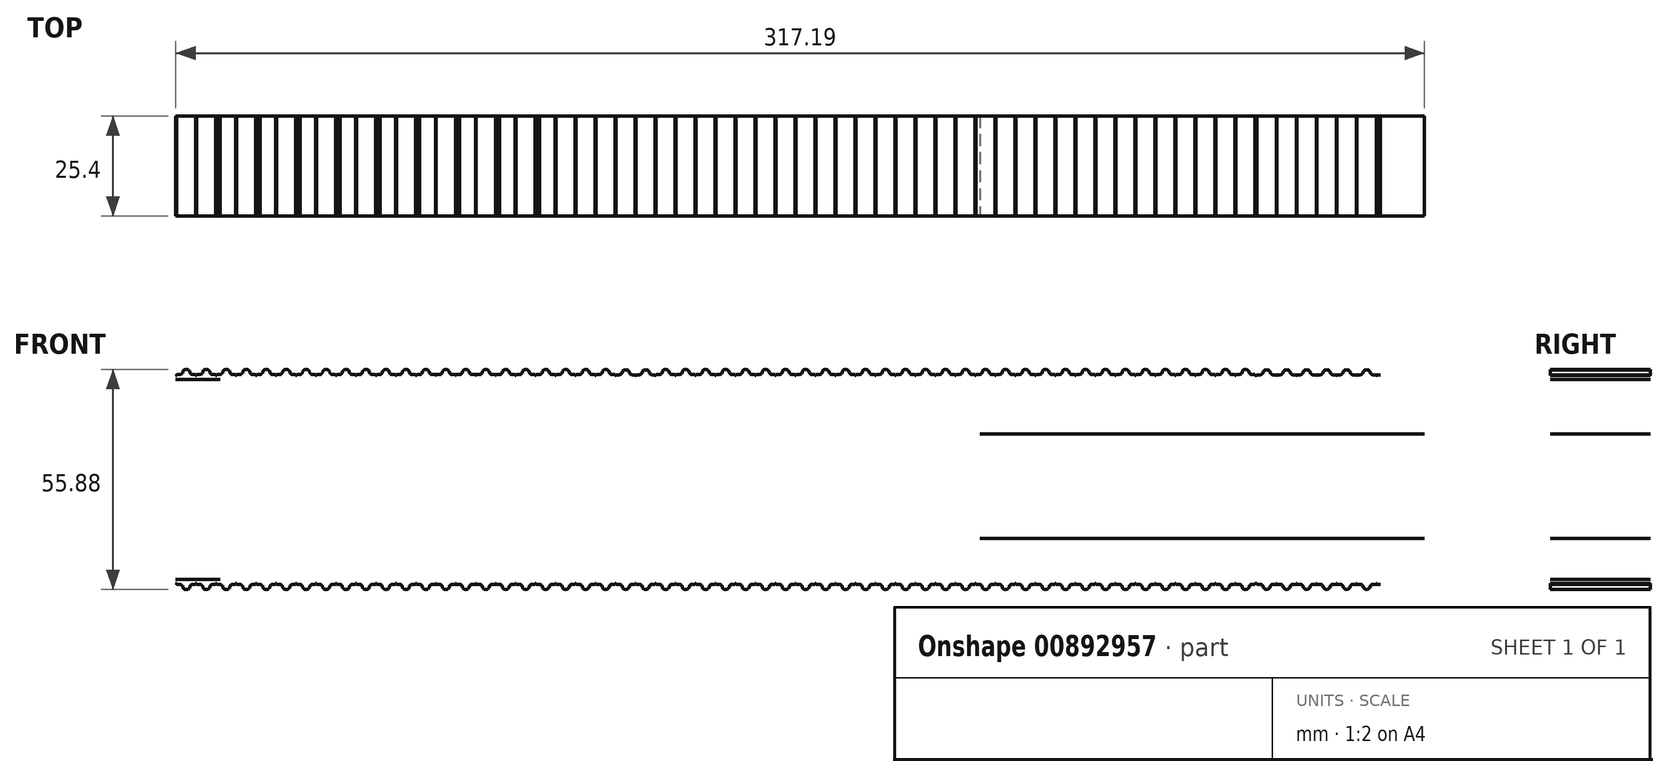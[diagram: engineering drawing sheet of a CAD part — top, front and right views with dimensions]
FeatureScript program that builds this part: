
annotation { "Feature Type Name" : "Feature", "Feature Type Description" : "" }
export const myFeature = defineFeature(function(context is Context, id is Id, definition is map)
    precondition{}
    {
        {
            var Q0;
            Q0=qCreatedBy(makeId("Front.planeOp"),FACE);
            var sketch = newSketch(context, id + "F0", { "sketchPlane" : qUnion([Q0])});
            skLineSegment(sketch, "E0", {"start": v(0, 0) * mm, "end": v(0, -1.05) * mm, "construction": true});
            skLineSegment(sketch, "E1", {"start": v(0, -1.05) * mm, "end": v(0.22, -1.05) * mm});
            skLineSegment(sketch, "E2", {"start": v(0.22, -1.05) * mm, "end": v(0.22, -1.27) * mm});
            skLineSegment(sketch, "E3", {"start": v(0.22, -1.27) * mm, "end": v(1.08, -1.27) * mm});
            skLineSegment(sketch, "E4", {"start": v(1.68, -1.7) * mm, "end": v(1.84, -2.12) * mm});
            skLineSegment(sketch, "E5", {"start": v(2.44, -2.54) * mm, "end": v(2.86, -2.54) * mm});
            skLineSegment(sketch, "E6", {"start": v(3.46, -2.12) * mm, "end": v(3.62, -1.7) * mm});
            skLineSegment(sketch, "E7", {"start": v(4.22, -1.27) * mm, "end": v(5.08, -1.27) * mm});
            skLineSegment(sketch, "E8", {"start": v(5.08, -1.27) * mm, "end": v(5.08, -1.05) * mm});
            skLineSegment(sketch, "E9", {"start": v(5.08, -1.05) * mm, "end": v(5.3, -1.05) * mm});
            skLineSegment(sketch, "E10", {"start": v(5.3, -1.05) * mm, "end": v(5.3, -1.27) * mm});
            skLineSegment(sketch, "E11", {"start": v(5.3, -1.27) * mm, "end": v(6.16, -1.27) * mm});
            skLineSegment(sketch, "E12", {"start": v(6.76, -1.7) * mm, "end": v(6.92, -2.12) * mm});
            skLineSegment(sketch, "E13", {"start": v(7.52, -2.54) * mm, "end": v(7.94, -2.54) * mm});
            skLineSegment(sketch, "E14", {"start": v(8.54, -2.12) * mm, "end": v(8.7, -1.7) * mm});
            skLineSegment(sketch, "E15", {"start": v(9.3, -1.27) * mm, "end": v(10.16, -1.27) * mm});
            skLineSegment(sketch, "E16", {"start": v(10.16, -1.27) * mm, "end": v(10.16, -1.05) * mm});
            skLineSegment(sketch, "E17", {"start": v(10.16, -1.05) * mm, "end": v(10.38, -1.05) * mm});
            skLineSegment(sketch, "E18", {"start": v(11.24, 0) * mm, "end": v(0, 0) * mm});
            skPoint(sketch, "E19", {"position": v(1.76, -1.9) * mm});
            skPoint(sketch, "E20", {"position": v(3.54, -1.9) * mm});
            skPoint(sketch, "E21", {"position": v(2.65, -2.54) * mm});
            skPoint(sketch, "E22", {"position": v(7.73, -2.54) * mm});
            skPoint(sketch, "E23", {"position": v(5.2, -1.05) * mm});
            skLineSegment(sketch, "E24", {"start": v(5.2, -1.05) * mm, "end": v(5.2, -1.34) * mm, "construction": true});
            skLineSegment(sketch, "E25", {"start": v(5.3, -1.16) * mm, "end": v(5.08, -1.16) * mm, "construction": true});
            skPoint(sketch, "E26.visualSharp", {"position": v(1.53, -1.27) * mm});
            skArc(sketch, "E26.filletArc", {"start": v(1.68, -1.7) * mm, "mid": v(1.45, -1.39) * mm, "end": v(1.08, -1.27) * mm});
            skPoint(sketch, "E27.visualSharp", {"position": v(2, -2.54) * mm});
            skArc(sketch, "E27.filletArc", {"start": v(1.84, -2.12) * mm, "mid": v(2.07, -2.42) * mm, "end": v(2.44, -2.54) * mm});
            skPoint(sketch, "E28.visualSharp", {"position": v(3.3, -2.54) * mm});
            skArc(sketch, "E28.filletArc", {"start": v(2.86, -2.54) * mm, "mid": v(3.23, -2.42) * mm, "end": v(3.46, -2.12) * mm});
            skPoint(sketch, "E29.visualSharp", {"position": v(3.77, -1.27) * mm});
            skArc(sketch, "E29.filletArc", {"start": v(4.22, -1.27) * mm, "mid": v(3.85, -1.39) * mm, "end": v(3.62, -1.7) * mm});
            skPoint(sketch, "E30.visualSharp", {"position": v(6.61, -1.27) * mm});
            skArc(sketch, "E30.filletArc", {"start": v(6.76, -1.7) * mm, "mid": v(6.53, -1.39) * mm, "end": v(6.16, -1.27) * mm});
            skPoint(sketch, "E31.visualSharp", {"position": v(7.07, -2.54) * mm});
            skArc(sketch, "E31.filletArc", {"start": v(6.92, -2.12) * mm, "mid": v(7.15, -2.42) * mm, "end": v(7.52, -2.54) * mm});
            skPoint(sketch, "E32.visualSharp", {"position": v(8.39, -2.54) * mm});
            skArc(sketch, "E32.filletArc", {"start": v(7.94, -2.54) * mm, "mid": v(8.3, -2.42) * mm, "end": v(8.54, -2.12) * mm});
            skPoint(sketch, "E33.visualSharp", {"position": v(8.85, -1.27) * mm});
            skArc(sketch, "E33.filletArc", {"start": v(9.3, -1.27) * mm, "mid": v(8.93, -1.39) * mm, "end": v(8.7, -1.7) * mm});
            skLineSegment(sketch, "E34", {"start": v(10.38, -1.05) * mm, "end": v(10.38, -1.27) * mm});
            skLineSegment(sketch, "E35", {"start": v(10.38, -1.27) * mm, "end": v(11.24, -1.27) * mm});
            skLineSegment(sketch, "E36", {"start": v(11.24, -1.27) * mm, "end": v(11.24, 0) * mm, "construction": true});
            skLineSegment(sketch, "E37", {"start": v(0, 0) * mm, "end": v(304.8, 0) * mm, "construction": true});
            skLineSegment(sketch, "E38.0", {"start": v(0, 50.8) * mm, "end": v(304.8, 50.8) * mm, "construction": true});
            skArc(sketch, "E39", {"start": v(0, 50.8) * mm, "mid": v(-25.4, 25.4) * mm, "end": v(0, 0) * mm, "construction": true});
            skLineSegment(sketch, "E40", {"start": v(0, 25.4) * mm, "end": v(304.8, 25.4) * mm, "construction": true});
            skLineSegment(sketch, "E41", {"start": v(152.4, 50.8) * mm, "end": v(152.4, 0) * mm, "construction": true});
            skPoint(sketch, "E42.1.0.0", {"position": v(17.88, -2.53) * mm});
            skLineSegment(sketch, "E42.1.0.1", {"start": v(20.53, -1.26) * mm, "end": v(21.39, -1.26) * mm});
            skPoint(sketch, "E42.1.0.2", {"position": v(17.22, -2.53) * mm});
            skLineSegment(sketch, "E42.1.0.3", {"start": v(18.69, -2.11) * mm, "end": v(18.84, -1.69) * mm});
            skArc(sketch, "E42.1.0.4", {"start": v(16.9, -1.69) * mm, "mid": v(16.67, -1.38) * mm, "end": v(16.3, -1.26) * mm});
            skPoint(sketch, "E42.1.0.5", {"position": v(11.67, -1.26) * mm});
            skPoint(sketch, "E42.1.0.6", {"position": v(19, -1.26) * mm});
            skPoint(sketch, "E42.1.0.7", {"position": v(12.14, -2.53) * mm});
            skArc(sketch, "E42.1.0.8", {"start": v(11.83, -1.69) * mm, "mid": v(11.6, -1.38) * mm, "end": v(11.23, -1.26) * mm});
            skPoint(sketch, "E42.1.0.9", {"position": v(13.92, -1.26) * mm});
            skLineSegment(sketch, "E42.1.0.10", {"start": v(19.44, -1.26) * mm, "end": v(20.3, -1.26) * mm});
            skLineSegment(sketch, "E42.1.0.11", {"start": v(15.45, -1.26) * mm, "end": v(16.3, -1.26) * mm});
            skPoint(sketch, "E42.1.0.12", {"position": v(18.53, -2.53) * mm});
            skLineSegment(sketch, "E42.1.0.13", {"start": v(16.9, -1.69) * mm, "end": v(17.06, -2.11) * mm});
            skLineSegment(sketch, "E42.1.0.14", {"start": v(14.36, -1.26) * mm, "end": v(15.22, -1.26) * mm});
            skPoint(sketch, "E42.1.0.15", {"position": v(16.75, -1.26) * mm});
            skPoint(sketch, "E42.1.0.16", {"position": v(13.45, -2.53) * mm});
            skPoint(sketch, "E42.1.0.17", {"position": v(15.34, -1.04) * mm});
            skPoint(sketch, "E42.1.0.18", {"position": v(13.68, -1.9) * mm});
            skPoint(sketch, "E42.1.0.19", {"position": v(12.8, -2.53) * mm});
            skArc(sketch, "E42.1.0.20", {"start": v(17.06, -2.11) * mm, "mid": v(17.3, -2.42) * mm, "end": v(17.67, -2.53) * mm});
            skArc(sketch, "E42.1.0.21", {"start": v(11.98, -2.11) * mm, "mid": v(12.22, -2.42) * mm, "end": v(12.59, -2.53) * mm});
            skPoint(sketch, "E42.1.0.22", {"position": v(11.9, -1.9) * mm});
            skArc(sketch, "E42.1.0.23", {"start": v(14.36, -1.26) * mm, "mid": v(14, -1.38) * mm, "end": v(13.76, -1.69) * mm});
            skArc(sketch, "E42.1.0.24", {"start": v(18.08, -2.53) * mm, "mid": v(18.45, -2.42) * mm, "end": v(18.69, -2.11) * mm});
            skLineSegment(sketch, "E42.1.0.25", {"start": v(12.59, -2.53) * mm, "end": v(13, -2.53) * mm});
            skLineSegment(sketch, "E42.1.0.26", {"start": v(11.83, -1.69) * mm, "end": v(11.98, -2.11) * mm});
            skArc(sketch, "E42.1.0.27", {"start": v(19.44, -1.26) * mm, "mid": v(19.08, -1.38) * mm, "end": v(18.84, -1.69) * mm});
            skArc(sketch, "E42.1.0.28", {"start": v(13, -2.53) * mm, "mid": v(13.37, -2.42) * mm, "end": v(13.6, -2.11) * mm});
            skLineSegment(sketch, "E42.1.0.29", {"start": v(13.6, -2.11) * mm, "end": v(13.76, -1.69) * mm});
            skLineSegment(sketch, "E42.1.0.30", {"start": v(17.67, -2.53) * mm, "end": v(18.08, -2.53) * mm});
            skLineSegment(sketch, "E42.1.0.31", {"start": v(15.34, -1.04) * mm, "end": v(15.34, -1.33) * mm, "construction": true});
            skLineSegment(sketch, "E42.1.0.32", {"start": v(20.3, -1.26) * mm, "end": v(20.3, -1.04) * mm});
            skLineSegment(sketch, "E42.1.0.33", {"start": v(20.53, -1.04) * mm, "end": v(20.53, -1.26) * mm});
            skLineSegment(sketch, "E42.1.0.34", {"start": v(15.22, -1.26) * mm, "end": v(15.22, -1.04) * mm});
            skLineSegment(sketch, "E42.1.0.35", {"start": v(15.45, -1.15) * mm, "end": v(15.22, -1.15) * mm, "construction": true});
            skLineSegment(sketch, "E42.1.0.36", {"start": v(15.45, -1.04) * mm, "end": v(15.45, -1.26) * mm});
            skLineSegment(sketch, "E42.1.0.37", {"start": v(15.22, -1.04) * mm, "end": v(15.45, -1.04) * mm});
            skLineSegment(sketch, "E42.1.0.38", {"start": v(20.3, -1.04) * mm, "end": v(20.53, -1.04) * mm});
            skPoint(sketch, "E42.2.0.0", {"position": v(28.02, -2.53) * mm});
            skLineSegment(sketch, "E42.2.0.1", {"start": v(30.67, -1.26) * mm, "end": v(31.53, -1.26) * mm});
            skPoint(sketch, "E42.2.0.2", {"position": v(27.36, -2.53) * mm});
            skLineSegment(sketch, "E42.2.0.3", {"start": v(28.83, -2.1) * mm, "end": v(28.99, -1.68) * mm});
            skArc(sketch, "E42.2.0.4", {"start": v(27.05, -1.68) * mm, "mid": v(26.82, -1.38) * mm, "end": v(26.45, -1.26) * mm});
            skPoint(sketch, "E42.2.0.5", {"position": v(21.82, -1.26) * mm});
            skPoint(sketch, "E42.2.0.6", {"position": v(29.14, -1.26) * mm});
            skPoint(sketch, "E42.2.0.7", {"position": v(22.28, -2.53) * mm});
            skArc(sketch, "E42.2.0.8", {"start": v(21.97, -1.68) * mm, "mid": v(21.74, -1.38) * mm, "end": v(21.37, -1.26) * mm});
            skPoint(sketch, "E42.2.0.9", {"position": v(24.06, -1.26) * mm});
            skLineSegment(sketch, "E42.2.0.10", {"start": v(29.59, -1.26) * mm, "end": v(30.45, -1.26) * mm});
            skLineSegment(sketch, "E42.2.0.11", {"start": v(25.6, -1.26) * mm, "end": v(26.45, -1.26) * mm});
            skPoint(sketch, "E42.2.0.12", {"position": v(28.68, -2.53) * mm});
            skLineSegment(sketch, "E42.2.0.13", {"start": v(27.05, -1.68) * mm, "end": v(27.2, -2.1) * mm});
            skLineSegment(sketch, "E42.2.0.14", {"start": v(24.5, -1.26) * mm, "end": v(25.37, -1.26) * mm});
            skPoint(sketch, "E42.2.0.15", {"position": v(26.9, -1.26) * mm});
            skPoint(sketch, "E42.2.0.16", {"position": v(23.6, -2.53) * mm});
            skPoint(sketch, "E42.2.0.17", {"position": v(25.48, -1.04) * mm});
            skPoint(sketch, "E42.2.0.18", {"position": v(23.83, -1.9) * mm});
            skPoint(sketch, "E42.2.0.19", {"position": v(22.94, -2.53) * mm});
            skArc(sketch, "E42.2.0.20", {"start": v(27.2, -2.1) * mm, "mid": v(27.44, -2.41) * mm, "end": v(27.8, -2.53) * mm});
            skArc(sketch, "E42.2.0.21", {"start": v(22.13, -2.1) * mm, "mid": v(22.36, -2.41) * mm, "end": v(22.73, -2.53) * mm});
            skPoint(sketch, "E42.2.0.22", {"position": v(22.05, -1.9) * mm});
            skArc(sketch, "E42.2.0.23", {"start": v(24.5, -1.26) * mm, "mid": v(24.14, -1.38) * mm, "end": v(23.9, -1.68) * mm});
            skArc(sketch, "E42.2.0.24", {"start": v(28.23, -2.53) * mm, "mid": v(28.6, -2.41) * mm, "end": v(28.83, -2.1) * mm});
            skLineSegment(sketch, "E42.2.0.25", {"start": v(22.73, -2.53) * mm, "end": v(23.15, -2.53) * mm});
            skLineSegment(sketch, "E42.2.0.26", {"start": v(21.97, -1.68) * mm, "end": v(22.13, -2.1) * mm});
            skArc(sketch, "E42.2.0.27", {"start": v(29.59, -1.26) * mm, "mid": v(29.22, -1.38) * mm, "end": v(28.99, -1.68) * mm});
            skArc(sketch, "E42.2.0.28", {"start": v(23.15, -2.53) * mm, "mid": v(23.52, -2.41) * mm, "end": v(23.75, -2.1) * mm});
            skLineSegment(sketch, "E42.2.0.29", {"start": v(23.75, -2.1) * mm, "end": v(23.9, -1.68) * mm});
            skLineSegment(sketch, "E42.2.0.30", {"start": v(27.8, -2.53) * mm, "end": v(28.23, -2.53) * mm});
            skLineSegment(sketch, "E42.2.0.31", {"start": v(25.48, -1.04) * mm, "end": v(25.48, -1.33) * mm, "construction": true});
            skLineSegment(sketch, "E42.2.0.32", {"start": v(30.45, -1.26) * mm, "end": v(30.45, -1.04) * mm});
            skLineSegment(sketch, "E42.2.0.33", {"start": v(30.67, -1.04) * mm, "end": v(30.67, -1.26) * mm});
            skLineSegment(sketch, "E42.2.0.34", {"start": v(25.37, -1.26) * mm, "end": v(25.37, -1.04) * mm});
            skLineSegment(sketch, "E42.2.0.35", {"start": v(25.6, -1.15) * mm, "end": v(25.37, -1.15) * mm, "construction": true});
            skLineSegment(sketch, "E42.2.0.36", {"start": v(25.6, -1.04) * mm, "end": v(25.6, -1.26) * mm});
            skLineSegment(sketch, "E42.2.0.37", {"start": v(25.37, -1.04) * mm, "end": v(25.6, -1.04) * mm});
            skLineSegment(sketch, "E42.2.0.38", {"start": v(30.45, -1.04) * mm, "end": v(30.67, -1.04) * mm});
            skPoint(sketch, "E42.3.0.0", {"position": v(38.16, -2.52) * mm});
            skLineSegment(sketch, "E42.3.0.1", {"start": v(40.81, -1.25) * mm, "end": v(41.67, -1.25) * mm});
            skPoint(sketch, "E42.3.0.2", {"position": v(37.5, -2.52) * mm});
            skLineSegment(sketch, "E42.3.0.3", {"start": v(38.97, -2.1) * mm, "end": v(39.13, -1.68) * mm});
            skArc(sketch, "E42.3.0.4", {"start": v(37.2, -1.68) * mm, "mid": v(36.96, -1.37) * mm, "end": v(36.6, -1.25) * mm});
            skPoint(sketch, "E42.3.0.5", {"position": v(31.96, -1.25) * mm});
            skPoint(sketch, "E42.3.0.6", {"position": v(39.28, -1.25) * mm});
            skPoint(sketch, "E42.3.0.7", {"position": v(32.43, -2.52) * mm});
            skArc(sketch, "E42.3.0.8", {"start": v(32.12, -1.68) * mm, "mid": v(31.88, -1.37) * mm, "end": v(31.51, -1.25) * mm});
            skPoint(sketch, "E42.3.0.9", {"position": v(34.2, -1.25) * mm});
            skLineSegment(sketch, "E42.3.0.10", {"start": v(39.73, -1.25) * mm, "end": v(40.6, -1.25) * mm});
            skLineSegment(sketch, "E42.3.0.11", {"start": v(35.73, -1.25) * mm, "end": v(36.6, -1.25) * mm});
            skPoint(sketch, "E42.3.0.12", {"position": v(38.82, -2.52) * mm});
            skLineSegment(sketch, "E42.3.0.13", {"start": v(37.2, -1.68) * mm, "end": v(37.35, -2.1) * mm});
            skLineSegment(sketch, "E42.3.0.14", {"start": v(34.65, -1.25) * mm, "end": v(35.51, -1.25) * mm});
            skPoint(sketch, "E42.3.0.15", {"position": v(37.04, -1.25) * mm});
            skPoint(sketch, "E42.3.0.16", {"position": v(33.74, -2.52) * mm});
            skPoint(sketch, "E42.3.0.17", {"position": v(35.62, -1.03) * mm});
            skPoint(sketch, "E42.3.0.18", {"position": v(33.97, -1.89) * mm});
            skPoint(sketch, "E42.3.0.19", {"position": v(33.08, -2.52) * mm});
            skArc(sketch, "E42.3.0.20", {"start": v(37.35, -2.1) * mm, "mid": v(37.59, -2.4) * mm, "end": v(37.95, -2.52) * mm});
            skArc(sketch, "E42.3.0.21", {"start": v(32.27, -2.1) * mm, "mid": v(32.5, -2.4) * mm, "end": v(32.87, -2.52) * mm});
            skPoint(sketch, "E42.3.0.22", {"position": v(32.2, -1.89) * mm});
            skArc(sketch, "E42.3.0.23", {"start": v(34.65, -1.25) * mm, "mid": v(34.28, -1.37) * mm, "end": v(34.05, -1.68) * mm});
            skArc(sketch, "E42.3.0.24", {"start": v(38.37, -2.52) * mm, "mid": v(38.74, -2.4) * mm, "end": v(38.97, -2.1) * mm});
            skLineSegment(sketch, "E42.3.0.25", {"start": v(32.87, -2.52) * mm, "end": v(33.3, -2.52) * mm});
            skLineSegment(sketch, "E42.3.0.26", {"start": v(32.12, -1.68) * mm, "end": v(32.27, -2.1) * mm});
            skArc(sketch, "E42.3.0.27", {"start": v(39.73, -1.25) * mm, "mid": v(39.36, -1.37) * mm, "end": v(39.13, -1.68) * mm});
            skArc(sketch, "E42.3.0.28", {"start": v(33.3, -2.52) * mm, "mid": v(33.66, -2.4) * mm, "end": v(33.9, -2.1) * mm});
            skLineSegment(sketch, "E42.3.0.29", {"start": v(33.9, -2.1) * mm, "end": v(34.05, -1.68) * mm});
            skLineSegment(sketch, "E42.3.0.30", {"start": v(37.95, -2.52) * mm, "end": v(38.37, -2.52) * mm});
            skLineSegment(sketch, "E42.3.0.31", {"start": v(35.62, -1.03) * mm, "end": v(35.62, -1.32) * mm, "construction": true});
            skLineSegment(sketch, "E42.3.0.32", {"start": v(40.6, -1.25) * mm, "end": v(40.6, -1.03) * mm});
            skLineSegment(sketch, "E42.3.0.33", {"start": v(40.81, -1.03) * mm, "end": v(40.81, -1.25) * mm});
            skLineSegment(sketch, "E42.3.0.34", {"start": v(35.51, -1.25) * mm, "end": v(35.51, -1.03) * mm});
            skLineSegment(sketch, "E42.3.0.35", {"start": v(35.73, -1.14) * mm, "end": v(35.51, -1.14) * mm, "construction": true});
            skLineSegment(sketch, "E42.3.0.36", {"start": v(35.73, -1.03) * mm, "end": v(35.73, -1.25) * mm});
            skLineSegment(sketch, "E42.3.0.37", {"start": v(35.51, -1.03) * mm, "end": v(35.73, -1.03) * mm});
            skLineSegment(sketch, "E42.3.0.38", {"start": v(40.6, -1.03) * mm, "end": v(40.81, -1.03) * mm});
            skPoint(sketch, "E42.4.0.0", {"position": v(48.3, -2.52) * mm});
            skLineSegment(sketch, "E42.4.0.1", {"start": v(50.96, -1.25) * mm, "end": v(51.82, -1.25) * mm});
            skPoint(sketch, "E42.4.0.2", {"position": v(47.65, -2.52) * mm});
            skLineSegment(sketch, "E42.4.0.3", {"start": v(49.12, -2.1) * mm, "end": v(49.27, -1.67) * mm});
            skArc(sketch, "E42.4.0.4", {"start": v(47.34, -1.67) * mm, "mid": v(47.1, -1.37) * mm, "end": v(46.74, -1.25) * mm});
            skPoint(sketch, "E42.4.0.5", {"position": v(42.1, -1.25) * mm});
            skPoint(sketch, "E42.4.0.6", {"position": v(49.43, -1.25) * mm});
            skPoint(sketch, "E42.4.0.7", {"position": v(42.57, -2.52) * mm});
            skArc(sketch, "E42.4.0.8", {"start": v(42.26, -1.67) * mm, "mid": v(42.03, -1.37) * mm, "end": v(41.66, -1.25) * mm});
            skPoint(sketch, "E42.4.0.9", {"position": v(44.35, -1.25) * mm});
            skLineSegment(sketch, "E42.4.0.10", {"start": v(49.88, -1.25) * mm, "end": v(50.74, -1.25) * mm});
            skLineSegment(sketch, "E42.4.0.11", {"start": v(45.88, -1.25) * mm, "end": v(46.74, -1.25) * mm});
            skPoint(sketch, "E42.4.0.12", {"position": v(48.96, -2.52) * mm});
            skLineSegment(sketch, "E42.4.0.13", {"start": v(47.34, -1.67) * mm, "end": v(47.5, -2.1) * mm});
            skLineSegment(sketch, "E42.4.0.14", {"start": v(44.8, -1.25) * mm, "end": v(45.66, -1.25) * mm});
            skPoint(sketch, "E42.4.0.15", {"position": v(47.19, -1.25) * mm});
            skPoint(sketch, "E42.4.0.16", {"position": v(43.88, -2.52) * mm});
            skPoint(sketch, "E42.4.0.17", {"position": v(45.77, -1.03) * mm});
            skPoint(sketch, "E42.4.0.18", {"position": v(44.12, -1.88) * mm});
            skPoint(sketch, "E42.4.0.19", {"position": v(43.23, -2.52) * mm});
            skArc(sketch, "E42.4.0.20", {"start": v(47.5, -2.1) * mm, "mid": v(47.73, -2.4) * mm, "end": v(48.1, -2.52) * mm});
            skArc(sketch, "E42.4.0.21", {"start": v(42.42, -2.1) * mm, "mid": v(42.65, -2.4) * mm, "end": v(43.02, -2.52) * mm});
            skPoint(sketch, "E42.4.0.22", {"position": v(42.34, -1.88) * mm});
            skArc(sketch, "E42.4.0.23", {"start": v(44.8, -1.25) * mm, "mid": v(44.43, -1.37) * mm, "end": v(44.2, -1.67) * mm});
            skArc(sketch, "E42.4.0.24", {"start": v(48.52, -2.52) * mm, "mid": v(48.88, -2.4) * mm, "end": v(49.12, -2.1) * mm});
            skLineSegment(sketch, "E42.4.0.25", {"start": v(43.02, -2.52) * mm, "end": v(43.44, -2.52) * mm});
            skLineSegment(sketch, "E42.4.0.26", {"start": v(42.26, -1.67) * mm, "end": v(42.42, -2.1) * mm});
            skArc(sketch, "E42.4.0.27", {"start": v(49.88, -1.25) * mm, "mid": v(49.5, -1.37) * mm, "end": v(49.27, -1.67) * mm});
            skArc(sketch, "E42.4.0.28", {"start": v(43.44, -2.52) * mm, "mid": v(43.8, -2.4) * mm, "end": v(44.04, -2.1) * mm});
            skLineSegment(sketch, "E42.4.0.29", {"start": v(44.04, -2.1) * mm, "end": v(44.2, -1.67) * mm});
            skLineSegment(sketch, "E42.4.0.30", {"start": v(48.1, -2.52) * mm, "end": v(48.52, -2.52) * mm});
            skLineSegment(sketch, "E42.4.0.31", {"start": v(45.77, -1.03) * mm, "end": v(45.77, -1.32) * mm, "construction": true});
            skLineSegment(sketch, "E42.4.0.32", {"start": v(50.74, -1.25) * mm, "end": v(50.74, -1.03) * mm});
            skLineSegment(sketch, "E42.4.0.33", {"start": v(50.96, -1.03) * mm, "end": v(50.96, -1.25) * mm});
            skLineSegment(sketch, "E42.4.0.34", {"start": v(45.66, -1.25) * mm, "end": v(45.66, -1.03) * mm});
            skLineSegment(sketch, "E42.4.0.35", {"start": v(45.88, -1.14) * mm, "end": v(45.66, -1.14) * mm, "construction": true});
            skLineSegment(sketch, "E42.4.0.36", {"start": v(45.88, -1.03) * mm, "end": v(45.88, -1.25) * mm});
            skLineSegment(sketch, "E42.4.0.37", {"start": v(45.66, -1.03) * mm, "end": v(45.88, -1.03) * mm});
            skLineSegment(sketch, "E42.4.0.38", {"start": v(50.74, -1.03) * mm, "end": v(50.96, -1.03) * mm});
            skPoint(sketch, "E42.5.0.0", {"position": v(58.45, -2.51) * mm});
            skLineSegment(sketch, "E42.5.0.1", {"start": v(61.1, -1.24) * mm, "end": v(61.96, -1.24) * mm});
            skPoint(sketch, "E42.5.0.2", {"position": v(57.8, -2.51) * mm});
            skLineSegment(sketch, "E42.5.0.3", {"start": v(59.26, -2.1) * mm, "end": v(59.42, -1.67) * mm});
            skArc(sketch, "E42.5.0.4", {"start": v(57.48, -1.67) * mm, "mid": v(57.25, -1.36) * mm, "end": v(56.88, -1.24) * mm});
            skPoint(sketch, "E42.5.0.5", {"position": v(52.25, -1.24) * mm});
            skPoint(sketch, "E42.5.0.6", {"position": v(59.57, -1.24) * mm});
            skPoint(sketch, "E42.5.0.7", {"position": v(52.71, -2.51) * mm});
            skArc(sketch, "E42.5.0.8", {"start": v(52.4, -1.67) * mm, "mid": v(52.17, -1.36) * mm, "end": v(51.8, -1.24) * mm});
            skPoint(sketch, "E42.5.0.9", {"position": v(54.5, -1.24) * mm});
            skLineSegment(sketch, "E42.5.0.10", {"start": v(60.02, -1.24) * mm, "end": v(60.88, -1.24) * mm});
            skLineSegment(sketch, "E42.5.0.11", {"start": v(56.02, -1.24) * mm, "end": v(56.88, -1.24) * mm});
            skPoint(sketch, "E42.5.0.12", {"position": v(59.1, -2.51) * mm});
            skLineSegment(sketch, "E42.5.0.13", {"start": v(57.48, -1.67) * mm, "end": v(57.64, -2.1) * mm});
            skLineSegment(sketch, "E42.5.0.14", {"start": v(54.94, -1.24) * mm, "end": v(55.8, -1.24) * mm});
            skPoint(sketch, "E42.5.0.15", {"position": v(57.33, -1.24) * mm});
            skPoint(sketch, "E42.5.0.16", {"position": v(54.03, -2.51) * mm});
            skPoint(sketch, "E42.5.0.17", {"position": v(55.91, -1.02) * mm});
            skPoint(sketch, "E42.5.0.18", {"position": v(54.26, -1.88) * mm});
            skPoint(sketch, "E42.5.0.19", {"position": v(53.37, -2.51) * mm});
            skArc(sketch, "E42.5.0.20", {"start": v(57.64, -2.1) * mm, "mid": v(57.87, -2.4) * mm, "end": v(58.24, -2.51) * mm});
            skArc(sketch, "E42.5.0.21", {"start": v(52.56, -2.1) * mm, "mid": v(52.8, -2.4) * mm, "end": v(53.16, -2.51) * mm});
            skPoint(sketch, "E42.5.0.22", {"position": v(52.48, -1.88) * mm});
            skArc(sketch, "E42.5.0.23", {"start": v(54.94, -1.24) * mm, "mid": v(54.57, -1.36) * mm, "end": v(54.34, -1.67) * mm});
            skArc(sketch, "E42.5.0.24", {"start": v(58.66, -2.51) * mm, "mid": v(59.03, -2.4) * mm, "end": v(59.26, -2.1) * mm});
            skLineSegment(sketch, "E42.5.0.25", {"start": v(53.16, -2.51) * mm, "end": v(53.58, -2.51) * mm});
            skLineSegment(sketch, "E42.5.0.26", {"start": v(52.4, -1.67) * mm, "end": v(52.56, -2.1) * mm});
            skArc(sketch, "E42.5.0.27", {"start": v(60.02, -1.24) * mm, "mid": v(59.65, -1.36) * mm, "end": v(59.42, -1.67) * mm});
            skArc(sketch, "E42.5.0.28", {"start": v(53.58, -2.51) * mm, "mid": v(53.95, -2.4) * mm, "end": v(54.18, -2.1) * mm});
            skLineSegment(sketch, "E42.5.0.29", {"start": v(54.18, -2.1) * mm, "end": v(54.34, -1.67) * mm});
            skLineSegment(sketch, "E42.5.0.30", {"start": v(58.24, -2.51) * mm, "end": v(58.66, -2.51) * mm});
            skLineSegment(sketch, "E42.5.0.31", {"start": v(55.91, -1.02) * mm, "end": v(55.91, -1.31) * mm, "construction": true});
            skLineSegment(sketch, "E42.5.0.32", {"start": v(60.88, -1.24) * mm, "end": v(60.88, -1.02) * mm});
            skLineSegment(sketch, "E42.5.0.33", {"start": v(61.1, -1.02) * mm, "end": v(61.1, -1.24) * mm});
            skLineSegment(sketch, "E42.5.0.34", {"start": v(55.8, -1.24) * mm, "end": v(55.8, -1.02) * mm});
            skLineSegment(sketch, "E42.5.0.35", {"start": v(56.02, -1.13) * mm, "end": v(55.8, -1.13) * mm, "construction": true});
            skLineSegment(sketch, "E42.5.0.36", {"start": v(56.02, -1.02) * mm, "end": v(56.02, -1.24) * mm});
            skLineSegment(sketch, "E42.5.0.37", {"start": v(55.8, -1.02) * mm, "end": v(56.02, -1.02) * mm});
            skLineSegment(sketch, "E42.5.0.38", {"start": v(60.88, -1.02) * mm, "end": v(61.1, -1.02) * mm});
            skPoint(sketch, "E42.6.0.0", {"position": v(68.6, -2.5) * mm});
            skLineSegment(sketch, "E42.6.0.1", {"start": v(71.25, -1.24) * mm, "end": v(72.1, -1.24) * mm});
            skPoint(sketch, "E42.6.0.2", {"position": v(67.94, -2.5) * mm});
            skLineSegment(sketch, "E42.6.0.3", {"start": v(69.4, -2.09) * mm, "end": v(69.56, -1.66) * mm});
            skArc(sketch, "E42.6.0.4", {"start": v(67.63, -1.66) * mm, "mid": v(67.4, -1.36) * mm, "end": v(67.03, -1.24) * mm});
            skPoint(sketch, "E42.6.0.5", {"position": v(62.4, -1.24) * mm});
            skPoint(sketch, "E42.6.0.6", {"position": v(69.71, -1.24) * mm});
            skPoint(sketch, "E42.6.0.7", {"position": v(62.86, -2.5) * mm});
            skArc(sketch, "E42.6.0.8", {"start": v(62.55, -1.66) * mm, "mid": v(62.31, -1.36) * mm, "end": v(61.95, -1.24) * mm});
            skPoint(sketch, "E42.6.0.9", {"position": v(64.63, -1.24) * mm});
            skLineSegment(sketch, "E42.6.0.10", {"start": v(70.16, -1.24) * mm, "end": v(71.02, -1.24) * mm});
            skLineSegment(sketch, "E42.6.0.11", {"start": v(66.17, -1.24) * mm, "end": v(67.03, -1.24) * mm});
            skPoint(sketch, "E42.6.0.12", {"position": v(69.25, -2.5) * mm});
            skLineSegment(sketch, "E42.6.0.13", {"start": v(67.63, -1.66) * mm, "end": v(67.78, -2.09) * mm});
            skLineSegment(sketch, "E42.6.0.14", {"start": v(65.08, -1.24) * mm, "end": v(65.94, -1.24) * mm});
            skPoint(sketch, "E42.6.0.15", {"position": v(67.47, -1.24) * mm});
            skPoint(sketch, "E42.6.0.16", {"position": v(64.17, -2.5) * mm});
            skPoint(sketch, "E42.6.0.17", {"position": v(66.05, -1.02) * mm});
            skPoint(sketch, "E42.6.0.18", {"position": v(64.4, -1.87) * mm});
            skPoint(sketch, "E42.6.0.19", {"position": v(63.51, -2.5) * mm});
            skArc(sketch, "E42.6.0.20", {"start": v(67.78, -2.09) * mm, "mid": v(68.02, -2.4) * mm, "end": v(68.39, -2.5) * mm});
            skArc(sketch, "E42.6.0.21", {"start": v(62.7, -2.09) * mm, "mid": v(62.94, -2.4) * mm, "end": v(63.3, -2.5) * mm});
            skPoint(sketch, "E42.6.0.22", {"position": v(62.63, -1.87) * mm});
            skArc(sketch, "E42.6.0.23", {"start": v(65.08, -1.24) * mm, "mid": v(64.72, -1.36) * mm, "end": v(64.48, -1.66) * mm});
            skArc(sketch, "E42.6.0.24", {"start": v(68.8, -2.5) * mm, "mid": v(69.17, -2.4) * mm, "end": v(69.4, -2.09) * mm});
            skLineSegment(sketch, "E42.6.0.25", {"start": v(63.3, -2.5) * mm, "end": v(63.72, -2.5) * mm});
            skLineSegment(sketch, "E42.6.0.26", {"start": v(62.55, -1.66) * mm, "end": v(62.7, -2.09) * mm});
            skArc(sketch, "E42.6.0.27", {"start": v(70.16, -1.24) * mm, "mid": v(69.8, -1.36) * mm, "end": v(69.56, -1.66) * mm});
            skArc(sketch, "E42.6.0.28", {"start": v(63.72, -2.5) * mm, "mid": v(64.1, -2.4) * mm, "end": v(64.33, -2.09) * mm});
            skLineSegment(sketch, "E42.6.0.29", {"start": v(64.33, -2.09) * mm, "end": v(64.48, -1.66) * mm});
            skLineSegment(sketch, "E42.6.0.30", {"start": v(68.39, -2.5) * mm, "end": v(68.8, -2.5) * mm});
            skLineSegment(sketch, "E42.6.0.31", {"start": v(66.05, -1.02) * mm, "end": v(66.05, -1.3) * mm, "construction": true});
            skLineSegment(sketch, "E42.6.0.32", {"start": v(71.02, -1.24) * mm, "end": v(71.02, -1.02) * mm});
            skLineSegment(sketch, "E42.6.0.33", {"start": v(71.25, -1.02) * mm, "end": v(71.25, -1.24) * mm});
            skLineSegment(sketch, "E42.6.0.34", {"start": v(65.94, -1.24) * mm, "end": v(65.94, -1.02) * mm});
            skLineSegment(sketch, "E42.6.0.35", {"start": v(66.17, -1.13) * mm, "end": v(65.94, -1.13) * mm, "construction": true});
            skLineSegment(sketch, "E42.6.0.36", {"start": v(66.17, -1.02) * mm, "end": v(66.17, -1.24) * mm});
            skLineSegment(sketch, "E42.6.0.37", {"start": v(65.94, -1.02) * mm, "end": v(66.17, -1.02) * mm});
            skLineSegment(sketch, "E42.6.0.38", {"start": v(71.02, -1.02) * mm, "end": v(71.25, -1.02) * mm});
            skPoint(sketch, "E42.7.0.0", {"position": v(78.74, -2.5) * mm});
            skLineSegment(sketch, "E42.7.0.1", {"start": v(81.39, -1.23) * mm, "end": v(82.25, -1.23) * mm});
            skPoint(sketch, "E42.7.0.2", {"position": v(78.08, -2.5) * mm});
            skLineSegment(sketch, "E42.7.0.3", {"start": v(79.55, -2.08) * mm, "end": v(79.7, -1.66) * mm});
            skArc(sketch, "E42.7.0.4", {"start": v(77.77, -1.66) * mm, "mid": v(77.54, -1.35) * mm, "end": v(77.17, -1.23) * mm});
            skPoint(sketch, "E42.7.0.5", {"position": v(72.54, -1.23) * mm});
            skPoint(sketch, "E42.7.0.6", {"position": v(79.86, -1.23) * mm});
            skPoint(sketch, "E42.7.0.7", {"position": v(73, -2.5) * mm});
            skArc(sketch, "E42.7.0.8", {"start": v(72.7, -1.66) * mm, "mid": v(72.46, -1.35) * mm, "end": v(72.1, -1.23) * mm});
            skPoint(sketch, "E42.7.0.9", {"position": v(74.78, -1.23) * mm});
            skLineSegment(sketch, "E42.7.0.10", {"start": v(80.3, -1.23) * mm, "end": v(81.17, -1.23) * mm});
            skLineSegment(sketch, "E42.7.0.11", {"start": v(76.3, -1.23) * mm, "end": v(77.17, -1.23) * mm});
            skPoint(sketch, "E42.7.0.12", {"position": v(79.4, -2.5) * mm});
            skLineSegment(sketch, "E42.7.0.13", {"start": v(77.77, -1.66) * mm, "end": v(77.93, -2.08) * mm});
            skLineSegment(sketch, "E42.7.0.14", {"start": v(75.23, -1.23) * mm, "end": v(76.09, -1.23) * mm});
            skPoint(sketch, "E42.7.0.15", {"position": v(77.62, -1.23) * mm});
            skPoint(sketch, "E42.7.0.16", {"position": v(74.32, -2.5) * mm});
            skPoint(sketch, "E42.7.0.17", {"position": v(76.2, -1.01) * mm});
            skPoint(sketch, "E42.7.0.18", {"position": v(74.55, -1.87) * mm});
            skPoint(sketch, "E42.7.0.19", {"position": v(73.66, -2.5) * mm});
            skArc(sketch, "E42.7.0.20", {"start": v(77.93, -2.08) * mm, "mid": v(78.16, -2.39) * mm, "end": v(78.53, -2.5) * mm});
            skArc(sketch, "E42.7.0.21", {"start": v(72.85, -2.08) * mm, "mid": v(73.08, -2.39) * mm, "end": v(73.45, -2.5) * mm});
            skPoint(sketch, "E42.7.0.22", {"position": v(72.77, -1.87) * mm});
            skArc(sketch, "E42.7.0.23", {"start": v(75.23, -1.23) * mm, "mid": v(74.86, -1.35) * mm, "end": v(74.63, -1.66) * mm});
            skArc(sketch, "E42.7.0.24", {"start": v(78.95, -2.5) * mm, "mid": v(79.32, -2.39) * mm, "end": v(79.55, -2.08) * mm});
            skLineSegment(sketch, "E42.7.0.25", {"start": v(73.45, -2.5) * mm, "end": v(73.87, -2.5) * mm});
            skLineSegment(sketch, "E42.7.0.26", {"start": v(72.7, -1.66) * mm, "end": v(72.85, -2.08) * mm});
            skArc(sketch, "E42.7.0.27", {"start": v(80.3, -1.23) * mm, "mid": v(79.94, -1.35) * mm, "end": v(79.7, -1.66) * mm});
            skArc(sketch, "E42.7.0.28", {"start": v(73.87, -2.5) * mm, "mid": v(74.24, -2.39) * mm, "end": v(74.47, -2.08) * mm});
            skLineSegment(sketch, "E42.7.0.29", {"start": v(74.47, -2.08) * mm, "end": v(74.63, -1.66) * mm});
            skLineSegment(sketch, "E42.7.0.30", {"start": v(78.53, -2.5) * mm, "end": v(78.95, -2.5) * mm});
            skLineSegment(sketch, "E42.7.0.31", {"start": v(76.2, -1.01) * mm, "end": v(76.2, -1.3) * mm, "construction": true});
            skLineSegment(sketch, "E42.7.0.32", {"start": v(81.17, -1.23) * mm, "end": v(81.17, -1.01) * mm});
            skLineSegment(sketch, "E42.7.0.33", {"start": v(81.39, -1.01) * mm, "end": v(81.39, -1.23) * mm});
            skLineSegment(sketch, "E42.7.0.34", {"start": v(76.09, -1.23) * mm, "end": v(76.09, -1.01) * mm});
            skLineSegment(sketch, "E42.7.0.35", {"start": v(76.3, -1.12) * mm, "end": v(76.09, -1.12) * mm, "construction": true});
            skLineSegment(sketch, "E42.7.0.36", {"start": v(76.3, -1.01) * mm, "end": v(76.3, -1.23) * mm});
            skLineSegment(sketch, "E42.7.0.37", {"start": v(76.09, -1.01) * mm, "end": v(76.3, -1.01) * mm});
            skLineSegment(sketch, "E42.7.0.38", {"start": v(81.17, -1.01) * mm, "end": v(81.39, -1.01) * mm});
            skPoint(sketch, "E42.8.0.0", {"position": v(88.88, -2.5) * mm});
            skLineSegment(sketch, "E42.8.0.1", {"start": v(91.53, -1.23) * mm, "end": v(92.4, -1.23) * mm});
            skPoint(sketch, "E42.8.0.2", {"position": v(88.22, -2.5) * mm});
            skLineSegment(sketch, "E42.8.0.3", {"start": v(89.7, -2.08) * mm, "end": v(89.85, -1.65) * mm});
            skArc(sketch, "E42.8.0.4", {"start": v(87.92, -1.65) * mm, "mid": v(87.68, -1.35) * mm, "end": v(87.31, -1.23) * mm});
            skPoint(sketch, "E42.8.0.5", {"position": v(82.68, -1.23) * mm});
            skPoint(sketch, "E42.8.0.6", {"position": v(90, -1.23) * mm});
            skPoint(sketch, "E42.8.0.7", {"position": v(83.14, -2.5) * mm});
            skArc(sketch, "E42.8.0.8", {"start": v(82.84, -1.65) * mm, "mid": v(82.6, -1.35) * mm, "end": v(82.23, -1.23) * mm});
            skPoint(sketch, "E42.8.0.9", {"position": v(84.92, -1.23) * mm});
            skLineSegment(sketch, "E42.8.0.10", {"start": v(90.45, -1.23) * mm, "end": v(91.31, -1.23) * mm});
            skLineSegment(sketch, "E42.8.0.11", {"start": v(86.45, -1.23) * mm, "end": v(87.31, -1.23) * mm});
            skPoint(sketch, "E42.8.0.12", {"position": v(89.54, -2.5) * mm});
            skLineSegment(sketch, "E42.8.0.13", {"start": v(87.92, -1.65) * mm, "end": v(88.07, -2.08) * mm});
            skLineSegment(sketch, "E42.8.0.14", {"start": v(85.37, -1.23) * mm, "end": v(86.23, -1.23) * mm});
            skPoint(sketch, "E42.8.0.15", {"position": v(87.76, -1.23) * mm});
            skPoint(sketch, "E42.8.0.16", {"position": v(84.46, -2.5) * mm});
            skPoint(sketch, "E42.8.0.17", {"position": v(86.34, -1) * mm});
            skPoint(sketch, "E42.8.0.18", {"position": v(84.7, -1.86) * mm});
            skPoint(sketch, "E42.8.0.19", {"position": v(83.8, -2.5) * mm});
            skArc(sketch, "E42.8.0.20", {"start": v(88.07, -2.08) * mm, "mid": v(88.3, -2.38) * mm, "end": v(88.67, -2.5) * mm});
            skArc(sketch, "E42.8.0.21", {"start": v(83, -2.08) * mm, "mid": v(83.23, -2.38) * mm, "end": v(83.6, -2.5) * mm});
            skPoint(sketch, "E42.8.0.22", {"position": v(82.91, -1.86) * mm});
            skArc(sketch, "E42.8.0.23", {"start": v(85.37, -1.23) * mm, "mid": v(85, -1.35) * mm, "end": v(84.77, -1.65) * mm});
            skArc(sketch, "E42.8.0.24", {"start": v(89.1, -2.5) * mm, "mid": v(89.46, -2.38) * mm, "end": v(89.7, -2.08) * mm});
            skLineSegment(sketch, "E42.8.0.25", {"start": v(83.6, -2.5) * mm, "end": v(84.01, -2.5) * mm});
            skLineSegment(sketch, "E42.8.0.26", {"start": v(82.84, -1.65) * mm, "end": v(83, -2.08) * mm});
            skArc(sketch, "E42.8.0.27", {"start": v(90.45, -1.23) * mm, "mid": v(90.08, -1.35) * mm, "end": v(89.85, -1.65) * mm});
            skArc(sketch, "E42.8.0.28", {"start": v(84.01, -2.5) * mm, "mid": v(84.38, -2.38) * mm, "end": v(84.61, -2.08) * mm});
            skLineSegment(sketch, "E42.8.0.29", {"start": v(84.61, -2.08) * mm, "end": v(84.77, -1.65) * mm});
            skLineSegment(sketch, "E42.8.0.30", {"start": v(88.67, -2.5) * mm, "end": v(89.1, -2.5) * mm});
            skLineSegment(sketch, "E42.8.0.31", {"start": v(86.34, -1) * mm, "end": v(86.34, -1.3) * mm, "construction": true});
            skLineSegment(sketch, "E42.8.0.32", {"start": v(91.31, -1.23) * mm, "end": v(91.31, -1) * mm});
            skLineSegment(sketch, "E42.8.0.33", {"start": v(91.53, -1) * mm, "end": v(91.53, -1.23) * mm});
            skLineSegment(sketch, "E42.8.0.34", {"start": v(86.23, -1.23) * mm, "end": v(86.23, -1) * mm});
            skLineSegment(sketch, "E42.8.0.35", {"start": v(86.45, -1.12) * mm, "end": v(86.23, -1.12) * mm, "construction": true});
            skLineSegment(sketch, "E42.8.0.36", {"start": v(86.45, -1) * mm, "end": v(86.45, -1.23) * mm});
            skLineSegment(sketch, "E42.8.0.37", {"start": v(86.23, -1) * mm, "end": v(86.45, -1) * mm});
            skLineSegment(sketch, "E42.8.0.38", {"start": v(91.31, -1) * mm, "end": v(91.53, -1) * mm});
            skPoint(sketch, "E42.9.0.0", {"position": v(99.03, -2.5) * mm});
            skLineSegment(sketch, "E42.9.0.1", {"start": v(101.68, -1.22) * mm, "end": v(102.54, -1.22) * mm});
            skPoint(sketch, "E42.9.0.2", {"position": v(98.37, -2.5) * mm});
            skLineSegment(sketch, "E42.9.0.3", {"start": v(99.84, -2.07) * mm, "end": v(100, -1.65) * mm});
            skArc(sketch, "E42.9.0.4", {"start": v(98.06, -1.65) * mm, "mid": v(97.83, -1.34) * mm, "end": v(97.46, -1.22) * mm});
            skPoint(sketch, "E42.9.0.5", {"position": v(92.83, -1.22) * mm});
            skPoint(sketch, "E42.9.0.6", {"position": v(100.15, -1.22) * mm});
            skPoint(sketch, "E42.9.0.7", {"position": v(93.29, -2.5) * mm});
            skArc(sketch, "E42.9.0.8", {"start": v(92.98, -1.65) * mm, "mid": v(92.75, -1.34) * mm, "end": v(92.38, -1.22) * mm});
            skPoint(sketch, "E42.9.0.9", {"position": v(95.07, -1.22) * mm});
            skLineSegment(sketch, "E42.9.0.10", {"start": v(100.6, -1.22) * mm, "end": v(101.46, -1.22) * mm});
            skLineSegment(sketch, "E42.9.0.11", {"start": v(96.6, -1.22) * mm, "end": v(97.46, -1.22) * mm});
            skPoint(sketch, "E42.9.0.12", {"position": v(99.68, -2.5) * mm});
            skLineSegment(sketch, "E42.9.0.13", {"start": v(98.06, -1.65) * mm, "end": v(98.22, -2.07) * mm});
            skLineSegment(sketch, "E42.9.0.14", {"start": v(95.51, -1.22) * mm, "end": v(96.38, -1.22) * mm});
            skPoint(sketch, "E42.9.0.15", {"position": v(97.9, -1.22) * mm});
            skPoint(sketch, "E42.9.0.16", {"position": v(94.6, -2.5) * mm});
            skPoint(sketch, "E42.9.0.17", {"position": v(96.49, -1) * mm});
            skPoint(sketch, "E42.9.0.18", {"position": v(94.84, -1.86) * mm});
            skPoint(sketch, "E42.9.0.19", {"position": v(93.95, -2.5) * mm});
            skArc(sketch, "E42.9.0.20", {"start": v(98.22, -2.07) * mm, "mid": v(98.45, -2.38) * mm, "end": v(98.82, -2.5) * mm});
            skArc(sketch, "E42.9.0.21", {"start": v(93.14, -2.07) * mm, "mid": v(93.37, -2.38) * mm, "end": v(93.74, -2.5) * mm});
            skPoint(sketch, "E42.9.0.22", {"position": v(93.06, -1.86) * mm});
            skArc(sketch, "E42.9.0.23", {"start": v(95.51, -1.22) * mm, "mid": v(95.15, -1.34) * mm, "end": v(94.91, -1.65) * mm});
            skArc(sketch, "E42.9.0.24", {"start": v(99.24, -2.5) * mm, "mid": v(99.6, -2.38) * mm, "end": v(99.84, -2.07) * mm});
            skLineSegment(sketch, "E42.9.0.25", {"start": v(93.74, -2.5) * mm, "end": v(94.16, -2.5) * mm});
            skLineSegment(sketch, "E42.9.0.26", {"start": v(92.98, -1.65) * mm, "end": v(93.14, -2.07) * mm});
            skArc(sketch, "E42.9.0.27", {"start": v(100.6, -1.22) * mm, "mid": v(100.23, -1.34) * mm, "end": v(100, -1.65) * mm});
            skArc(sketch, "E42.9.0.28", {"start": v(94.16, -2.5) * mm, "mid": v(94.52, -2.38) * mm, "end": v(94.76, -2.07) * mm});
            skLineSegment(sketch, "E42.9.0.29", {"start": v(94.76, -2.07) * mm, "end": v(94.91, -1.65) * mm});
            skLineSegment(sketch, "E42.9.0.30", {"start": v(98.82, -2.5) * mm, "end": v(99.24, -2.5) * mm});
            skLineSegment(sketch, "E42.9.0.31", {"start": v(96.49, -1) * mm, "end": v(96.49, -1.3) * mm, "construction": true});
            skLineSegment(sketch, "E42.9.0.32", {"start": v(101.46, -1.22) * mm, "end": v(101.46, -1) * mm});
            skLineSegment(sketch, "E42.9.0.33", {"start": v(101.68, -1) * mm, "end": v(101.68, -1.22) * mm});
            skLineSegment(sketch, "E42.9.0.34", {"start": v(96.38, -1.22) * mm, "end": v(96.38, -1) * mm});
            skLineSegment(sketch, "E42.9.0.35", {"start": v(96.6, -1.11) * mm, "end": v(96.38, -1.11) * mm, "construction": true});
            skLineSegment(sketch, "E42.9.0.36", {"start": v(96.6, -1) * mm, "end": v(96.6, -1.22) * mm});
            skLineSegment(sketch, "E42.9.0.37", {"start": v(96.38, -1) * mm, "end": v(96.6, -1) * mm});
            skLineSegment(sketch, "E42.9.0.38", {"start": v(101.46, -1) * mm, "end": v(101.68, -1) * mm});
            skLineSegment(sketch, "E42.direction1", {"start": v(1.08, -1.91) * mm, "end": v(11.23, -1.9) * mm, "construction": true});
            skPoint(sketch, "E43.9.0.0", {"position": v(104.49, -2.05) * mm});
            skLineSegment(sketch, "E43.9.0.1", {"start": v(111.84, -1.21) * mm, "end": v(112.7, -1.21) * mm});
            skPoint(sketch, "E43.9.0.2", {"position": v(103.83, -2.05) * mm});
            skLineSegment(sketch, "E43.9.0.3", {"start": v(110, -2.07) * mm, "end": v(110.15, -1.65) * mm});
            skArc(sketch, "E43.9.0.4", {"start": v(108.22, -1.65) * mm, "mid": v(107.99, -1.34) * mm, "end": v(107.62, -1.22) * mm});
            skPoint(sketch, "E43.9.0.5", {"position": v(98.29, -0.78) * mm});
            skPoint(sketch, "E43.9.0.6", {"position": v(105.6, -0.78) * mm});
            skPoint(sketch, "E43.9.0.7", {"position": v(98.75, -2.05) * mm});
            skArc(sketch, "E43.9.0.8", {"start": v(103.14, -1.65) * mm, "mid": v(102.9, -1.34) * mm, "end": v(102.54, -1.22) * mm});
            skPoint(sketch, "E43.9.0.9", {"position": v(100.53, -0.78) * mm});
            skLineSegment(sketch, "E43.9.0.10", {"start": v(110.75, -1.22) * mm, "end": v(111.62, -1.22) * mm});
            skLineSegment(sketch, "E43.9.0.11", {"start": v(106.76, -1.22) * mm, "end": v(107.62, -1.22) * mm});
            skPoint(sketch, "E43.9.0.12", {"position": v(105.15, -2.05) * mm});
            skLineSegment(sketch, "E43.9.0.13", {"start": v(108.22, -1.65) * mm, "end": v(108.38, -2.07) * mm});
            skLineSegment(sketch, "E43.9.0.14", {"start": v(105.67, -1.22) * mm, "end": v(106.54, -1.22) * mm});
            skPoint(sketch, "E43.9.0.15", {"position": v(103.37, -0.78) * mm});
            skPoint(sketch, "E43.9.0.16", {"position": v(100.07, -2.05) * mm});
            skPoint(sketch, "E43.9.0.17", {"position": v(101.95, -0.56) * mm});
            skPoint(sketch, "E43.9.0.18", {"position": v(100.3, -1.42) * mm});
            skPoint(sketch, "E43.9.0.19", {"position": v(99.4, -2.05) * mm});
            skArc(sketch, "E43.9.0.20", {"start": v(108.38, -2.07) * mm, "mid": v(108.6, -2.38) * mm, "end": v(108.98, -2.5) * mm});
            skArc(sketch, "E43.9.0.21", {"start": v(103.3, -2.07) * mm, "mid": v(103.53, -2.38) * mm, "end": v(103.9, -2.5) * mm});
            skPoint(sketch, "E43.9.0.22", {"position": v(98.52, -1.42) * mm});
            skArc(sketch, "E43.9.0.23", {"start": v(105.67, -1.22) * mm, "mid": v(105.3, -1.34) * mm, "end": v(105.07, -1.65) * mm});
            skArc(sketch, "E43.9.0.24", {"start": v(109.4, -2.5) * mm, "mid": v(109.76, -2.38) * mm, "end": v(110, -2.07) * mm});
            skLineSegment(sketch, "E43.9.0.25", {"start": v(103.9, -2.5) * mm, "end": v(104.32, -2.5) * mm});
            skLineSegment(sketch, "E43.9.0.26", {"start": v(103.14, -1.65) * mm, "end": v(103.3, -2.07) * mm});
            skArc(sketch, "E43.9.0.27", {"start": v(110.75, -1.22) * mm, "mid": v(110.39, -1.34) * mm, "end": v(110.15, -1.65) * mm});
            skArc(sketch, "E43.9.0.28", {"start": v(104.32, -2.5) * mm, "mid": v(104.68, -2.38) * mm, "end": v(104.92, -2.07) * mm});
            skLineSegment(sketch, "E43.9.0.29", {"start": v(104.92, -2.07) * mm, "end": v(105.07, -1.65) * mm});
            skLineSegment(sketch, "E43.9.0.30", {"start": v(108.98, -2.5) * mm, "end": v(109.4, -2.5) * mm});
            skLineSegment(sketch, "E43.9.0.31", {"start": v(101.95, -0.56) * mm, "end": v(101.95, -0.85) * mm, "construction": true});
            skLineSegment(sketch, "E43.9.0.32", {"start": v(111.62, -1.22) * mm, "end": v(111.62, -1) * mm});
            skLineSegment(sketch, "E43.9.0.33", {"start": v(111.84, -1) * mm, "end": v(111.84, -1.21) * mm});
            skLineSegment(sketch, "E43.9.0.34", {"start": v(106.54, -1.22) * mm, "end": v(106.54, -1) * mm});
            skLineSegment(sketch, "E43.9.0.35", {"start": v(102.06, -0.67) * mm, "end": v(101.84, -0.67) * mm, "construction": true});
            skLineSegment(sketch, "E43.9.0.36", {"start": v(106.76, -1) * mm, "end": v(106.76, -1.22) * mm});
            skLineSegment(sketch, "E43.9.0.37", {"start": v(106.54, -1) * mm, "end": v(106.76, -1) * mm});
            skLineSegment(sketch, "E43.9.0.38", {"start": v(111.62, -1) * mm, "end": v(111.84, -1) * mm});
            skPoint(sketch, "E44.9.0.0", {"position": v(119.35, -2.48) * mm});
            skLineSegment(sketch, "E44.9.0.1", {"start": v(122, -1.24) * mm, "end": v(122.86, -1.24) * mm});
            skPoint(sketch, "E44.9.0.2", {"position": v(118.69, -2.48) * mm});
            skLineSegment(sketch, "E44.9.0.3", {"start": v(120.16, -2.06) * mm, "end": v(120.31, -1.64) * mm});
            skArc(sketch, "E44.9.0.4", {"start": v(118.38, -1.64) * mm, "mid": v(118.15, -1.33) * mm, "end": v(117.78, -1.21) * mm});
            skPoint(sketch, "E44.9.0.5", {"position": v(113.15, -1.21) * mm});
            skPoint(sketch, "E44.9.0.6", {"position": v(120.47, -1.21) * mm});
            skPoint(sketch, "E44.9.0.7", {"position": v(113.6, -2.48) * mm});
            skArc(sketch, "E44.9.0.8", {"start": v(113.3, -1.64) * mm, "mid": v(113.07, -1.33) * mm, "end": v(112.7, -1.21) * mm});
            skPoint(sketch, "E44.9.0.9", {"position": v(115.39, -1.21) * mm});
            skLineSegment(sketch, "E44.9.0.10", {"start": v(120.91, -1.21) * mm, "end": v(121.78, -1.21) * mm});
            skLineSegment(sketch, "E44.9.0.11", {"start": v(116.92, -1.21) * mm, "end": v(117.78, -1.21) * mm});
            skPoint(sketch, "E44.9.0.12", {"position": v(120, -2.48) * mm});
            skLineSegment(sketch, "E44.9.0.13", {"start": v(118.38, -1.64) * mm, "end": v(118.54, -2.06) * mm});
            skLineSegment(sketch, "E44.9.0.14", {"start": v(115.83, -1.21) * mm, "end": v(116.7, -1.21) * mm});
            skPoint(sketch, "E44.9.0.15", {"position": v(118.23, -1.21) * mm});
            skPoint(sketch, "E44.9.0.16", {"position": v(114.92, -2.48) * mm});
            skPoint(sketch, "E44.9.0.17", {"position": v(116.8, -1) * mm});
            skPoint(sketch, "E44.9.0.18", {"position": v(115.16, -1.85) * mm});
            skPoint(sketch, "E44.9.0.19", {"position": v(114.27, -2.48) * mm});
            skArc(sketch, "E44.9.0.20", {"start": v(118.54, -2.06) * mm, "mid": v(118.77, -2.37) * mm, "end": v(119.14, -2.48) * mm});
            skArc(sketch, "E44.9.0.21", {"start": v(113.46, -2.06) * mm, "mid": v(113.69, -2.37) * mm, "end": v(114.06, -2.48) * mm});
            skPoint(sketch, "E44.9.0.22", {"position": v(113.38, -1.85) * mm});
            skArc(sketch, "E44.9.0.23", {"start": v(115.83, -1.21) * mm, "mid": v(115.47, -1.33) * mm, "end": v(115.23, -1.64) * mm});
            skArc(sketch, "E44.9.0.24", {"start": v(119.56, -2.48) * mm, "mid": v(119.92, -2.37) * mm, "end": v(120.16, -2.06) * mm});
            skLineSegment(sketch, "E44.9.0.25", {"start": v(114.06, -2.48) * mm, "end": v(114.48, -2.48) * mm});
            skLineSegment(sketch, "E44.9.0.26", {"start": v(113.3, -1.64) * mm, "end": v(113.46, -2.06) * mm});
            skArc(sketch, "E44.9.0.27", {"start": v(120.91, -1.21) * mm, "mid": v(120.55, -1.33) * mm, "end": v(120.31, -1.64) * mm});
            skArc(sketch, "E44.9.0.28", {"start": v(114.48, -2.48) * mm, "mid": v(114.84, -2.37) * mm, "end": v(115.08, -2.06) * mm});
            skLineSegment(sketch, "E44.9.0.29", {"start": v(115.08, -2.06) * mm, "end": v(115.23, -1.64) * mm});
            skLineSegment(sketch, "E44.9.0.30", {"start": v(119.14, -2.48) * mm, "end": v(119.56, -2.48) * mm});
            skLineSegment(sketch, "E44.9.0.31", {"start": v(116.8, -1) * mm, "end": v(116.8, -1.28) * mm, "construction": true});
            skLineSegment(sketch, "E44.9.0.32", {"start": v(121.78, -1.21) * mm, "end": v(121.78, -1) * mm});
            skLineSegment(sketch, "E44.9.0.33", {"start": v(122, -1) * mm, "end": v(122, -1.24) * mm});
            skLineSegment(sketch, "E44.9.0.34", {"start": v(116.7, -1.21) * mm, "end": v(116.7, -1) * mm});
            skLineSegment(sketch, "E44.9.0.35", {"start": v(116.92, -1.1) * mm, "end": v(116.7, -1.1) * mm, "construction": true});
            skLineSegment(sketch, "E44.9.0.36", {"start": v(116.92, -1) * mm, "end": v(116.92, -1.21) * mm});
            skLineSegment(sketch, "E44.9.0.37", {"start": v(116.7, -1) * mm, "end": v(116.92, -1) * mm});
            skLineSegment(sketch, "E44.9.0.38", {"start": v(121.78, -1) * mm, "end": v(122, -1) * mm});
            skPoint(sketch, "E45.9.0.0", {"position": v(129.5, -2.5) * mm});
            skLineSegment(sketch, "E45.9.0.1", {"start": v(132.16, -1.24) * mm, "end": v(133.02, -1.24) * mm});
            skPoint(sketch, "E45.9.0.2", {"position": v(128.85, -2.5) * mm});
            skLineSegment(sketch, "E45.9.0.3", {"start": v(130.32, -2.09) * mm, "end": v(130.47, -1.66) * mm});
            skArc(sketch, "E45.9.0.4", {"start": v(128.54, -1.66) * mm, "mid": v(128.3, -1.36) * mm, "end": v(127.94, -1.24) * mm});
            skPoint(sketch, "E45.9.0.5", {"position": v(123.3, -1.24) * mm});
            skPoint(sketch, "E45.9.0.6", {"position": v(130.63, -1.24) * mm});
            skPoint(sketch, "E45.9.0.7", {"position": v(123.77, -2.5) * mm});
            skArc(sketch, "E45.9.0.8", {"start": v(123.46, -1.66) * mm, "mid": v(123.23, -1.36) * mm, "end": v(122.86, -1.24) * mm});
            skPoint(sketch, "E45.9.0.9", {"position": v(125.55, -1.24) * mm});
            skLineSegment(sketch, "E45.9.0.10", {"start": v(131.07, -1.24) * mm, "end": v(131.94, -1.24) * mm});
            skLineSegment(sketch, "E45.9.0.11", {"start": v(127.08, -1.24) * mm, "end": v(127.94, -1.24) * mm});
            skPoint(sketch, "E45.9.0.12", {"position": v(130.16, -2.5) * mm});
            skLineSegment(sketch, "E45.9.0.13", {"start": v(128.54, -1.66) * mm, "end": v(128.7, -2.09) * mm});
            skLineSegment(sketch, "E45.9.0.14", {"start": v(126, -1.24) * mm, "end": v(126.86, -1.24) * mm});
            skPoint(sketch, "E45.9.0.15", {"position": v(128.39, -1.24) * mm});
            skPoint(sketch, "E45.9.0.16", {"position": v(125.08, -2.5) * mm});
            skPoint(sketch, "E45.9.0.17", {"position": v(126.97, -1.02) * mm});
            skPoint(sketch, "E45.9.0.18", {"position": v(125.32, -1.87) * mm});
            skPoint(sketch, "E45.9.0.19", {"position": v(124.43, -2.5) * mm});
            skArc(sketch, "E45.9.0.20", {"start": v(128.7, -2.09) * mm, "mid": v(128.93, -2.4) * mm, "end": v(129.3, -2.5) * mm});
            skArc(sketch, "E45.9.0.21", {"start": v(123.62, -2.09) * mm, "mid": v(123.85, -2.4) * mm, "end": v(124.22, -2.5) * mm});
            skPoint(sketch, "E45.9.0.22", {"position": v(123.54, -1.87) * mm});
            skArc(sketch, "E45.9.0.23", {"start": v(126, -1.24) * mm, "mid": v(125.63, -1.36) * mm, "end": v(125.4, -1.66) * mm});
            skArc(sketch, "E45.9.0.24", {"start": v(129.72, -2.5) * mm, "mid": v(130.08, -2.4) * mm, "end": v(130.32, -2.09) * mm});
            skLineSegment(sketch, "E45.9.0.25", {"start": v(124.22, -2.5) * mm, "end": v(124.64, -2.5) * mm});
            skLineSegment(sketch, "E45.9.0.26", {"start": v(123.46, -1.66) * mm, "end": v(123.62, -2.09) * mm});
            skArc(sketch, "E45.9.0.27", {"start": v(131.07, -1.24) * mm, "mid": v(130.7, -1.36) * mm, "end": v(130.47, -1.66) * mm});
            skArc(sketch, "E45.9.0.28", {"start": v(124.64, -2.5) * mm, "mid": v(125, -2.4) * mm, "end": v(125.24, -2.09) * mm});
            skLineSegment(sketch, "E45.9.0.29", {"start": v(125.24, -2.09) * mm, "end": v(125.4, -1.66) * mm});
            skLineSegment(sketch, "E45.9.0.30", {"start": v(129.3, -2.5) * mm, "end": v(129.72, -2.5) * mm});
            skLineSegment(sketch, "E45.9.0.31", {"start": v(126.97, -1.02) * mm, "end": v(126.97, -1.3) * mm, "construction": true});
            skLineSegment(sketch, "E45.9.0.32", {"start": v(131.94, -1.24) * mm, "end": v(131.94, -1.02) * mm});
            skLineSegment(sketch, "E45.9.0.33", {"start": v(132.16, -1.02) * mm, "end": v(132.16, -1.24) * mm});
            skLineSegment(sketch, "E45.9.0.34", {"start": v(126.86, -1.24) * mm, "end": v(126.86, -1.02) * mm});
            skLineSegment(sketch, "E45.9.0.35", {"start": v(127.08, -1.13) * mm, "end": v(126.86, -1.13) * mm, "construction": true});
            skLineSegment(sketch, "E45.9.0.36", {"start": v(127.08, -1.02) * mm, "end": v(127.08, -1.24) * mm});
            skLineSegment(sketch, "E45.9.0.37", {"start": v(126.86, -1.02) * mm, "end": v(127.08, -1.02) * mm});
            skLineSegment(sketch, "E45.9.0.38", {"start": v(131.94, -1.02) * mm, "end": v(132.16, -1.02) * mm});
            skPoint(sketch, "E46.9.0.0", {"position": v(139.67, -2.48) * mm});
            skLineSegment(sketch, "E46.9.0.1", {"start": v(142.32, -1.24) * mm, "end": v(143.18, -1.24) * mm});
            skPoint(sketch, "E46.9.0.2", {"position": v(139.01, -2.48) * mm});
            skLineSegment(sketch, "E46.9.0.3", {"start": v(140.48, -2.09) * mm, "end": v(140.63, -1.66) * mm});
            skArc(sketch, "E46.9.0.4", {"start": v(138.7, -1.66) * mm, "mid": v(138.47, -1.36) * mm, "end": v(138.1, -1.24) * mm});
            skPoint(sketch, "E46.9.0.5", {"position": v(133.47, -1.21) * mm});
            skPoint(sketch, "E46.9.0.6", {"position": v(140.8, -1.21) * mm});
            skPoint(sketch, "E46.9.0.7", {"position": v(133.93, -2.48) * mm});
            skArc(sketch, "E46.9.0.8", {"start": v(133.62, -1.66) * mm, "mid": v(133.39, -1.36) * mm, "end": v(133.02, -1.24) * mm});
            skPoint(sketch, "E46.9.0.9", {"position": v(135.71, -1.21) * mm});
            skLineSegment(sketch, "E46.9.0.10", {"start": v(141.23, -1.24) * mm, "end": v(142.1, -1.24) * mm});
            skLineSegment(sketch, "E46.9.0.11", {"start": v(137.24, -1.24) * mm, "end": v(138.1, -1.24) * mm});
            skPoint(sketch, "E46.9.0.12", {"position": v(140.33, -2.48) * mm});
            skLineSegment(sketch, "E46.9.0.13", {"start": v(138.7, -1.66) * mm, "end": v(138.86, -2.09) * mm});
            skLineSegment(sketch, "E46.9.0.14", {"start": v(136.15, -1.24) * mm, "end": v(137.02, -1.24) * mm});
            skPoint(sketch, "E46.9.0.15", {"position": v(138.55, -1.21) * mm});
            skPoint(sketch, "E46.9.0.16", {"position": v(135.25, -2.48) * mm});
            skPoint(sketch, "E46.9.0.17", {"position": v(137.13, -1) * mm});
            skPoint(sketch, "E46.9.0.18", {"position": v(135.48, -1.85) * mm});
            skPoint(sketch, "E46.9.0.19", {"position": v(134.6, -2.48) * mm});
            skArc(sketch, "E46.9.0.20", {"start": v(138.86, -2.09) * mm, "mid": v(139.09, -2.4) * mm, "end": v(139.46, -2.5) * mm});
            skArc(sketch, "E46.9.0.21", {"start": v(133.78, -2.09) * mm, "mid": v(134, -2.4) * mm, "end": v(134.38, -2.5) * mm});
            skPoint(sketch, "E46.9.0.22", {"position": v(133.7, -1.85) * mm});
            skArc(sketch, "E46.9.0.23", {"start": v(136.15, -1.24) * mm, "mid": v(135.79, -1.36) * mm, "end": v(135.55, -1.66) * mm});
            skArc(sketch, "E46.9.0.24", {"start": v(139.88, -2.5) * mm, "mid": v(140.24, -2.4) * mm, "end": v(140.48, -2.09) * mm});
            skLineSegment(sketch, "E46.9.0.25", {"start": v(134.38, -2.5) * mm, "end": v(134.8, -2.5) * mm});
            skLineSegment(sketch, "E46.9.0.26", {"start": v(133.62, -1.66) * mm, "end": v(133.78, -2.09) * mm});
            skArc(sketch, "E46.9.0.27", {"start": v(141.23, -1.24) * mm, "mid": v(140.87, -1.36) * mm, "end": v(140.63, -1.66) * mm});
            skArc(sketch, "E46.9.0.28", {"start": v(134.8, -2.5) * mm, "mid": v(135.16, -2.4) * mm, "end": v(135.4, -2.09) * mm});
            skLineSegment(sketch, "E46.9.0.29", {"start": v(135.4, -2.09) * mm, "end": v(135.55, -1.66) * mm});
            skLineSegment(sketch, "E46.9.0.30", {"start": v(139.46, -2.5) * mm, "end": v(139.88, -2.5) * mm});
            skLineSegment(sketch, "E46.9.0.31", {"start": v(137.13, -1) * mm, "end": v(137.13, -1.28) * mm, "construction": true});
            skLineSegment(sketch, "E46.9.0.32", {"start": v(142.1, -1.24) * mm, "end": v(142.1, -1.02) * mm});
            skLineSegment(sketch, "E46.9.0.33", {"start": v(142.32, -1.02) * mm, "end": v(142.32, -1.24) * mm});
            skLineSegment(sketch, "E46.9.0.34", {"start": v(137.02, -1.24) * mm, "end": v(137.02, -1.02) * mm});
            skLineSegment(sketch, "E46.9.0.35", {"start": v(137.24, -1.1) * mm, "end": v(137.02, -1.1) * mm, "construction": true});
            skLineSegment(sketch, "E46.9.0.36", {"start": v(137.24, -1.02) * mm, "end": v(137.24, -1.24) * mm});
            skLineSegment(sketch, "E46.9.0.37", {"start": v(137.02, -1.02) * mm, "end": v(137.24, -1.02) * mm});
            skLineSegment(sketch, "E46.9.0.38", {"start": v(142.1, -1.02) * mm, "end": v(142.32, -1.02) * mm});
            skPoint(sketch, "E47.9.0.0", {"position": v(145.17, -2.04) * mm});
            skLineSegment(sketch, "E47.9.0.1", {"start": v(152.48, -1.24) * mm, "end": v(153.34, -1.24) * mm});
            skPoint(sketch, "E47.9.0.2", {"position": v(144.51, -2.04) * mm});
            skLineSegment(sketch, "E47.9.0.3", {"start": v(150.64, -2.09) * mm, "end": v(150.8, -1.66) * mm});
            skArc(sketch, "E47.9.0.4", {"start": v(148.86, -1.66) * mm, "mid": v(148.63, -1.36) * mm, "end": v(148.26, -1.24) * mm});
            skPoint(sketch, "E47.9.0.5", {"position": v(138.97, -0.77) * mm});
            skPoint(sketch, "E47.9.0.6", {"position": v(146.3, -0.77) * mm});
            skPoint(sketch, "E47.9.0.7", {"position": v(139.43, -2.04) * mm});
            skArc(sketch, "E47.9.0.8", {"start": v(143.78, -1.66) * mm, "mid": v(143.55, -1.36) * mm, "end": v(143.18, -1.24) * mm});
            skPoint(sketch, "E47.9.0.9", {"position": v(141.21, -0.77) * mm});
            skLineSegment(sketch, "E47.9.0.10", {"start": v(151.4, -1.24) * mm, "end": v(152.26, -1.24) * mm});
            skLineSegment(sketch, "E47.9.0.11", {"start": v(147.4, -1.24) * mm, "end": v(148.26, -1.24) * mm});
            skPoint(sketch, "E47.9.0.12", {"position": v(145.83, -2.04) * mm});
            skLineSegment(sketch, "E47.9.0.13", {"start": v(148.86, -1.66) * mm, "end": v(149.02, -2.09) * mm});
            skLineSegment(sketch, "E47.9.0.14", {"start": v(146.31, -1.24) * mm, "end": v(147.18, -1.24) * mm});
            skPoint(sketch, "E47.9.0.15", {"position": v(144.05, -0.77) * mm});
            skPoint(sketch, "E47.9.0.16", {"position": v(140.75, -2.04) * mm});
            skPoint(sketch, "E47.9.0.17", {"position": v(142.63, -0.55) * mm});
            skPoint(sketch, "E47.9.0.18", {"position": v(140.98, -1.4) * mm});
            skPoint(sketch, "E47.9.0.19", {"position": v(140.1, -2.04) * mm});
            skArc(sketch, "E47.9.0.20", {"start": v(149.02, -2.09) * mm, "mid": v(149.25, -2.4) * mm, "end": v(149.62, -2.5) * mm});
            skArc(sketch, "E47.9.0.21", {"start": v(143.94, -2.09) * mm, "mid": v(144.17, -2.4) * mm, "end": v(144.54, -2.5) * mm});
            skPoint(sketch, "E47.9.0.22", {"position": v(139.2, -1.4) * mm});
            skArc(sketch, "E47.9.0.23", {"start": v(146.31, -1.24) * mm, "mid": v(145.95, -1.36) * mm, "end": v(145.71, -1.66) * mm});
            skArc(sketch, "E47.9.0.24", {"start": v(150.04, -2.5) * mm, "mid": v(150.4, -2.4) * mm, "end": v(150.64, -2.09) * mm});
            skLineSegment(sketch, "E47.9.0.25", {"start": v(144.54, -2.5) * mm, "end": v(144.96, -2.5) * mm});
            skLineSegment(sketch, "E47.9.0.26", {"start": v(143.78, -1.66) * mm, "end": v(143.94, -2.09) * mm});
            skArc(sketch, "E47.9.0.27", {"start": v(151.4, -1.24) * mm, "mid": v(151.03, -1.36) * mm, "end": v(150.8, -1.66) * mm});
            skArc(sketch, "E47.9.0.28", {"start": v(144.96, -2.5) * mm, "mid": v(145.32, -2.4) * mm, "end": v(145.56, -2.09) * mm});
            skLineSegment(sketch, "E47.9.0.29", {"start": v(145.56, -2.09) * mm, "end": v(145.71, -1.66) * mm});
            skLineSegment(sketch, "E47.9.0.30", {"start": v(149.62, -2.5) * mm, "end": v(150.04, -2.5) * mm});
            skLineSegment(sketch, "E47.9.0.31", {"start": v(142.63, -0.55) * mm, "end": v(142.63, -0.83) * mm, "construction": true});
            skLineSegment(sketch, "E47.9.0.32", {"start": v(152.26, -1.24) * mm, "end": v(152.26, -1.02) * mm});
            skLineSegment(sketch, "E47.9.0.33", {"start": v(152.48, -1.02) * mm, "end": v(152.48, -1.24) * mm});
            skLineSegment(sketch, "E47.9.0.34", {"start": v(147.18, -1.24) * mm, "end": v(147.18, -1.02) * mm});
            skLineSegment(sketch, "E47.9.0.35", {"start": v(142.74, -0.66) * mm, "end": v(142.52, -0.66) * mm, "construction": true});
            skLineSegment(sketch, "E47.9.0.36", {"start": v(147.4, -1.02) * mm, "end": v(147.4, -1.24) * mm});
            skLineSegment(sketch, "E47.9.0.37", {"start": v(147.18, -1.02) * mm, "end": v(147.4, -1.02) * mm});
            skLineSegment(sketch, "E47.9.0.38", {"start": v(152.26, -1.02) * mm, "end": v(152.48, -1.02) * mm});
            skPoint(sketch, "E48.9.0.0", {"position": v(155.55, -2.03) * mm});
            skLineSegment(sketch, "E48.9.0.1", {"start": v(162.64, -1.24) * mm, "end": v(163.5, -1.24) * mm});
            skPoint(sketch, "E48.9.0.2", {"position": v(154.9, -2.03) * mm});
            skLineSegment(sketch, "E48.9.0.3", {"start": v(160.8, -2.09) * mm, "end": v(160.95, -1.66) * mm});
            skArc(sketch, "E48.9.0.4", {"start": v(159.02, -1.66) * mm, "mid": v(158.79, -1.36) * mm, "end": v(158.42, -1.24) * mm});
            skPoint(sketch, "E48.9.0.5", {"position": v(149.35, -0.76) * mm});
            skPoint(sketch, "E48.9.0.6", {"position": v(156.67, -0.76) * mm});
            skPoint(sketch, "E48.9.0.7", {"position": v(149.81, -2.03) * mm});
            skArc(sketch, "E48.9.0.8", {"start": v(153.94, -1.66) * mm, "mid": v(153.7, -1.36) * mm, "end": v(153.34, -1.24) * mm});
            skPoint(sketch, "E48.9.0.9", {"position": v(151.6, -0.76) * mm});
            skLineSegment(sketch, "E48.9.0.10", {"start": v(161.55, -1.24) * mm, "end": v(162.42, -1.24) * mm});
            skLineSegment(sketch, "E48.9.0.11", {"start": v(157.56, -1.24) * mm, "end": v(158.42, -1.24) * mm});
            skPoint(sketch, "E48.9.0.12", {"position": v(156.2, -2.03) * mm});
            skLineSegment(sketch, "E48.9.0.13", {"start": v(159.02, -1.66) * mm, "end": v(159.18, -2.09) * mm});
            skLineSegment(sketch, "E48.9.0.14", {"start": v(156.47, -1.24) * mm, "end": v(157.34, -1.24) * mm});
            skPoint(sketch, "E48.9.0.15", {"position": v(154.43, -0.76) * mm});
            skPoint(sketch, "E48.9.0.16", {"position": v(151.13, -2.03) * mm});
            skPoint(sketch, "E48.9.0.17", {"position": v(153.01, -0.54) * mm});
            skPoint(sketch, "E48.9.0.18", {"position": v(151.36, -1.4) * mm});
            skPoint(sketch, "E48.9.0.19", {"position": v(150.47, -2.03) * mm});
            skArc(sketch, "E48.9.0.20", {"start": v(159.18, -2.09) * mm, "mid": v(159.4, -2.4) * mm, "end": v(159.78, -2.5) * mm});
            skArc(sketch, "E48.9.0.21", {"start": v(154.1, -2.09) * mm, "mid": v(154.33, -2.4) * mm, "end": v(154.7, -2.5) * mm});
            skPoint(sketch, "E48.9.0.22", {"position": v(149.58, -1.4) * mm});
            skArc(sketch, "E48.9.0.23", {"start": v(156.47, -1.24) * mm, "mid": v(156.1, -1.36) * mm, "end": v(155.87, -1.66) * mm});
            skArc(sketch, "E48.9.0.24", {"start": v(160.2, -2.5) * mm, "mid": v(160.56, -2.4) * mm, "end": v(160.8, -2.09) * mm});
            skLineSegment(sketch, "E48.9.0.25", {"start": v(154.7, -2.5) * mm, "end": v(155.12, -2.5) * mm});
            skLineSegment(sketch, "E48.9.0.26", {"start": v(153.94, -1.66) * mm, "end": v(154.1, -2.09) * mm});
            skArc(sketch, "E48.9.0.27", {"start": v(161.55, -1.24) * mm, "mid": v(161.19, -1.36) * mm, "end": v(160.95, -1.66) * mm});
            skArc(sketch, "E48.9.0.28", {"start": v(155.12, -2.5) * mm, "mid": v(155.48, -2.4) * mm, "end": v(155.72, -2.09) * mm});
            skLineSegment(sketch, "E48.9.0.29", {"start": v(155.72, -2.09) * mm, "end": v(155.87, -1.66) * mm});
            skLineSegment(sketch, "E48.9.0.30", {"start": v(159.78, -2.5) * mm, "end": v(160.2, -2.5) * mm});
            skLineSegment(sketch, "E48.9.0.31", {"start": v(153.01, -0.54) * mm, "end": v(153.01, -0.83) * mm, "construction": true});
            skLineSegment(sketch, "E48.9.0.32", {"start": v(162.42, -1.24) * mm, "end": v(162.42, -1.02) * mm});
            skLineSegment(sketch, "E48.9.0.33", {"start": v(162.64, -1.02) * mm, "end": v(162.64, -1.24) * mm});
            skLineSegment(sketch, "E48.9.0.34", {"start": v(157.34, -1.24) * mm, "end": v(157.34, -1.02) * mm});
            skLineSegment(sketch, "E48.9.0.35", {"start": v(153.12, -0.65) * mm, "end": v(152.9, -0.65) * mm, "construction": true});
            skLineSegment(sketch, "E48.9.0.36", {"start": v(157.56, -1.02) * mm, "end": v(157.56, -1.24) * mm});
            skLineSegment(sketch, "E48.9.0.37", {"start": v(157.34, -1.02) * mm, "end": v(157.56, -1.02) * mm});
            skLineSegment(sketch, "E48.9.0.38", {"start": v(162.42, -1.02) * mm, "end": v(162.64, -1.02) * mm});
            skPoint(sketch, "E49.9.0.0", {"position": v(165.35, -2.6) * mm});
            skLineSegment(sketch, "E49.9.0.1", {"start": v(172.8, -1.24) * mm, "end": v(173.66, -1.24) * mm});
            skPoint(sketch, "E49.9.0.2", {"position": v(164.7, -2.6) * mm});
            skLineSegment(sketch, "E49.9.0.3", {"start": v(170.96, -2.09) * mm, "end": v(171.11, -1.66) * mm});
            skArc(sketch, "E49.9.0.4", {"start": v(169.18, -1.66) * mm, "mid": v(168.95, -1.36) * mm, "end": v(168.58, -1.24) * mm});
            skPoint(sketch, "E49.9.0.5", {"position": v(159.15, -1.32) * mm});
            skPoint(sketch, "E49.9.0.6", {"position": v(166.47, -1.32) * mm});
            skPoint(sketch, "E49.9.0.7", {"position": v(159.61, -2.6) * mm});
            skArc(sketch, "E49.9.0.8", {"start": v(164.1, -1.66) * mm, "mid": v(163.87, -1.36) * mm, "end": v(163.5, -1.24) * mm});
            skPoint(sketch, "E49.9.0.9", {"position": v(161.4, -1.32) * mm});
            skLineSegment(sketch, "E49.9.0.10", {"start": v(171.71, -1.24) * mm, "end": v(172.58, -1.24) * mm});
            skLineSegment(sketch, "E49.9.0.11", {"start": v(167.72, -1.24) * mm, "end": v(168.58, -1.24) * mm});
            skPoint(sketch, "E49.9.0.12", {"position": v(166, -2.6) * mm});
            skLineSegment(sketch, "E49.9.0.13", {"start": v(169.18, -1.66) * mm, "end": v(169.34, -2.09) * mm});
            skLineSegment(sketch, "E49.9.0.14", {"start": v(166.63, -1.24) * mm, "end": v(167.5, -1.24) * mm});
            skPoint(sketch, "E49.9.0.15", {"position": v(164.23, -1.32) * mm});
            skPoint(sketch, "E49.9.0.16", {"position": v(160.93, -2.6) * mm});
            skPoint(sketch, "E49.9.0.17", {"position": v(162.81, -1.1) * mm});
            skPoint(sketch, "E49.9.0.18", {"position": v(161.16, -1.96) * mm});
            skPoint(sketch, "E49.9.0.19", {"position": v(160.27, -2.6) * mm});
            skArc(sketch, "E49.9.0.20", {"start": v(169.34, -2.09) * mm, "mid": v(169.57, -2.4) * mm, "end": v(169.94, -2.5) * mm});
            skArc(sketch, "E49.9.0.21", {"start": v(164.26, -2.09) * mm, "mid": v(164.49, -2.4) * mm, "end": v(164.86, -2.5) * mm});
            skPoint(sketch, "E49.9.0.22", {"position": v(159.38, -1.96) * mm});
            skArc(sketch, "E49.9.0.23", {"start": v(166.63, -1.24) * mm, "mid": v(166.27, -1.36) * mm, "end": v(166.03, -1.66) * mm});
            skArc(sketch, "E49.9.0.24", {"start": v(170.36, -2.5) * mm, "mid": v(170.72, -2.4) * mm, "end": v(170.96, -2.09) * mm});
            skLineSegment(sketch, "E49.9.0.25", {"start": v(164.86, -2.5) * mm, "end": v(165.28, -2.5) * mm});
            skLineSegment(sketch, "E49.9.0.26", {"start": v(164.1, -1.66) * mm, "end": v(164.26, -2.09) * mm});
            skArc(sketch, "E49.9.0.27", {"start": v(171.71, -1.24) * mm, "mid": v(171.35, -1.36) * mm, "end": v(171.11, -1.66) * mm});
            skArc(sketch, "E49.9.0.28", {"start": v(165.28, -2.5) * mm, "mid": v(165.64, -2.4) * mm, "end": v(165.88, -2.09) * mm});
            skLineSegment(sketch, "E49.9.0.29", {"start": v(165.88, -2.09) * mm, "end": v(166.03, -1.66) * mm});
            skLineSegment(sketch, "E49.9.0.30", {"start": v(169.94, -2.5) * mm, "end": v(170.36, -2.5) * mm});
            skLineSegment(sketch, "E49.9.0.31", {"start": v(162.81, -1.1) * mm, "end": v(162.81, -1.39) * mm, "construction": true});
            skLineSegment(sketch, "E49.9.0.32", {"start": v(172.58, -1.24) * mm, "end": v(172.58, -1.02) * mm});
            skLineSegment(sketch, "E49.9.0.33", {"start": v(172.8, -1.02) * mm, "end": v(172.8, -1.24) * mm});
            skLineSegment(sketch, "E49.9.0.34", {"start": v(167.5, -1.24) * mm, "end": v(167.5, -1.02) * mm});
            skLineSegment(sketch, "E49.9.0.35", {"start": v(162.92, -1.2) * mm, "end": v(162.7, -1.2) * mm, "construction": true});
            skLineSegment(sketch, "E49.9.0.36", {"start": v(167.72, -1.02) * mm, "end": v(167.72, -1.24) * mm});
            skLineSegment(sketch, "E49.9.0.37", {"start": v(167.5, -1.02) * mm, "end": v(167.72, -1.02) * mm});
            skLineSegment(sketch, "E49.9.0.38", {"start": v(172.58, -1.02) * mm, "end": v(172.8, -1.02) * mm});
            skPoint(sketch, "E50.9.0.0", {"position": v(181, -6.1) * mm});
            skLineSegment(sketch, "E50.9.0.1", {"start": v(182.96, -1.24) * mm, "end": v(183.82, -1.24) * mm});
            skPoint(sketch, "E50.9.0.2", {"position": v(180.35, -6.1) * mm});
            skLineSegment(sketch, "E50.9.0.3", {"start": v(181.12, -2.09) * mm, "end": v(181.27, -1.66) * mm});
            skArc(sketch, "E50.9.0.4", {"start": v(179.34, -1.66) * mm, "mid": v(179.1, -1.36) * mm, "end": v(178.74, -1.24) * mm});
            skPoint(sketch, "E50.9.0.5", {"position": v(174.8, -4.82) * mm});
            skPoint(sketch, "E50.9.0.6", {"position": v(182.13, -4.82) * mm});
            skPoint(sketch, "E50.9.0.7", {"position": v(175.27, -6.1) * mm});
            skArc(sketch, "E50.9.0.8", {"start": v(174.26, -1.66) * mm, "mid": v(174.03, -1.36) * mm, "end": v(173.66, -1.24) * mm});
            skPoint(sketch, "E50.9.0.9", {"position": v(177.05, -4.82) * mm});
            skLineSegment(sketch, "E50.9.0.10", {"start": v(181.87, -1.24) * mm, "end": v(182.74, -1.24) * mm});
            skLineSegment(sketch, "E50.9.0.11", {"start": v(177.88, -1.24) * mm, "end": v(178.74, -1.24) * mm});
            skPoint(sketch, "E50.9.0.12", {"position": v(181.67, -6.1) * mm});
            skLineSegment(sketch, "E50.9.0.13", {"start": v(179.34, -1.66) * mm, "end": v(179.5, -2.09) * mm});
            skLineSegment(sketch, "E50.9.0.14", {"start": v(176.8, -1.24) * mm, "end": v(177.66, -1.24) * mm});
            skPoint(sketch, "E50.9.0.15", {"position": v(179.89, -4.82) * mm});
            skPoint(sketch, "E50.9.0.16", {"position": v(176.59, -6.1) * mm});
            skPoint(sketch, "E50.9.0.17", {"position": v(178.47, -4.6) * mm});
            skPoint(sketch, "E50.9.0.18", {"position": v(176.82, -5.46) * mm});
            skPoint(sketch, "E50.9.0.19", {"position": v(175.93, -6.1) * mm});
            skArc(sketch, "E50.9.0.20", {"start": v(179.5, -2.09) * mm, "mid": v(179.73, -2.4) * mm, "end": v(180.1, -2.5) * mm});
            skArc(sketch, "E50.9.0.21", {"start": v(174.42, -2.09) * mm, "mid": v(174.65, -2.4) * mm, "end": v(175.02, -2.5) * mm});
            skPoint(sketch, "E50.9.0.22", {"position": v(175.04, -5.46) * mm});
            skArc(sketch, "E50.9.0.23", {"start": v(176.8, -1.24) * mm, "mid": v(176.43, -1.36) * mm, "end": v(176.2, -1.66) * mm});
            skArc(sketch, "E50.9.0.24", {"start": v(180.52, -2.5) * mm, "mid": v(180.88, -2.4) * mm, "end": v(181.12, -2.09) * mm});
            skLineSegment(sketch, "E50.9.0.25", {"start": v(175.02, -2.5) * mm, "end": v(175.44, -2.5) * mm});
            skLineSegment(sketch, "E50.9.0.26", {"start": v(174.26, -1.66) * mm, "end": v(174.42, -2.09) * mm});
            skArc(sketch, "E50.9.0.27", {"start": v(181.87, -1.24) * mm, "mid": v(181.5, -1.36) * mm, "end": v(181.27, -1.66) * mm});
            skArc(sketch, "E50.9.0.28", {"start": v(175.44, -2.5) * mm, "mid": v(175.8, -2.4) * mm, "end": v(176.04, -2.09) * mm});
            skLineSegment(sketch, "E50.9.0.29", {"start": v(176.04, -2.09) * mm, "end": v(176.2, -1.66) * mm});
            skLineSegment(sketch, "E50.9.0.30", {"start": v(180.1, -2.5) * mm, "end": v(180.52, -2.5) * mm});
            skLineSegment(sketch, "E50.9.0.31", {"start": v(178.47, -4.6) * mm, "end": v(178.47, -4.9) * mm, "construction": true});
            skLineSegment(sketch, "E50.9.0.32", {"start": v(182.74, -1.24) * mm, "end": v(182.74, -1.02) * mm});
            skLineSegment(sketch, "E50.9.0.33", {"start": v(182.96, -1.02) * mm, "end": v(182.96, -1.24) * mm});
            skLineSegment(sketch, "E50.9.0.34", {"start": v(177.66, -1.24) * mm, "end": v(177.66, -1.02) * mm});
            skLineSegment(sketch, "E50.9.0.35", {"start": v(178.58, -4.71) * mm, "end": v(178.36, -4.71) * mm, "construction": true});
            skLineSegment(sketch, "E50.9.0.36", {"start": v(177.88, -1.02) * mm, "end": v(177.88, -1.24) * mm});
            skLineSegment(sketch, "E50.9.0.37", {"start": v(177.66, -1.02) * mm, "end": v(177.88, -1.02) * mm});
            skLineSegment(sketch, "E50.9.0.38", {"start": v(182.74, -1.02) * mm, "end": v(182.96, -1.02) * mm});
            skPoint(sketch, "E51.9.0.0", {"position": v(191.09, -4.54) * mm});
            skLineSegment(sketch, "E51.9.0.1", {"start": v(193.12, -1.24) * mm, "end": v(193.98, -1.24) * mm});
            skPoint(sketch, "E51.9.0.2", {"position": v(190.43, -4.54) * mm});
            skLineSegment(sketch, "E51.9.0.3", {"start": v(191.28, -2.09) * mm, "end": v(191.43, -1.66) * mm});
            skArc(sketch, "E51.9.0.4", {"start": v(189.5, -1.66) * mm, "mid": v(189.27, -1.36) * mm, "end": v(188.9, -1.24) * mm});
            skPoint(sketch, "E51.9.0.5", {"position": v(184.89, -3.27) * mm});
            skPoint(sketch, "E51.9.0.6", {"position": v(192.2, -3.27) * mm});
            skPoint(sketch, "E51.9.0.7", {"position": v(185.35, -4.54) * mm});
            skArc(sketch, "E51.9.0.8", {"start": v(184.42, -1.66) * mm, "mid": v(184.19, -1.36) * mm, "end": v(183.82, -1.24) * mm});
            skPoint(sketch, "E51.9.0.9", {"position": v(187.13, -3.27) * mm});
            skLineSegment(sketch, "E51.9.0.10", {"start": v(192.03, -1.24) * mm, "end": v(192.9, -1.24) * mm});
            skLineSegment(sketch, "E51.9.0.11", {"start": v(188.04, -1.24) * mm, "end": v(188.9, -1.24) * mm});
            skPoint(sketch, "E51.9.0.12", {"position": v(191.74, -4.54) * mm});
            skLineSegment(sketch, "E51.9.0.13", {"start": v(189.5, -1.66) * mm, "end": v(189.66, -2.09) * mm});
            skLineSegment(sketch, "E51.9.0.14", {"start": v(186.95, -1.24) * mm, "end": v(187.82, -1.24) * mm});
            skPoint(sketch, "E51.9.0.15", {"position": v(189.97, -3.27) * mm});
            skPoint(sketch, "E51.9.0.16", {"position": v(186.66, -4.54) * mm});
            skPoint(sketch, "E51.9.0.17", {"position": v(188.55, -3.05) * mm});
            skPoint(sketch, "E51.9.0.18", {"position": v(186.9, -3.9) * mm});
            skPoint(sketch, "E51.9.0.19", {"position": v(186, -4.54) * mm});
            skArc(sketch, "E51.9.0.20", {"start": v(189.66, -2.09) * mm, "mid": v(189.89, -2.4) * mm, "end": v(190.26, -2.5) * mm});
            skArc(sketch, "E51.9.0.21", {"start": v(184.58, -2.09) * mm, "mid": v(184.8, -2.4) * mm, "end": v(185.18, -2.5) * mm});
            skPoint(sketch, "E51.9.0.22", {"position": v(185.12, -3.9) * mm});
            skArc(sketch, "E51.9.0.23", {"start": v(186.95, -1.24) * mm, "mid": v(186.59, -1.36) * mm, "end": v(186.35, -1.66) * mm});
            skArc(sketch, "E51.9.0.24", {"start": v(190.68, -2.5) * mm, "mid": v(191.04, -2.4) * mm, "end": v(191.28, -2.09) * mm});
            skLineSegment(sketch, "E51.9.0.25", {"start": v(185.18, -2.5) * mm, "end": v(185.6, -2.5) * mm});
            skLineSegment(sketch, "E51.9.0.26", {"start": v(184.42, -1.66) * mm, "end": v(184.58, -2.09) * mm});
            skArc(sketch, "E51.9.0.27", {"start": v(192.03, -1.24) * mm, "mid": v(191.67, -1.36) * mm, "end": v(191.43, -1.66) * mm});
            skArc(sketch, "E51.9.0.28", {"start": v(185.6, -2.5) * mm, "mid": v(185.96, -2.4) * mm, "end": v(186.2, -2.09) * mm});
            skLineSegment(sketch, "E51.9.0.29", {"start": v(186.2, -2.09) * mm, "end": v(186.35, -1.66) * mm});
            skLineSegment(sketch, "E51.9.0.30", {"start": v(190.26, -2.5) * mm, "end": v(190.68, -2.5) * mm});
            skLineSegment(sketch, "E51.9.0.31", {"start": v(188.55, -3.05) * mm, "end": v(188.55, -3.34) * mm, "construction": true});
            skLineSegment(sketch, "E51.9.0.32", {"start": v(192.9, -1.24) * mm, "end": v(192.9, -1.02) * mm});
            skLineSegment(sketch, "E51.9.0.33", {"start": v(193.12, -1.02) * mm, "end": v(193.12, -1.24) * mm});
            skLineSegment(sketch, "E51.9.0.34", {"start": v(187.82, -1.24) * mm, "end": v(187.82, -1.02) * mm});
            skLineSegment(sketch, "E51.9.0.35", {"start": v(188.66, -3.16) * mm, "end": v(188.43, -3.16) * mm, "construction": true});
            skLineSegment(sketch, "E51.9.0.36", {"start": v(188.04, -1.02) * mm, "end": v(188.04, -1.24) * mm});
            skLineSegment(sketch, "E51.9.0.37", {"start": v(187.82, -1.02) * mm, "end": v(188.04, -1.02) * mm});
            skLineSegment(sketch, "E51.9.0.38", {"start": v(192.9, -1.02) * mm, "end": v(193.12, -1.02) * mm});
            skPoint(sketch, "E52.9.0.0", {"position": v(197.76, -2.91) * mm});
            skLineSegment(sketch, "E52.9.0.1", {"start": v(203.28, -1.24) * mm, "end": v(204.14, -1.24) * mm});
            skPoint(sketch, "E52.9.0.2", {"position": v(197.1, -2.91) * mm});
            skLineSegment(sketch, "E52.9.0.3", {"start": v(201.44, -2.09) * mm, "end": v(201.6, -1.66) * mm});
            skArc(sketch, "E52.9.0.4", {"start": v(199.66, -1.66) * mm, "mid": v(199.43, -1.36) * mm, "end": v(199.06, -1.24) * mm});
            skPoint(sketch, "E52.9.0.5", {"position": v(191.56, -1.64) * mm});
            skPoint(sketch, "E52.9.0.6", {"position": v(198.88, -1.64) * mm});
            skPoint(sketch, "E52.9.0.7", {"position": v(192.02, -2.91) * mm});
            skArc(sketch, "E52.9.0.8", {"start": v(194.58, -1.66) * mm, "mid": v(194.35, -1.36) * mm, "end": v(193.98, -1.24) * mm});
            skPoint(sketch, "E52.9.0.9", {"position": v(193.8, -1.64) * mm});
            skLineSegment(sketch, "E52.9.0.10", {"start": v(202.2, -1.24) * mm, "end": v(203.06, -1.24) * mm});
            skLineSegment(sketch, "E52.9.0.11", {"start": v(198.2, -1.24) * mm, "end": v(199.06, -1.24) * mm});
            skPoint(sketch, "E52.9.0.12", {"position": v(198.41, -2.91) * mm});
            skLineSegment(sketch, "E52.9.0.13", {"start": v(199.66, -1.66) * mm, "end": v(199.82, -2.09) * mm});
            skLineSegment(sketch, "E52.9.0.14", {"start": v(197.11, -1.24) * mm, "end": v(197.98, -1.24) * mm});
            skPoint(sketch, "E52.9.0.15", {"position": v(196.64, -1.64) * mm});
            skPoint(sketch, "E52.9.0.16", {"position": v(193.33, -2.91) * mm});
            skPoint(sketch, "E52.9.0.17", {"position": v(195.22, -1.42) * mm});
            skPoint(sketch, "E52.9.0.18", {"position": v(193.57, -2.28) * mm});
            skPoint(sketch, "E52.9.0.19", {"position": v(192.68, -2.91) * mm});
            skArc(sketch, "E52.9.0.20", {"start": v(199.82, -2.09) * mm, "mid": v(200.05, -2.4) * mm, "end": v(200.42, -2.5) * mm});
            skArc(sketch, "E52.9.0.21", {"start": v(194.74, -2.09) * mm, "mid": v(194.97, -2.4) * mm, "end": v(195.34, -2.5) * mm});
            skPoint(sketch, "E52.9.0.22", {"position": v(191.79, -2.28) * mm});
            skArc(sketch, "E52.9.0.23", {"start": v(197.11, -1.24) * mm, "mid": v(196.75, -1.36) * mm, "end": v(196.51, -1.66) * mm});
            skArc(sketch, "E52.9.0.24", {"start": v(200.84, -2.5) * mm, "mid": v(201.2, -2.4) * mm, "end": v(201.44, -2.09) * mm});
            skLineSegment(sketch, "E52.9.0.25", {"start": v(195.34, -2.5) * mm, "end": v(195.76, -2.5) * mm});
            skLineSegment(sketch, "E52.9.0.26", {"start": v(194.58, -1.66) * mm, "end": v(194.74, -2.09) * mm});
            skArc(sketch, "E52.9.0.27", {"start": v(202.2, -1.24) * mm, "mid": v(201.83, -1.36) * mm, "end": v(201.6, -1.66) * mm});
            skArc(sketch, "E52.9.0.28", {"start": v(195.76, -2.5) * mm, "mid": v(196.12, -2.4) * mm, "end": v(196.36, -2.09) * mm});
            skLineSegment(sketch, "E52.9.0.29", {"start": v(196.36, -2.09) * mm, "end": v(196.51, -1.66) * mm});
            skLineSegment(sketch, "E52.9.0.30", {"start": v(200.42, -2.5) * mm, "end": v(200.84, -2.5) * mm});
            skLineSegment(sketch, "E52.9.0.31", {"start": v(195.22, -1.42) * mm, "end": v(195.22, -1.7) * mm, "construction": true});
            skLineSegment(sketch, "E52.9.0.32", {"start": v(203.06, -1.24) * mm, "end": v(203.06, -1.02) * mm});
            skLineSegment(sketch, "E52.9.0.33", {"start": v(203.28, -1.02) * mm, "end": v(203.28, -1.24) * mm});
            skLineSegment(sketch, "E52.9.0.34", {"start": v(197.98, -1.24) * mm, "end": v(197.98, -1.02) * mm});
            skLineSegment(sketch, "E52.9.0.35", {"start": v(195.33, -1.53) * mm, "end": v(195.1, -1.53) * mm, "construction": true});
            skLineSegment(sketch, "E52.9.0.36", {"start": v(198.2, -1.02) * mm, "end": v(198.2, -1.24) * mm});
            skLineSegment(sketch, "E52.9.0.37", {"start": v(197.98, -1.02) * mm, "end": v(198.2, -1.02) * mm});
            skLineSegment(sketch, "E52.9.0.38", {"start": v(203.06, -1.02) * mm, "end": v(203.28, -1.02) * mm});
            skPoint(sketch, "E53.9.0.0", {"position": v(207.37, -3.82) * mm});
            skLineSegment(sketch, "E53.9.0.1", {"start": v(213.44, -1.24) * mm, "end": v(214.3, -1.24) * mm});
            skPoint(sketch, "E53.9.0.2", {"position": v(206.7, -3.82) * mm});
            skLineSegment(sketch, "E53.9.0.3", {"start": v(211.6, -2.09) * mm, "end": v(211.75, -1.66) * mm});
            skArc(sketch, "E53.9.0.4", {"start": v(209.82, -1.66) * mm, "mid": v(209.59, -1.36) * mm, "end": v(209.22, -1.24) * mm});
            skPoint(sketch, "E53.9.0.5", {"position": v(201.17, -2.55) * mm});
            skPoint(sketch, "E53.9.0.6", {"position": v(208.49, -2.55) * mm});
            skPoint(sketch, "E53.9.0.7", {"position": v(201.63, -3.82) * mm});
            skArc(sketch, "E53.9.0.8", {"start": v(204.74, -1.66) * mm, "mid": v(204.5, -1.36) * mm, "end": v(204.14, -1.24) * mm});
            skPoint(sketch, "E53.9.0.9", {"position": v(203.4, -2.55) * mm});
            skLineSegment(sketch, "E53.9.0.10", {"start": v(212.35, -1.24) * mm, "end": v(213.22, -1.24) * mm});
            skLineSegment(sketch, "E53.9.0.11", {"start": v(208.36, -1.24) * mm, "end": v(209.22, -1.24) * mm});
            skPoint(sketch, "E53.9.0.12", {"position": v(208.02, -3.82) * mm});
            skLineSegment(sketch, "E53.9.0.13", {"start": v(209.82, -1.66) * mm, "end": v(209.98, -2.09) * mm});
            skLineSegment(sketch, "E53.9.0.14", {"start": v(207.27, -1.24) * mm, "end": v(208.14, -1.24) * mm});
            skPoint(sketch, "E53.9.0.15", {"position": v(206.25, -2.55) * mm});
            skPoint(sketch, "E53.9.0.16", {"position": v(202.94, -3.82) * mm});
            skPoint(sketch, "E53.9.0.17", {"position": v(204.83, -2.33) * mm});
            skPoint(sketch, "E53.9.0.18", {"position": v(203.18, -3.18) * mm});
            skPoint(sketch, "E53.9.0.19", {"position": v(202.29, -3.82) * mm});
            skArc(sketch, "E53.9.0.20", {"start": v(209.98, -2.09) * mm, "mid": v(210.2, -2.4) * mm, "end": v(210.58, -2.5) * mm});
            skArc(sketch, "E53.9.0.21", {"start": v(204.9, -2.09) * mm, "mid": v(205.13, -2.4) * mm, "end": v(205.5, -2.5) * mm});
            skPoint(sketch, "E53.9.0.22", {"position": v(201.4, -3.18) * mm});
            skArc(sketch, "E53.9.0.23", {"start": v(207.27, -1.24) * mm, "mid": v(206.9, -1.36) * mm, "end": v(206.67, -1.66) * mm});
            skArc(sketch, "E53.9.0.24", {"start": v(211, -2.5) * mm, "mid": v(211.36, -2.4) * mm, "end": v(211.6, -2.09) * mm});
            skLineSegment(sketch, "E53.9.0.25", {"start": v(205.5, -2.5) * mm, "end": v(205.92, -2.5) * mm});
            skLineSegment(sketch, "E53.9.0.26", {"start": v(204.74, -1.66) * mm, "end": v(204.9, -2.09) * mm});
            skArc(sketch, "E53.9.0.27", {"start": v(212.35, -1.24) * mm, "mid": v(211.99, -1.36) * mm, "end": v(211.75, -1.66) * mm});
            skArc(sketch, "E53.9.0.28", {"start": v(205.92, -2.5) * mm, "mid": v(206.28, -2.4) * mm, "end": v(206.52, -2.09) * mm});
            skLineSegment(sketch, "E53.9.0.29", {"start": v(206.52, -2.09) * mm, "end": v(206.67, -1.66) * mm});
            skLineSegment(sketch, "E53.9.0.30", {"start": v(210.58, -2.5) * mm, "end": v(211, -2.5) * mm});
            skLineSegment(sketch, "E53.9.0.31", {"start": v(204.83, -2.33) * mm, "end": v(204.83, -2.61) * mm, "construction": true});
            skLineSegment(sketch, "E53.9.0.32", {"start": v(213.22, -1.24) * mm, "end": v(213.22, -1.02) * mm});
            skLineSegment(sketch, "E53.9.0.33", {"start": v(213.44, -1.02) * mm, "end": v(213.44, -1.24) * mm});
            skLineSegment(sketch, "E53.9.0.34", {"start": v(208.14, -1.24) * mm, "end": v(208.14, -1.02) * mm});
            skLineSegment(sketch, "E53.9.0.35", {"start": v(204.94, -2.44) * mm, "end": v(204.71, -2.44) * mm, "construction": true});
            skLineSegment(sketch, "E53.9.0.36", {"start": v(208.36, -1.02) * mm, "end": v(208.36, -1.24) * mm});
            skLineSegment(sketch, "E53.9.0.37", {"start": v(208.14, -1.02) * mm, "end": v(208.36, -1.02) * mm});
            skLineSegment(sketch, "E53.9.0.38", {"start": v(213.22, -1.02) * mm, "end": v(213.44, -1.02) * mm});
            skPoint(sketch, "E54.9.0.0", {"position": v(219.38, -1.87) * mm});
            skLineSegment(sketch, "E54.9.0.1", {"start": v(223.6, -1.24) * mm, "end": v(224.46, -1.24) * mm});
            skPoint(sketch, "E54.9.0.2", {"position": v(218.72, -1.87) * mm});
            skLineSegment(sketch, "E54.9.0.3", {"start": v(221.76, -2.09) * mm, "end": v(221.91, -1.66) * mm});
            skArc(sketch, "E54.9.0.4", {"start": v(219.98, -1.66) * mm, "mid": v(219.75, -1.36) * mm, "end": v(219.38, -1.24) * mm});
            skPoint(sketch, "E54.9.0.5", {"position": v(213.18, -0.6) * mm});
            skPoint(sketch, "E54.9.0.6", {"position": v(220.5, -0.6) * mm});
            skPoint(sketch, "E54.9.0.7", {"position": v(213.64, -1.87) * mm});
            skArc(sketch, "E54.9.0.8", {"start": v(214.9, -1.66) * mm, "mid": v(214.67, -1.36) * mm, "end": v(214.3, -1.24) * mm});
            skPoint(sketch, "E54.9.0.9", {"position": v(215.42, -0.6) * mm});
            skLineSegment(sketch, "E54.9.0.10", {"start": v(222.51, -1.24) * mm, "end": v(223.38, -1.24) * mm});
            skLineSegment(sketch, "E54.9.0.11", {"start": v(218.52, -1.24) * mm, "end": v(219.38, -1.24) * mm});
            skPoint(sketch, "E54.9.0.12", {"position": v(220.03, -1.87) * mm});
            skLineSegment(sketch, "E54.9.0.13", {"start": v(219.98, -1.66) * mm, "end": v(220.14, -2.09) * mm});
            skLineSegment(sketch, "E54.9.0.14", {"start": v(217.43, -1.24) * mm, "end": v(218.3, -1.24) * mm});
            skPoint(sketch, "E54.9.0.15", {"position": v(218.26, -0.6) * mm});
            skPoint(sketch, "E54.9.0.16", {"position": v(214.95, -1.87) * mm});
            skPoint(sketch, "E54.9.0.17", {"position": v(216.84, -0.38) * mm});
            skPoint(sketch, "E54.9.0.18", {"position": v(215.19, -1.24) * mm});
            skPoint(sketch, "E54.9.0.19", {"position": v(214.3, -1.87) * mm});
            skArc(sketch, "E54.9.0.20", {"start": v(220.14, -2.09) * mm, "mid": v(220.37, -2.4) * mm, "end": v(220.74, -2.5) * mm});
            skArc(sketch, "E54.9.0.21", {"start": v(215.06, -2.09) * mm, "mid": v(215.29, -2.4) * mm, "end": v(215.66, -2.5) * mm});
            skPoint(sketch, "E54.9.0.22", {"position": v(213.4, -1.24) * mm});
            skArc(sketch, "E54.9.0.23", {"start": v(217.43, -1.24) * mm, "mid": v(217.07, -1.36) * mm, "end": v(216.83, -1.66) * mm});
            skArc(sketch, "E54.9.0.24", {"start": v(221.16, -2.5) * mm, "mid": v(221.52, -2.4) * mm, "end": v(221.76, -2.09) * mm});
            skLineSegment(sketch, "E54.9.0.25", {"start": v(215.66, -2.5) * mm, "end": v(216.08, -2.5) * mm});
            skLineSegment(sketch, "E54.9.0.26", {"start": v(214.9, -1.66) * mm, "end": v(215.06, -2.09) * mm});
            skArc(sketch, "E54.9.0.27", {"start": v(222.51, -1.24) * mm, "mid": v(222.15, -1.36) * mm, "end": v(221.91, -1.66) * mm});
            skArc(sketch, "E54.9.0.28", {"start": v(216.08, -2.5) * mm, "mid": v(216.44, -2.4) * mm, "end": v(216.68, -2.09) * mm});
            skLineSegment(sketch, "E54.9.0.29", {"start": v(216.68, -2.09) * mm, "end": v(216.83, -1.66) * mm});
            skLineSegment(sketch, "E54.9.0.30", {"start": v(220.74, -2.5) * mm, "end": v(221.16, -2.5) * mm});
            skLineSegment(sketch, "E54.9.0.31", {"start": v(216.84, -0.38) * mm, "end": v(216.84, -0.67) * mm, "construction": true});
            skLineSegment(sketch, "E54.9.0.32", {"start": v(223.38, -1.24) * mm, "end": v(223.38, -1.02) * mm});
            skLineSegment(sketch, "E54.9.0.33", {"start": v(223.6, -1.02) * mm, "end": v(223.6, -1.24) * mm});
            skLineSegment(sketch, "E54.9.0.34", {"start": v(218.3, -1.24) * mm, "end": v(218.3, -1.02) * mm});
            skLineSegment(sketch, "E54.9.0.35", {"start": v(216.95, -0.5) * mm, "end": v(216.73, -0.5) * mm, "construction": true});
            skLineSegment(sketch, "E54.9.0.36", {"start": v(218.52, -1.02) * mm, "end": v(218.52, -1.24) * mm});
            skLineSegment(sketch, "E54.9.0.37", {"start": v(218.3, -1.02) * mm, "end": v(218.52, -1.02) * mm});
            skLineSegment(sketch, "E54.9.0.38", {"start": v(223.38, -1.02) * mm, "end": v(223.6, -1.02) * mm});
            skPoint(sketch, "E55.9.0.0", {"position": v(227.56, -2.35) * mm});
            skLineSegment(sketch, "E55.9.0.1", {"start": v(233.76, -1.24) * mm, "end": v(234.62, -1.24) * mm});
            skPoint(sketch, "E55.9.0.2", {"position": v(226.9, -2.35) * mm});
            skLineSegment(sketch, "E55.9.0.3", {"start": v(231.92, -2.09) * mm, "end": v(232.07, -1.66) * mm});
            skArc(sketch, "E55.9.0.4", {"start": v(230.14, -1.66) * mm, "mid": v(229.9, -1.36) * mm, "end": v(229.54, -1.24) * mm});
            skPoint(sketch, "E55.9.0.5", {"position": v(221.36, -1.08) * mm});
            skPoint(sketch, "E55.9.0.6", {"position": v(228.68, -1.08) * mm});
            skPoint(sketch, "E55.9.0.7", {"position": v(221.82, -2.35) * mm});
            skArc(sketch, "E55.9.0.8", {"start": v(225.06, -1.66) * mm, "mid": v(224.83, -1.36) * mm, "end": v(224.46, -1.24) * mm});
            skPoint(sketch, "E55.9.0.9", {"position": v(223.6, -1.08) * mm});
            skLineSegment(sketch, "E55.9.0.10", {"start": v(232.67, -1.24) * mm, "end": v(233.54, -1.24) * mm});
            skLineSegment(sketch, "E55.9.0.11", {"start": v(228.68, -1.24) * mm, "end": v(229.54, -1.24) * mm});
            skPoint(sketch, "E55.9.0.12", {"position": v(228.22, -2.35) * mm});
            skLineSegment(sketch, "E55.9.0.13", {"start": v(230.14, -1.66) * mm, "end": v(230.3, -2.09) * mm});
            skLineSegment(sketch, "E55.9.0.14", {"start": v(227.6, -1.24) * mm, "end": v(228.46, -1.24) * mm});
            skPoint(sketch, "E55.9.0.15", {"position": v(226.44, -1.08) * mm});
            skPoint(sketch, "E55.9.0.16", {"position": v(223.14, -2.35) * mm});
            skPoint(sketch, "E55.9.0.17", {"position": v(225.02, -0.86) * mm});
            skPoint(sketch, "E55.9.0.18", {"position": v(223.37, -1.71) * mm});
            skPoint(sketch, "E55.9.0.19", {"position": v(222.48, -2.35) * mm});
            skArc(sketch, "E55.9.0.20", {"start": v(230.3, -2.09) * mm, "mid": v(230.53, -2.4) * mm, "end": v(230.9, -2.5) * mm});
            skArc(sketch, "E55.9.0.21", {"start": v(225.22, -2.09) * mm, "mid": v(225.45, -2.4) * mm, "end": v(225.82, -2.5) * mm});
            skPoint(sketch, "E55.9.0.22", {"position": v(221.6, -1.71) * mm});
            skArc(sketch, "E55.9.0.23", {"start": v(227.6, -1.24) * mm, "mid": v(227.23, -1.36) * mm, "end": v(227, -1.66) * mm});
            skArc(sketch, "E55.9.0.24", {"start": v(231.32, -2.5) * mm, "mid": v(231.68, -2.4) * mm, "end": v(231.92, -2.09) * mm});
            skLineSegment(sketch, "E55.9.0.25", {"start": v(225.82, -2.5) * mm, "end": v(226.24, -2.5) * mm});
            skLineSegment(sketch, "E55.9.0.26", {"start": v(225.06, -1.66) * mm, "end": v(225.22, -2.09) * mm});
            skArc(sketch, "E55.9.0.27", {"start": v(232.67, -1.24) * mm, "mid": v(232.3, -1.36) * mm, "end": v(232.07, -1.66) * mm});
            skArc(sketch, "E55.9.0.28", {"start": v(226.24, -2.5) * mm, "mid": v(226.6, -2.4) * mm, "end": v(226.84, -2.09) * mm});
            skLineSegment(sketch, "E55.9.0.29", {"start": v(226.84, -2.09) * mm, "end": v(227, -1.66) * mm});
            skLineSegment(sketch, "E55.9.0.30", {"start": v(230.9, -2.5) * mm, "end": v(231.32, -2.5) * mm});
            skLineSegment(sketch, "E55.9.0.31", {"start": v(225.02, -0.86) * mm, "end": v(225.02, -1.15) * mm, "construction": true});
            skLineSegment(sketch, "E55.9.0.32", {"start": v(233.54, -1.24) * mm, "end": v(233.54, -1.02) * mm});
            skLineSegment(sketch, "E55.9.0.33", {"start": v(233.76, -1.02) * mm, "end": v(233.76, -1.24) * mm});
            skLineSegment(sketch, "E55.9.0.34", {"start": v(228.46, -1.24) * mm, "end": v(228.46, -1.02) * mm});
            skLineSegment(sketch, "E55.9.0.35", {"start": v(225.13, -0.97) * mm, "end": v(224.9, -0.97) * mm, "construction": true});
            skLineSegment(sketch, "E55.9.0.36", {"start": v(228.68, -1.02) * mm, "end": v(228.68, -1.24) * mm});
            skLineSegment(sketch, "E55.9.0.37", {"start": v(228.46, -1.02) * mm, "end": v(228.68, -1.02) * mm});
            skLineSegment(sketch, "E55.9.0.38", {"start": v(233.54, -1.02) * mm, "end": v(233.76, -1.02) * mm});
            skPoint(sketch, "E56.9.0.0", {"position": v(240.85, -1.88) * mm});
            skLineSegment(sketch, "E56.9.0.1", {"start": v(243.92, -1.24) * mm, "end": v(244.78, -1.24) * mm});
            skPoint(sketch, "E56.9.0.2", {"position": v(240.2, -1.88) * mm});
            skLineSegment(sketch, "E56.9.0.3", {"start": v(242.08, -2.09) * mm, "end": v(242.23, -1.66) * mm});
            skArc(sketch, "E56.9.0.4", {"start": v(240.3, -1.66) * mm, "mid": v(240.07, -1.36) * mm, "end": v(239.7, -1.24) * mm});
            skPoint(sketch, "E56.9.0.5", {"position": v(234.65, -0.6) * mm});
            skPoint(sketch, "E56.9.0.6", {"position": v(241.97, -0.6) * mm});
            skPoint(sketch, "E56.9.0.7", {"position": v(235.12, -1.88) * mm});
            skArc(sketch, "E56.9.0.8", {"start": v(235.22, -1.66) * mm, "mid": v(234.99, -1.36) * mm, "end": v(234.62, -1.24) * mm});
            skPoint(sketch, "E56.9.0.9", {"position": v(236.9, -0.6) * mm});
            skLineSegment(sketch, "E56.9.0.10", {"start": v(242.83, -1.24) * mm, "end": v(243.7, -1.24) * mm});
            skLineSegment(sketch, "E56.9.0.11", {"start": v(238.84, -1.24) * mm, "end": v(239.7, -1.24) * mm});
            skPoint(sketch, "E56.9.0.12", {"position": v(241.51, -1.88) * mm});
            skLineSegment(sketch, "E56.9.0.13", {"start": v(240.3, -1.66) * mm, "end": v(240.46, -2.09) * mm});
            skLineSegment(sketch, "E56.9.0.14", {"start": v(237.75, -1.24) * mm, "end": v(238.62, -1.24) * mm});
            skPoint(sketch, "E56.9.0.15", {"position": v(239.73, -0.6) * mm});
            skPoint(sketch, "E56.9.0.16", {"position": v(236.43, -1.88) * mm});
            skPoint(sketch, "E56.9.0.17", {"position": v(238.31, -0.38) * mm});
            skPoint(sketch, "E56.9.0.18", {"position": v(236.66, -1.24) * mm});
            skPoint(sketch, "E56.9.0.19", {"position": v(235.77, -1.88) * mm});
            skArc(sketch, "E56.9.0.20", {"start": v(240.46, -2.09) * mm, "mid": v(240.69, -2.4) * mm, "end": v(241.06, -2.5) * mm});
            skArc(sketch, "E56.9.0.21", {"start": v(235.38, -2.09) * mm, "mid": v(235.6, -2.4) * mm, "end": v(235.98, -2.5) * mm});
            skPoint(sketch, "E56.9.0.22", {"position": v(234.89, -1.24) * mm});
            skArc(sketch, "E56.9.0.23", {"start": v(237.75, -1.24) * mm, "mid": v(237.39, -1.36) * mm, "end": v(237.15, -1.66) * mm});
            skArc(sketch, "E56.9.0.24", {"start": v(241.48, -2.5) * mm, "mid": v(241.84, -2.4) * mm, "end": v(242.08, -2.09) * mm});
            skLineSegment(sketch, "E56.9.0.25", {"start": v(235.98, -2.5) * mm, "end": v(236.4, -2.5) * mm});
            skLineSegment(sketch, "E56.9.0.26", {"start": v(235.22, -1.66) * mm, "end": v(235.38, -2.09) * mm});
            skArc(sketch, "E56.9.0.27", {"start": v(242.83, -1.24) * mm, "mid": v(242.47, -1.36) * mm, "end": v(242.23, -1.66) * mm});
            skArc(sketch, "E56.9.0.28", {"start": v(236.4, -2.5) * mm, "mid": v(236.76, -2.4) * mm, "end": v(237, -2.09) * mm});
            skLineSegment(sketch, "E56.9.0.29", {"start": v(237, -2.09) * mm, "end": v(237.15, -1.66) * mm});
            skLineSegment(sketch, "E56.9.0.30", {"start": v(241.06, -2.5) * mm, "end": v(241.48, -2.5) * mm});
            skLineSegment(sketch, "E56.9.0.31", {"start": v(238.31, -0.38) * mm, "end": v(238.31, -0.67) * mm, "construction": true});
            skLineSegment(sketch, "E56.9.0.32", {"start": v(243.7, -1.24) * mm, "end": v(243.7, -1.02) * mm});
            skLineSegment(sketch, "E56.9.0.33", {"start": v(243.92, -1.02) * mm, "end": v(243.92, -1.24) * mm});
            skLineSegment(sketch, "E56.9.0.34", {"start": v(238.62, -1.24) * mm, "end": v(238.62, -1.02) * mm});
            skLineSegment(sketch, "E56.9.0.35", {"start": v(238.43, -0.5) * mm, "end": v(238.2, -0.5) * mm, "construction": true});
            skLineSegment(sketch, "E56.9.0.36", {"start": v(238.84, -1.02) * mm, "end": v(238.84, -1.24) * mm});
            skLineSegment(sketch, "E56.9.0.37", {"start": v(238.62, -1.02) * mm, "end": v(238.84, -1.02) * mm});
            skLineSegment(sketch, "E56.9.0.38", {"start": v(243.7, -1.02) * mm, "end": v(243.92, -1.02) * mm});
            skPoint(sketch, "E57.9.0.0", {"position": v(250.65, -2.51) * mm});
            skLineSegment(sketch, "E57.9.0.1", {"start": v(254.08, -1.24) * mm, "end": v(254.94, -1.24) * mm});
            skPoint(sketch, "E57.9.0.2", {"position": v(250, -2.51) * mm});
            skLineSegment(sketch, "E57.9.0.3", {"start": v(252.24, -2.09) * mm, "end": v(252.4, -1.66) * mm});
            skArc(sketch, "E57.9.0.4", {"start": v(250.46, -1.66) * mm, "mid": v(250.23, -1.36) * mm, "end": v(249.86, -1.24) * mm});
            skPoint(sketch, "E57.9.0.5", {"position": v(244.45, -1.24) * mm});
            skPoint(sketch, "E57.9.0.6", {"position": v(251.77, -1.24) * mm});
            skPoint(sketch, "E57.9.0.7", {"position": v(244.92, -2.51) * mm});
            skArc(sketch, "E57.9.0.8", {"start": v(245.38, -1.66) * mm, "mid": v(245.15, -1.36) * mm, "end": v(244.78, -1.24) * mm});
            skPoint(sketch, "E57.9.0.9", {"position": v(246.7, -1.24) * mm});
            skLineSegment(sketch, "E57.9.0.10", {"start": v(253, -1.24) * mm, "end": v(253.86, -1.24) * mm});
            skLineSegment(sketch, "E57.9.0.11", {"start": v(249, -1.24) * mm, "end": v(249.86, -1.24) * mm});
            skPoint(sketch, "E57.9.0.12", {"position": v(251.31, -2.51) * mm});
            skLineSegment(sketch, "E57.9.0.13", {"start": v(250.46, -1.66) * mm, "end": v(250.62, -2.09) * mm});
            skLineSegment(sketch, "E57.9.0.14", {"start": v(247.91, -1.24) * mm, "end": v(248.78, -1.24) * mm});
            skPoint(sketch, "E57.9.0.15", {"position": v(249.53, -1.24) * mm});
            skPoint(sketch, "E57.9.0.16", {"position": v(246.23, -2.51) * mm});
            skPoint(sketch, "E57.9.0.17", {"position": v(248.11, -1.02) * mm});
            skPoint(sketch, "E57.9.0.18", {"position": v(246.46, -1.88) * mm});
            skPoint(sketch, "E57.9.0.19", {"position": v(245.57, -2.51) * mm});
            skArc(sketch, "E57.9.0.20", {"start": v(250.62, -2.09) * mm, "mid": v(250.85, -2.4) * mm, "end": v(251.22, -2.5) * mm});
            skArc(sketch, "E57.9.0.21", {"start": v(245.54, -2.09) * mm, "mid": v(245.77, -2.4) * mm, "end": v(246.14, -2.5) * mm});
            skPoint(sketch, "E57.9.0.22", {"position": v(244.68, -1.88) * mm});
            skArc(sketch, "E57.9.0.23", {"start": v(247.91, -1.24) * mm, "mid": v(247.55, -1.36) * mm, "end": v(247.31, -1.66) * mm});
            skArc(sketch, "E57.9.0.24", {"start": v(251.64, -2.5) * mm, "mid": v(252, -2.4) * mm, "end": v(252.24, -2.09) * mm});
            skLineSegment(sketch, "E57.9.0.25", {"start": v(246.14, -2.5) * mm, "end": v(246.56, -2.5) * mm});
            skLineSegment(sketch, "E57.9.0.26", {"start": v(245.38, -1.66) * mm, "end": v(245.54, -2.09) * mm});
            skArc(sketch, "E57.9.0.27", {"start": v(253, -1.24) * mm, "mid": v(252.63, -1.36) * mm, "end": v(252.4, -1.66) * mm});
            skArc(sketch, "E57.9.0.28", {"start": v(246.56, -2.5) * mm, "mid": v(246.92, -2.4) * mm, "end": v(247.16, -2.09) * mm});
            skLineSegment(sketch, "E57.9.0.29", {"start": v(247.16, -2.09) * mm, "end": v(247.31, -1.66) * mm});
            skLineSegment(sketch, "E57.9.0.30", {"start": v(251.22, -2.5) * mm, "end": v(251.64, -2.5) * mm});
            skLineSegment(sketch, "E57.9.0.31", {"start": v(248.11, -1.02) * mm, "end": v(248.11, -1.3) * mm, "construction": true});
            skLineSegment(sketch, "E57.9.0.32", {"start": v(253.86, -1.24) * mm, "end": v(253.86, -1.02) * mm});
            skLineSegment(sketch, "E57.9.0.33", {"start": v(254.08, -1.02) * mm, "end": v(254.08, -1.24) * mm});
            skLineSegment(sketch, "E57.9.0.34", {"start": v(248.78, -1.24) * mm, "end": v(248.78, -1.02) * mm});
            skLineSegment(sketch, "E57.9.0.35", {"start": v(248.22, -1.13) * mm, "end": v(248, -1.13) * mm, "construction": true});
            skLineSegment(sketch, "E57.9.0.36", {"start": v(249, -1.02) * mm, "end": v(249, -1.24) * mm});
            skLineSegment(sketch, "E57.9.0.37", {"start": v(248.78, -1.02) * mm, "end": v(249, -1.02) * mm});
            skLineSegment(sketch, "E57.9.0.38", {"start": v(253.86, -1.02) * mm, "end": v(254.08, -1.02) * mm});
            skPoint(sketch, "E58.9.0.0", {"position": v(261.75, -2.17) * mm});
            skLineSegment(sketch, "E58.9.0.1", {"start": v(264.24, -1.24) * mm, "end": v(265.1, -1.24) * mm});
            skPoint(sketch, "E58.9.0.2", {"position": v(261.09, -2.17) * mm});
            skLineSegment(sketch, "E58.9.0.3", {"start": v(262.4, -2.09) * mm, "end": v(262.55, -1.66) * mm});
            skArc(sketch, "E58.9.0.4", {"start": v(260.62, -1.66) * mm, "mid": v(260.39, -1.36) * mm, "end": v(260.02, -1.24) * mm});
            skPoint(sketch, "E58.9.0.5", {"position": v(255.55, -0.9) * mm});
            skPoint(sketch, "E58.9.0.6", {"position": v(262.87, -0.9) * mm});
            skPoint(sketch, "E58.9.0.7", {"position": v(256, -2.17) * mm});
            skArc(sketch, "E58.9.0.8", {"start": v(255.54, -1.66) * mm, "mid": v(255.3, -1.36) * mm, "end": v(254.94, -1.24) * mm});
            skPoint(sketch, "E58.9.0.9", {"position": v(257.79, -0.9) * mm});
            skLineSegment(sketch, "E58.9.0.10", {"start": v(263.15, -1.24) * mm, "end": v(264.02, -1.24) * mm});
            skLineSegment(sketch, "E58.9.0.11", {"start": v(259.16, -1.24) * mm, "end": v(260.02, -1.24) * mm});
            skPoint(sketch, "E58.9.0.12", {"position": v(262.4, -2.17) * mm});
            skLineSegment(sketch, "E58.9.0.13", {"start": v(260.62, -1.66) * mm, "end": v(260.78, -2.09) * mm});
            skLineSegment(sketch, "E58.9.0.14", {"start": v(258.07, -1.24) * mm, "end": v(258.94, -1.24) * mm});
            skPoint(sketch, "E58.9.0.15", {"position": v(260.63, -0.9) * mm});
            skPoint(sketch, "E58.9.0.16", {"position": v(257.32, -2.17) * mm});
            skPoint(sketch, "E58.9.0.17", {"position": v(259.2, -0.68) * mm});
            skPoint(sketch, "E58.9.0.18", {"position": v(257.55, -1.54) * mm});
            skPoint(sketch, "E58.9.0.19", {"position": v(256.67, -2.17) * mm});
            skArc(sketch, "E58.9.0.20", {"start": v(260.78, -2.09) * mm, "mid": v(261, -2.4) * mm, "end": v(261.38, -2.5) * mm});
            skArc(sketch, "E58.9.0.21", {"start": v(255.7, -2.09) * mm, "mid": v(255.93, -2.4) * mm, "end": v(256.3, -2.5) * mm});
            skPoint(sketch, "E58.9.0.22", {"position": v(255.78, -1.54) * mm});
            skArc(sketch, "E58.9.0.23", {"start": v(258.07, -1.24) * mm, "mid": v(257.7, -1.36) * mm, "end": v(257.47, -1.66) * mm});
            skArc(sketch, "E58.9.0.24", {"start": v(261.8, -2.5) * mm, "mid": v(262.16, -2.4) * mm, "end": v(262.4, -2.09) * mm});
            skLineSegment(sketch, "E58.9.0.25", {"start": v(256.3, -2.5) * mm, "end": v(256.72, -2.5) * mm});
            skLineSegment(sketch, "E58.9.0.26", {"start": v(255.54, -1.66) * mm, "end": v(255.7, -2.09) * mm});
            skArc(sketch, "E58.9.0.27", {"start": v(263.15, -1.24) * mm, "mid": v(262.79, -1.36) * mm, "end": v(262.55, -1.66) * mm});
            skArc(sketch, "E58.9.0.28", {"start": v(256.72, -2.5) * mm, "mid": v(257.08, -2.4) * mm, "end": v(257.32, -2.09) * mm});
            skLineSegment(sketch, "E58.9.0.29", {"start": v(257.32, -2.09) * mm, "end": v(257.47, -1.66) * mm});
            skLineSegment(sketch, "E58.9.0.30", {"start": v(261.38, -2.5) * mm, "end": v(261.8, -2.5) * mm});
            skLineSegment(sketch, "E58.9.0.31", {"start": v(259.2, -0.68) * mm, "end": v(259.2, -0.97) * mm, "construction": true});
            skLineSegment(sketch, "E58.9.0.32", {"start": v(264.02, -1.24) * mm, "end": v(264.02, -1.02) * mm});
            skLineSegment(sketch, "E58.9.0.33", {"start": v(264.24, -1.02) * mm, "end": v(264.24, -1.24) * mm});
            skLineSegment(sketch, "E58.9.0.34", {"start": v(258.94, -1.24) * mm, "end": v(258.94, -1.02) * mm});
            skLineSegment(sketch, "E58.9.0.35", {"start": v(259.32, -0.8) * mm, "end": v(259.1, -0.8) * mm, "construction": true});
            skLineSegment(sketch, "E58.9.0.36", {"start": v(259.16, -1.02) * mm, "end": v(259.16, -1.24) * mm});
            skLineSegment(sketch, "E58.9.0.37", {"start": v(258.94, -1.02) * mm, "end": v(259.16, -1.02) * mm});
            skLineSegment(sketch, "E58.9.0.38", {"start": v(264.02, -1.02) * mm, "end": v(264.24, -1.02) * mm});
            skPoint(sketch, "E59.9.0.0", {"position": v(272.17, -2.32) * mm});
            skLineSegment(sketch, "E59.9.0.1", {"start": v(274.68, -1.2) * mm, "end": v(275.54, -1.2) * mm});
            skPoint(sketch, "E59.9.0.2", {"position": v(271.51, -2.32) * mm});
            skLineSegment(sketch, "E59.9.0.3", {"start": v(272.56, -2.09) * mm, "end": v(272.71, -1.66) * mm});
            skArc(sketch, "E59.9.0.4", {"start": v(270.78, -1.66) * mm, "mid": v(270.55, -1.36) * mm, "end": v(270.18, -1.24) * mm});
            skPoint(sketch, "E59.9.0.5", {"position": v(265.97, -1.05) * mm});
            skPoint(sketch, "E59.9.0.6", {"position": v(273.3, -1.05) * mm});
            skPoint(sketch, "E59.9.0.7", {"position": v(266.43, -2.32) * mm});
            skArc(sketch, "E59.9.0.8", {"start": v(265.7, -1.66) * mm, "mid": v(265.47, -1.36) * mm, "end": v(265.1, -1.24) * mm});
            skPoint(sketch, "E59.9.0.9", {"position": v(268.21, -1.05) * mm});
            skLineSegment(sketch, "E59.9.0.10", {"start": v(273.31, -1.24) * mm, "end": v(274.18, -1.24) * mm});
            skLineSegment(sketch, "E59.9.0.11", {"start": v(269.32, -1.24) * mm, "end": v(270.18, -1.24) * mm});
            skPoint(sketch, "E59.9.0.12", {"position": v(272.83, -2.32) * mm});
            skLineSegment(sketch, "E59.9.0.13", {"start": v(270.78, -1.66) * mm, "end": v(270.94, -2.09) * mm});
            skLineSegment(sketch, "E59.9.0.14", {"start": v(268.23, -1.24) * mm, "end": v(269.1, -1.24) * mm});
            skPoint(sketch, "E59.9.0.15", {"position": v(271.05, -1.05) * mm});
            skPoint(sketch, "E59.9.0.16", {"position": v(267.75, -2.32) * mm});
            skPoint(sketch, "E59.9.0.17", {"position": v(269.63, -0.83) * mm});
            skPoint(sketch, "E59.9.0.18", {"position": v(267.98, -1.69) * mm});
            skPoint(sketch, "E59.9.0.19", {"position": v(267.1, -2.32) * mm});
            skArc(sketch, "E59.9.0.20", {"start": v(270.94, -2.09) * mm, "mid": v(271.17, -2.4) * mm, "end": v(271.54, -2.5) * mm});
            skArc(sketch, "E59.9.0.21", {"start": v(265.86, -2.09) * mm, "mid": v(266.09, -2.4) * mm, "end": v(266.46, -2.5) * mm});
            skPoint(sketch, "E59.9.0.22", {"position": v(266.2, -1.69) * mm});
            skArc(sketch, "E59.9.0.23", {"start": v(268.23, -1.24) * mm, "mid": v(267.87, -1.36) * mm, "end": v(267.63, -1.66) * mm});
            skArc(sketch, "E59.9.0.24", {"start": v(271.96, -2.5) * mm, "mid": v(272.32, -2.4) * mm, "end": v(272.56, -2.09) * mm});
            skLineSegment(sketch, "E59.9.0.25", {"start": v(266.46, -2.5) * mm, "end": v(266.88, -2.5) * mm});
            skLineSegment(sketch, "E59.9.0.26", {"start": v(265.7, -1.66) * mm, "end": v(265.86, -2.09) * mm});
            skArc(sketch, "E59.9.0.27", {"start": v(273.31, -1.24) * mm, "mid": v(272.95, -1.36) * mm, "end": v(272.71, -1.66) * mm});
            skArc(sketch, "E59.9.0.28", {"start": v(266.88, -2.5) * mm, "mid": v(267.24, -2.4) * mm, "end": v(267.48, -2.09) * mm});
            skLineSegment(sketch, "E59.9.0.29", {"start": v(267.48, -2.09) * mm, "end": v(267.63, -1.66) * mm});
            skLineSegment(sketch, "E59.9.0.30", {"start": v(271.54, -2.5) * mm, "end": v(271.96, -2.5) * mm});
            skLineSegment(sketch, "E59.9.0.31", {"start": v(269.63, -0.83) * mm, "end": v(269.63, -1.12) * mm, "construction": true});
            skLineSegment(sketch, "E59.9.0.32", {"start": v(274.18, -1.24) * mm, "end": v(274.18, -1.02) * mm});
            skLineSegment(sketch, "E59.9.0.33", {"start": v(274.68, -1.02) * mm, "end": v(274.68, -1.2) * mm});
            skLineSegment(sketch, "E59.9.0.34", {"start": v(269.1, -1.24) * mm, "end": v(269.1, -1.02) * mm});
            skLineSegment(sketch, "E59.9.0.35", {"start": v(269.74, -0.94) * mm, "end": v(269.52, -0.94) * mm, "construction": true});
            skLineSegment(sketch, "E59.9.0.36", {"start": v(269.32, -1.02) * mm, "end": v(269.32, -1.24) * mm});
            skLineSegment(sketch, "E59.9.0.37", {"start": v(269.1, -1.02) * mm, "end": v(269.32, -1.02) * mm});
            skLineSegment(sketch, "E59.9.0.38", {"start": v(274.18, -1.02) * mm, "end": v(274.68, -1.02) * mm});
            skPoint(sketch, "E60.9.0.0", {"position": v(282.19, -2.47) * mm});
            skLineSegment(sketch, "E60.9.0.1", {"start": v(284.84, -1.2) * mm, "end": v(285.7, -1.2) * mm});
            skPoint(sketch, "E60.9.0.2", {"position": v(281.53, -2.47) * mm});
            skLineSegment(sketch, "E60.9.0.3", {"start": v(283, -2.05) * mm, "end": v(283.15, -1.63) * mm});
            skArc(sketch, "E60.9.0.4", {"start": v(281.22, -1.63) * mm, "mid": v(280.99, -1.32) * mm, "end": v(280.62, -1.2) * mm});
            skPoint(sketch, "E60.9.0.5", {"position": v(275.99, -1.2) * mm});
            skPoint(sketch, "E60.9.0.6", {"position": v(283.3, -1.2) * mm});
            skPoint(sketch, "E60.9.0.7", {"position": v(276.45, -2.47) * mm});
            skArc(sketch, "E60.9.0.8", {"start": v(276.14, -1.63) * mm, "mid": v(275.9, -1.32) * mm, "end": v(275.54, -1.2) * mm});
            skPoint(sketch, "E60.9.0.9", {"position": v(278.23, -1.2) * mm});
            skLineSegment(sketch, "E60.9.0.10", {"start": v(283.76, -1.2) * mm, "end": v(284.62, -1.2) * mm});
            skLineSegment(sketch, "E60.9.0.11", {"start": v(279.76, -1.2) * mm, "end": v(280.62, -1.2) * mm});
            skPoint(sketch, "E60.9.0.12", {"position": v(282.85, -2.47) * mm});
            skLineSegment(sketch, "E60.9.0.13", {"start": v(281.22, -1.63) * mm, "end": v(281.38, -2.05) * mm});
            skLineSegment(sketch, "E60.9.0.14", {"start": v(278.68, -1.2) * mm, "end": v(279.54, -1.2) * mm});
            skPoint(sketch, "E60.9.0.15", {"position": v(281.07, -1.2) * mm});
            skPoint(sketch, "E60.9.0.16", {"position": v(277.77, -2.47) * mm});
            skPoint(sketch, "E60.9.0.17", {"position": v(279.65, -0.98) * mm});
            skPoint(sketch, "E60.9.0.18", {"position": v(278, -1.84) * mm});
            skPoint(sketch, "E60.9.0.19", {"position": v(277.1, -2.47) * mm});
            skArc(sketch, "E60.9.0.20", {"start": v(281.38, -2.05) * mm, "mid": v(281.61, -2.36) * mm, "end": v(281.98, -2.47) * mm});
            skArc(sketch, "E60.9.0.21", {"start": v(276.3, -2.05) * mm, "mid": v(276.53, -2.36) * mm, "end": v(276.9, -2.47) * mm});
            skPoint(sketch, "E60.9.0.22", {"position": v(276.22, -1.84) * mm});
            skArc(sketch, "E60.9.0.23", {"start": v(278.68, -1.2) * mm, "mid": v(278.3, -1.32) * mm, "end": v(278.07, -1.63) * mm});
            skArc(sketch, "E60.9.0.24", {"start": v(282.4, -2.47) * mm, "mid": v(282.76, -2.36) * mm, "end": v(283, -2.05) * mm});
            skLineSegment(sketch, "E60.9.0.25", {"start": v(276.9, -2.47) * mm, "end": v(277.32, -2.47) * mm});
            skLineSegment(sketch, "E60.9.0.26", {"start": v(276.14, -1.63) * mm, "end": v(276.3, -2.05) * mm});
            skArc(sketch, "E60.9.0.27", {"start": v(283.76, -1.2) * mm, "mid": v(283.39, -1.32) * mm, "end": v(283.15, -1.63) * mm});
            skArc(sketch, "E60.9.0.28", {"start": v(277.32, -2.47) * mm, "mid": v(277.68, -2.36) * mm, "end": v(277.92, -2.05) * mm});
            skLineSegment(sketch, "E60.9.0.29", {"start": v(277.92, -2.05) * mm, "end": v(278.07, -1.63) * mm});
            skLineSegment(sketch, "E60.9.0.30", {"start": v(281.98, -2.47) * mm, "end": v(282.4, -2.47) * mm});
            skLineSegment(sketch, "E60.9.0.31", {"start": v(279.65, -0.98) * mm, "end": v(279.65, -1.27) * mm, "construction": true});
            skLineSegment(sketch, "E60.9.0.32", {"start": v(284.62, -1.2) * mm, "end": v(284.62, -0.98) * mm});
            skLineSegment(sketch, "E60.9.0.33", {"start": v(284.84, -0.98) * mm, "end": v(284.84, -1.2) * mm});
            skLineSegment(sketch, "E60.9.0.34", {"start": v(279.54, -1.2) * mm, "end": v(279.54, -0.98) * mm});
            skLineSegment(sketch, "E60.9.0.35", {"start": v(279.76, -1.1) * mm, "end": v(279.54, -1.1) * mm, "construction": true});
            skLineSegment(sketch, "E60.9.0.36", {"start": v(279.76, -0.98) * mm, "end": v(279.76, -1.2) * mm});
            skLineSegment(sketch, "E60.9.0.37", {"start": v(279.54, -0.98) * mm, "end": v(279.76, -0.98) * mm});
            skLineSegment(sketch, "E60.9.0.38", {"start": v(284.62, -0.98) * mm, "end": v(284.84, -0.98) * mm});
            skPoint(sketch, "E61.9.0.0", {"position": v(294.48, -2.4) * mm});
            skLineSegment(sketch, "E61.9.0.1", {"start": v(295, -1.2) * mm, "end": v(295.86, -1.2) * mm});
            skPoint(sketch, "E61.9.0.2", {"position": v(293.82, -2.4) * mm});
            skLineSegment(sketch, "E61.9.0.3", {"start": v(293.16, -2.05) * mm, "end": v(293.31, -1.63) * mm});
            skArc(sketch, "E61.9.0.4", {"start": v(291.38, -1.63) * mm, "mid": v(291.15, -1.32) * mm, "end": v(290.78, -1.2) * mm});
            skPoint(sketch, "E61.9.0.5", {"position": v(288.28, -1.12) * mm});
            skPoint(sketch, "E61.9.0.6", {"position": v(295.6, -1.12) * mm});
            skPoint(sketch, "E61.9.0.7", {"position": v(288.74, -2.4) * mm});
            skArc(sketch, "E61.9.0.8", {"start": v(286.3, -1.63) * mm, "mid": v(286.07, -1.32) * mm, "end": v(285.7, -1.2) * mm});
            skPoint(sketch, "E61.9.0.9", {"position": v(290.52, -1.12) * mm});
            skLineSegment(sketch, "E61.9.0.10", {"start": v(293.92, -1.2) * mm, "end": v(294.78, -1.2) * mm});
            skLineSegment(sketch, "E61.9.0.11", {"start": v(289.92, -1.2) * mm, "end": v(290.78, -1.2) * mm});
            skPoint(sketch, "E61.9.0.12", {"position": v(295.14, -2.4) * mm});
            skLineSegment(sketch, "E61.9.0.13", {"start": v(291.38, -1.63) * mm, "end": v(291.54, -2.05) * mm});
            skLineSegment(sketch, "E61.9.0.14", {"start": v(288.84, -1.2) * mm, "end": v(289.7, -1.2) * mm});
            skPoint(sketch, "E61.9.0.15", {"position": v(293.36, -1.12) * mm});
            skPoint(sketch, "E61.9.0.16", {"position": v(290.06, -2.4) * mm});
            skPoint(sketch, "E61.9.0.17", {"position": v(291.94, -0.9) * mm});
            skPoint(sketch, "E61.9.0.18", {"position": v(290.29, -1.76) * mm});
            skPoint(sketch, "E61.9.0.19", {"position": v(289.4, -2.4) * mm});
            skArc(sketch, "E61.9.0.20", {"start": v(291.54, -2.05) * mm, "mid": v(291.77, -2.36) * mm, "end": v(292.14, -2.47) * mm});
            skArc(sketch, "E61.9.0.21", {"start": v(286.46, -2.05) * mm, "mid": v(286.7, -2.36) * mm, "end": v(287.06, -2.47) * mm});
            skPoint(sketch, "E61.9.0.22", {"position": v(288.5, -1.76) * mm});
            skArc(sketch, "E61.9.0.23", {"start": v(288.84, -1.2) * mm, "mid": v(288.47, -1.32) * mm, "end": v(288.23, -1.63) * mm});
            skArc(sketch, "E61.9.0.24", {"start": v(292.56, -2.47) * mm, "mid": v(292.92, -2.36) * mm, "end": v(293.16, -2.05) * mm});
            skLineSegment(sketch, "E61.9.0.25", {"start": v(287.06, -2.47) * mm, "end": v(287.48, -2.47) * mm});
            skLineSegment(sketch, "E61.9.0.26", {"start": v(286.3, -1.63) * mm, "end": v(286.46, -2.05) * mm});
            skArc(sketch, "E61.9.0.27", {"start": v(293.92, -1.2) * mm, "mid": v(293.55, -1.32) * mm, "end": v(293.31, -1.63) * mm});
            skArc(sketch, "E61.9.0.28", {"start": v(287.48, -2.47) * mm, "mid": v(287.84, -2.36) * mm, "end": v(288.08, -2.05) * mm});
            skLineSegment(sketch, "E61.9.0.29", {"start": v(288.08, -2.05) * mm, "end": v(288.23, -1.63) * mm});
            skLineSegment(sketch, "E61.9.0.30", {"start": v(292.14, -2.47) * mm, "end": v(292.56, -2.47) * mm});
            skLineSegment(sketch, "E61.9.0.31", {"start": v(291.94, -0.9) * mm, "end": v(291.94, -1.19) * mm, "construction": true});
            skLineSegment(sketch, "E61.9.0.32", {"start": v(294.78, -1.2) * mm, "end": v(294.78, -0.98) * mm});
            skLineSegment(sketch, "E61.9.0.33", {"start": v(295, -0.98) * mm, "end": v(295, -1.2) * mm});
            skLineSegment(sketch, "E61.9.0.34", {"start": v(289.7, -1.2) * mm, "end": v(289.7, -0.98) * mm});
            skLineSegment(sketch, "E61.9.0.35", {"start": v(292.05, -1.01) * mm, "end": v(291.83, -1.01) * mm, "construction": true});
            skLineSegment(sketch, "E61.9.0.36", {"start": v(289.92, -0.98) * mm, "end": v(289.92, -1.2) * mm});
            skLineSegment(sketch, "E61.9.0.37", {"start": v(289.7, -0.98) * mm, "end": v(289.92, -0.98) * mm});
            skLineSegment(sketch, "E61.9.0.38", {"start": v(294.78, -0.98) * mm, "end": v(295, -0.98) * mm});
            skPoint(sketch, "E62.9.0.0", {"position": v(302.96, -2.2) * mm});
            skLineSegment(sketch, "E62.9.0.1", {"start": v(305.16, -1.2) * mm, "end": v(306.02, -1.2) * mm});
            skPoint(sketch, "E62.9.0.2", {"position": v(302.3, -2.2) * mm});
            skLineSegment(sketch, "E62.9.0.3", {"start": v(303.32, -2.05) * mm, "end": v(303.47, -1.63) * mm});
            skArc(sketch, "E62.9.0.4", {"start": v(301.54, -1.63) * mm, "mid": v(301.3, -1.32) * mm, "end": v(300.94, -1.2) * mm});
            skPoint(sketch, "E62.9.0.5", {"position": v(296.76, -0.92) * mm});
            skPoint(sketch, "E62.9.0.6", {"position": v(304.08, -0.92) * mm});
            skPoint(sketch, "E62.9.0.7", {"position": v(297.22, -2.2) * mm});
            skArc(sketch, "E62.9.0.8", {"start": v(296.46, -1.63) * mm, "mid": v(296.23, -1.32) * mm, "end": v(295.86, -1.2) * mm});
            skPoint(sketch, "E62.9.0.9", {"position": v(299, -0.92) * mm});
            skLineSegment(sketch, "E62.9.0.10", {"start": v(304.08, -1.2) * mm, "end": v(304.94, -1.2) * mm});
            skLineSegment(sketch, "E62.9.0.11", {"start": v(300.08, -1.2) * mm, "end": v(300.94, -1.2) * mm});
            skPoint(sketch, "E62.9.0.12", {"position": v(303.62, -2.2) * mm});
            skLineSegment(sketch, "E62.9.0.13", {"start": v(301.54, -1.63) * mm, "end": v(301.7, -2.05) * mm});
            skLineSegment(sketch, "E62.9.0.14", {"start": v(299, -1.2) * mm, "end": v(299.86, -1.2) * mm});
            skPoint(sketch, "E62.9.0.15", {"position": v(301.84, -0.92) * mm});
            skPoint(sketch, "E62.9.0.16", {"position": v(298.54, -2.2) * mm});
            skPoint(sketch, "E62.9.0.17", {"position": v(300.42, -0.7) * mm});
            skPoint(sketch, "E62.9.0.18", {"position": v(298.77, -1.56) * mm});
            skPoint(sketch, "E62.9.0.19", {"position": v(297.88, -2.2) * mm});
            skArc(sketch, "E62.9.0.20", {"start": v(301.7, -2.05) * mm, "mid": v(301.93, -2.36) * mm, "end": v(302.3, -2.47) * mm});
            skArc(sketch, "E62.9.0.21", {"start": v(296.62, -2.05) * mm, "mid": v(296.85, -2.36) * mm, "end": v(297.22, -2.47) * mm});
            skPoint(sketch, "E62.9.0.22", {"position": v(297, -1.56) * mm});
            skArc(sketch, "E62.9.0.23", {"start": v(299, -1.2) * mm, "mid": v(298.63, -1.32) * mm, "end": v(298.4, -1.63) * mm});
            skArc(sketch, "E62.9.0.24", {"start": v(302.72, -2.47) * mm, "mid": v(303.08, -2.36) * mm, "end": v(303.32, -2.05) * mm});
            skLineSegment(sketch, "E62.9.0.25", {"start": v(297.22, -2.47) * mm, "end": v(297.64, -2.47) * mm});
            skLineSegment(sketch, "E62.9.0.26", {"start": v(296.46, -1.63) * mm, "end": v(296.62, -2.05) * mm});
            skArc(sketch, "E62.9.0.27", {"start": v(304.08, -1.2) * mm, "mid": v(303.7, -1.32) * mm, "end": v(303.47, -1.63) * mm});
            skArc(sketch, "E62.9.0.28", {"start": v(297.64, -2.47) * mm, "mid": v(298, -2.36) * mm, "end": v(298.24, -2.05) * mm});
            skLineSegment(sketch, "E62.9.0.29", {"start": v(298.24, -2.05) * mm, "end": v(298.4, -1.63) * mm});
            skLineSegment(sketch, "E62.9.0.30", {"start": v(302.3, -2.47) * mm, "end": v(302.72, -2.47) * mm});
            skLineSegment(sketch, "E62.9.0.31", {"start": v(300.42, -0.7) * mm, "end": v(300.42, -0.99) * mm, "construction": true});
            skLineSegment(sketch, "E62.9.0.32", {"start": v(304.94, -1.2) * mm, "end": v(304.94, -0.98) * mm});
            skLineSegment(sketch, "E62.9.0.33", {"start": v(305.16, -0.98) * mm, "end": v(305.16, -1.2) * mm});
            skLineSegment(sketch, "E62.9.0.34", {"start": v(299.86, -1.2) * mm, "end": v(299.86, -0.98) * mm});
            skLineSegment(sketch, "E62.9.0.35", {"start": v(300.53, -0.8) * mm, "end": v(300.3, -0.8) * mm, "construction": true});
            skLineSegment(sketch, "E62.9.0.36", {"start": v(300.08, -0.98) * mm, "end": v(300.08, -1.2) * mm});
            skLineSegment(sketch, "E62.9.0.37", {"start": v(299.86, -0.98) * mm, "end": v(300.08, -0.98) * mm});
            skLineSegment(sketch, "E62.9.0.38", {"start": v(304.94, -0.98) * mm, "end": v(305.16, -0.98) * mm});
            skLineSegment(sketch, "E63.MirrorCS", {"start": v(86.45, 51.8) * mm, "end": v(86.45, 52.03) * mm});
            skLineSegment(sketch, "E64.MirrorCS", {"start": v(86.23, 51.8) * mm, "end": v(86.45, 51.8) * mm});
            skArc(sketch, "E65.MirrorCS", {"start": v(83, 52.88) * mm, "mid": v(83.23, 53.18) * mm, "end": v(83.6, 53.3) * mm});
            skArc(sketch, "E66.MirrorCS", {"start": v(88.07, 52.88) * mm, "mid": v(88.3, 53.18) * mm, "end": v(88.67, 53.3) * mm});
            skLineSegment(sketch, "E67.MirrorCS", {"start": v(83.6, 53.3) * mm, "end": v(84.01, 53.3) * mm});
            skLineSegment(sketch, "E68.MirrorCS", {"start": v(81.17, 52.03) * mm, "end": v(81.17, 51.81) * mm});
            skLineSegment(sketch, "E69.MirrorCS", {"start": v(86.23, 52.03) * mm, "end": v(86.23, 51.8) * mm});
            skLineSegment(sketch, "E70.MirrorCS", {"start": v(85.37, 52.03) * mm, "end": v(86.23, 52.03) * mm});
            skLineSegment(sketch, "E71.MirrorCS", {"start": v(81.39, 52.03) * mm, "end": v(82.25, 52.03) * mm});
            skArc(sketch, "E72.MirrorCS", {"start": v(85.37, 52.03) * mm, "mid": v(85, 52.15) * mm, "end": v(84.77, 52.45) * mm});
            skArc(sketch, "E73.MirrorCS", {"start": v(89.1, 53.3) * mm, "mid": v(89.46, 53.18) * mm, "end": v(89.7, 52.88) * mm});
            skArc(sketch, "E74.MirrorCS", {"start": v(90.45, 52.03) * mm, "mid": v(90.08, 52.15) * mm, "end": v(89.85, 52.45) * mm});
            skLineSegment(sketch, "E75.MirrorCS", {"start": v(86.45, 51.92) * mm, "end": v(86.23, 51.92) * mm, "construction": true});
            skLineSegment(sketch, "E76.MirrorCS", {"start": v(81.39, 51.81) * mm, "end": v(81.39, 52.03) * mm});
            skLineSegment(sketch, "E77.MirrorCS", {"start": v(82.84, 52.45) * mm, "end": v(83, 52.88) * mm});
            skLineSegment(sketch, "E78.MirrorCS", {"start": v(87.92, 52.45) * mm, "end": v(88.07, 52.88) * mm});
            skLineSegment(sketch, "E79.MirrorCS", {"start": v(86.45, 52.03) * mm, "end": v(87.31, 52.03) * mm});
            skLineSegment(sketch, "E80.MirrorCS", {"start": v(25.37, 52.06) * mm, "end": v(25.37, 51.84) * mm});
            skLineSegment(sketch, "E81.MirrorCS", {"start": v(89.7, 52.88) * mm, "end": v(89.85, 52.45) * mm});
            skLineSegment(sketch, "E82.MirrorCS", {"start": v(55.8, 52.04) * mm, "end": v(55.8, 51.82) * mm});
            skArc(sketch, "E83.MirrorCS", {"start": v(82.84, 52.45) * mm, "mid": v(82.6, 52.15) * mm, "end": v(82.23, 52.03) * mm});
            skLineSegment(sketch, "E84.MirrorCS", {"start": v(86.34, 51.8) * mm, "end": v(86.34, 52.1) * mm, "construction": true});
            skLineSegment(sketch, "E85.MirrorCS", {"start": v(84.61, 52.88) * mm, "end": v(84.77, 52.45) * mm});
            skLineSegment(sketch, "E86.MirrorCS", {"start": v(81.17, 51.81) * mm, "end": v(81.39, 51.81) * mm});
            skLineSegment(sketch, "E87.MirrorCS", {"start": v(88.67, 53.3) * mm, "end": v(89.1, 53.3) * mm});
            skArc(sketch, "E88.MirrorCS", {"start": v(87.92, 52.45) * mm, "mid": v(87.68, 52.15) * mm, "end": v(87.31, 52.03) * mm});
            skArc(sketch, "E89.MirrorCS", {"start": v(84.01, 53.3) * mm, "mid": v(84.38, 53.18) * mm, "end": v(84.61, 52.88) * mm});
            skLineSegment(sketch, "E90.MirrorCS", {"start": v(56.02, 52.04) * mm, "end": v(56.88, 52.04) * mm});
            skLineSegment(sketch, "E91.MirrorCS", {"start": v(30.45, 52.06) * mm, "end": v(30.45, 51.84) * mm});
            skLineSegment(sketch, "E92.MirrorCS", {"start": v(56.02, 51.82) * mm, "end": v(56.02, 52.04) * mm});
            skLineSegment(sketch, "E93.MirrorCS", {"start": v(50.96, 52.05) * mm, "end": v(51.82, 52.05) * mm});
            skArc(sketch, "E94.MirrorCS", {"start": v(58.66, 53.31) * mm, "mid": v(59.03, 53.2) * mm, "end": v(59.26, 52.9) * mm});
            skLineSegment(sketch, "E95.MirrorCS", {"start": v(54.94, 52.04) * mm, "end": v(55.8, 52.04) * mm});
            skLineSegment(sketch, "E96.MirrorCS", {"start": v(25.6, 51.84) * mm, "end": v(25.6, 52.06) * mm});
            skLineSegment(sketch, "E97.MirrorCS", {"start": v(57.48, 52.47) * mm, "end": v(57.64, 52.9) * mm});
            skLineSegment(sketch, "E98.MirrorCS", {"start": v(53.16, 53.31) * mm, "end": v(53.58, 53.31) * mm});
            skArc(sketch, "E99.MirrorCS", {"start": v(52.56, 52.9) * mm, "mid": v(52.8, 53.2) * mm, "end": v(53.16, 53.31) * mm});
            skLineSegment(sketch, "E100.MirrorCS", {"start": v(25.37, 51.84) * mm, "end": v(25.6, 51.84) * mm});
            skArc(sketch, "E101.MirrorCS", {"start": v(70.16, 52.04) * mm, "mid": v(69.8, 52.16) * mm, "end": v(69.56, 52.46) * mm});
            skLineSegment(sketch, "E102.MirrorCS", {"start": v(45.66, 52.05) * mm, "end": v(45.66, 51.83) * mm});
            skLineSegment(sketch, "E103.MirrorCS", {"start": v(76.09, 52.03) * mm, "end": v(76.09, 51.81) * mm});
            skLineSegment(sketch, "E104.MirrorCS", {"start": v(60.02, 52.04) * mm, "end": v(60.88, 52.04) * mm});
            skLineSegment(sketch, "E105.MirrorCS", {"start": v(55.8, 51.82) * mm, "end": v(56.02, 51.82) * mm});
            skLineSegment(sketch, "E106.MirrorCS", {"start": v(30.67, 51.84) * mm, "end": v(30.67, 52.06) * mm});
            skLineSegment(sketch, "E107.MirrorCS", {"start": v(35.51, 51.83) * mm, "end": v(35.73, 51.83) * mm});
            skArc(sketch, "E108.MirrorCS", {"start": v(54.94, 52.04) * mm, "mid": v(54.57, 52.16) * mm, "end": v(54.34, 52.47) * mm});
            skLineSegment(sketch, "E109.MirrorCS", {"start": v(61.1, 51.82) * mm, "end": v(61.1, 52.04) * mm});
            skLineSegment(sketch, "E110.MirrorCS", {"start": v(142.1, 52.04) * mm, "end": v(142.1, 51.82) * mm});
            skArc(sketch, "E111.MirrorCS", {"start": v(28.23, 53.33) * mm, "mid": v(28.6, 53.21) * mm, "end": v(28.83, 52.9) * mm});
            skLineSegment(sketch, "E112.MirrorCS", {"start": v(77.77, 52.46) * mm, "end": v(77.93, 52.88) * mm});
            skLineSegment(sketch, "E113.MirrorCS", {"start": v(50.96, 51.83) * mm, "end": v(50.96, 52.05) * mm});
            skLineSegment(sketch, "E114.MirrorCS", {"start": v(58.24, 53.31) * mm, "end": v(58.66, 53.31) * mm});
            skLineSegment(sketch, "E115.MirrorCS", {"start": v(76.3, 51.81) * mm, "end": v(76.3, 52.03) * mm});
            skLineSegment(sketch, "E116.MirrorCS", {"start": v(56.02, 51.93) * mm, "end": v(55.8, 51.93) * mm, "construction": true});
            skLineSegment(sketch, "E117.MirrorCS", {"start": v(106.54, 52.02) * mm, "end": v(106.54, 51.8) * mm});
            skLineSegment(sketch, "E118.MirrorCS", {"start": v(27.8, 53.33) * mm, "end": v(28.23, 53.33) * mm});
            skLineSegment(sketch, "E119.MirrorCS", {"start": v(78.53, 53.3) * mm, "end": v(78.95, 53.3) * mm});
            skLineSegment(sketch, "E120.MirrorCS", {"start": v(29.59, 52.06) * mm, "end": v(30.45, 52.06) * mm});
            skArc(sketch, "E121.MirrorCS", {"start": v(77.93, 52.88) * mm, "mid": v(78.16, 53.19) * mm, "end": v(78.53, 53.3) * mm});
            skLineSegment(sketch, "E122.MirrorCS", {"start": v(52.4, 52.47) * mm, "end": v(52.56, 52.9) * mm});
            skLineSegment(sketch, "E123.MirrorCS", {"start": v(142.32, 51.82) * mm, "end": v(142.32, 52.04) * mm});
            skArc(sketch, "E124.MirrorCS", {"start": v(113.46, 52.86) * mm, "mid": v(113.69, 53.17) * mm, "end": v(114.06, 53.28) * mm});
            skLineSegment(sketch, "E125.MirrorCS", {"start": v(76.09, 51.81) * mm, "end": v(76.3, 51.81) * mm});
            skLineSegment(sketch, "E126.MirrorCS", {"start": v(62.55, 52.46) * mm, "end": v(62.7, 52.89) * mm});
            skArc(sketch, "E127.MirrorCS", {"start": v(72.85, 52.88) * mm, "mid": v(73.08, 53.19) * mm, "end": v(73.45, 53.3) * mm});
            skArc(sketch, "E128.MirrorCS", {"start": v(52.4, 52.47) * mm, "mid": v(52.17, 52.16) * mm, "end": v(51.8, 52.04) * mm});
            skLineSegment(sketch, "E129.MirrorCS", {"start": v(59.26, 52.9) * mm, "end": v(59.42, 52.47) * mm});
            skLineSegment(sketch, "E130.MirrorCS", {"start": v(91.31, 51.8) * mm, "end": v(91.53, 51.8) * mm});
            skLineSegment(sketch, "E131.MirrorCS", {"start": v(63.3, 53.3) * mm, "end": v(63.72, 53.3) * mm});
            skLineSegment(sketch, "E132.MirrorCS", {"start": v(80.3, 52.03) * mm, "end": v(81.17, 52.03) * mm});
            skLineSegment(sketch, "E133.MirrorCS", {"start": v(27.05, 52.48) * mm, "end": v(27.2, 52.9) * mm});
            skLineSegment(sketch, "E134.MirrorCS", {"start": v(40.6, 51.83) * mm, "end": v(40.81, 51.83) * mm});
            skLineSegment(sketch, "E135.MirrorCS", {"start": v(137.02, 52.04) * mm, "end": v(137.02, 51.82) * mm});
            skLineSegment(sketch, "E136.MirrorCS", {"start": v(22.73, 53.33) * mm, "end": v(23.15, 53.33) * mm});
            skArc(sketch, "E137.MirrorCS", {"start": v(57.48, 52.47) * mm, "mid": v(57.25, 52.16) * mm, "end": v(56.88, 52.04) * mm});
            skLineSegment(sketch, "E138.MirrorCS", {"start": v(25.48, 51.84) * mm, "end": v(25.48, 52.13) * mm, "construction": true});
            skLineSegment(sketch, "E139.MirrorCS", {"start": v(71.02, 52.04) * mm, "end": v(71.02, 51.82) * mm});
            skArc(sketch, "E140.MirrorCS", {"start": v(57.64, 52.9) * mm, "mid": v(57.87, 53.2) * mm, "end": v(58.24, 53.31) * mm});
            skLineSegment(sketch, "E141.MirrorCS", {"start": v(60.88, 52.04) * mm, "end": v(60.88, 51.82) * mm});
            skLineSegment(sketch, "E142.MirrorCS", {"start": v(24.5, 52.06) * mm, "end": v(25.37, 52.06) * mm});
            skLineSegment(sketch, "E143.MirrorCS", {"start": v(45.88, 51.83) * mm, "end": v(45.88, 52.05) * mm});
            skLineSegment(sketch, "E144.MirrorCS", {"start": v(35.51, 52.05) * mm, "end": v(35.51, 51.83) * mm});
            skLineSegment(sketch, "E145.MirrorCS", {"start": v(55.91, 51.82) * mm, "end": v(55.91, 52.11) * mm, "construction": true});
            skLineSegment(sketch, "E146.MirrorCS", {"start": v(75.23, 52.03) * mm, "end": v(76.09, 52.03) * mm});
            skArc(sketch, "E147.MirrorCS", {"start": v(27.05, 52.48) * mm, "mid": v(26.82, 52.18) * mm, "end": v(26.45, 52.06) * mm});
            skLineSegment(sketch, "E148.MirrorCS", {"start": v(30.45, 51.84) * mm, "end": v(30.67, 51.84) * mm});
            skLineSegment(sketch, "E149.MirrorCS", {"start": v(79.55, 52.88) * mm, "end": v(79.7, 52.46) * mm});
            skArc(sketch, "E150.MirrorCS", {"start": v(22.13, 52.9) * mm, "mid": v(22.36, 53.21) * mm, "end": v(22.73, 53.33) * mm});
            skLineSegment(sketch, "E151.MirrorCS", {"start": v(111.62, 52.02) * mm, "end": v(111.62, 51.8) * mm});
            skLineSegment(sketch, "E152.MirrorCS", {"start": v(54.18, 52.9) * mm, "end": v(54.34, 52.47) * mm});
            skArc(sketch, "E153.MirrorCS", {"start": v(53.58, 53.31) * mm, "mid": v(53.95, 53.2) * mm, "end": v(54.18, 52.9) * mm});
            skArc(sketch, "E154.MirrorCS", {"start": v(60.02, 52.04) * mm, "mid": v(59.65, 52.16) * mm, "end": v(59.42, 52.47) * mm});
            skLineSegment(sketch, "E155.MirrorCS", {"start": v(72.7, 52.46) * mm, "end": v(72.85, 52.88) * mm});
            skArc(sketch, "E156.MirrorCS", {"start": v(78.95, 53.3) * mm, "mid": v(79.32, 53.19) * mm, "end": v(79.55, 52.88) * mm});
            skLineSegment(sketch, "E157.MirrorCS", {"start": v(116.7, 51.8) * mm, "end": v(116.92, 51.8) * mm});
            skLineSegment(sketch, "E158.MirrorCS", {"start": v(108.98, 53.3) * mm, "end": v(109.4, 53.3) * mm});
            skArc(sketch, "E159.MirrorCS", {"start": v(80.3, 52.03) * mm, "mid": v(79.94, 52.15) * mm, "end": v(79.7, 52.46) * mm});
            skArc(sketch, "E160.MirrorCS", {"start": v(23.15, 53.33) * mm, "mid": v(23.52, 53.21) * mm, "end": v(23.75, 52.9) * mm});
            skArc(sketch, "E161.MirrorCS", {"start": v(29.59, 52.06) * mm, "mid": v(29.22, 52.18) * mm, "end": v(28.99, 52.48) * mm});
            skArc(sketch, "E162.MirrorCS", {"start": v(143.94, 52.89) * mm, "mid": v(144.17, 53.2) * mm, "end": v(144.54, 53.3) * mm});
            skLineSegment(sketch, "E163.MirrorCS", {"start": v(137.24, 51.82) * mm, "end": v(137.24, 52.04) * mm});
            skArc(sketch, "E164.MirrorCS", {"start": v(63.72, 53.3) * mm, "mid": v(64.1, 53.2) * mm, "end": v(64.33, 52.89) * mm});
            skLineSegment(sketch, "E165.MirrorCS", {"start": v(45.66, 51.83) * mm, "end": v(45.88, 51.83) * mm});
            skArc(sketch, "E166.MirrorCS", {"start": v(72.7, 52.46) * mm, "mid": v(72.46, 52.15) * mm, "end": v(72.1, 52.03) * mm});
            skLineSegment(sketch, "E167.MirrorCS", {"start": v(147.18, 52.04) * mm, "end": v(147.18, 51.82) * mm});
            skArc(sketch, "E168.MirrorCS", {"start": v(75.23, 52.03) * mm, "mid": v(74.86, 52.15) * mm, "end": v(74.63, 52.46) * mm});
            skLineSegment(sketch, "E169.MirrorCS", {"start": v(21.97, 52.48) * mm, "end": v(22.13, 52.9) * mm});
            skLineSegment(sketch, "E170.MirrorCS", {"start": v(105.67, 52.02) * mm, "end": v(106.54, 52.02) * mm});
            skLineSegment(sketch, "E171.MirrorCS", {"start": v(71.25, 51.82) * mm, "end": v(71.25, 52.04) * mm});
            skLineSegment(sketch, "E172.MirrorCS", {"start": v(60.88, 51.82) * mm, "end": v(61.1, 51.82) * mm});
            skLineSegment(sketch, "E173.MirrorCS", {"start": v(25.6, 51.95) * mm, "end": v(25.37, 51.95) * mm, "construction": true});
            skLineSegment(sketch, "E174.MirrorCS", {"start": v(73.45, 53.3) * mm, "end": v(73.87, 53.3) * mm});
            skArc(sketch, "E175.MirrorCS", {"start": v(38.37, 53.32) * mm, "mid": v(38.74, 53.2) * mm, "end": v(38.97, 52.9) * mm});
            skArc(sketch, "E176.MirrorCS", {"start": v(49.88, 52.05) * mm, "mid": v(49.5, 52.17) * mm, "end": v(49.27, 52.47) * mm});
            skLineSegment(sketch, "E177.MirrorCS", {"start": v(66.17, 51.82) * mm, "end": v(66.17, 52.04) * mm});
            skLineSegment(sketch, "E178.MirrorCS", {"start": v(141.23, 52.04) * mm, "end": v(142.1, 52.04) * mm});
            skLineSegment(sketch, "E179.MirrorCS", {"start": v(50.74, 52.05) * mm, "end": v(50.74, 51.83) * mm});
            skArc(sketch, "E180.MirrorCS", {"start": v(24.5, 52.06) * mm, "mid": v(24.14, 52.18) * mm, "end": v(23.9, 52.48) * mm});
            skLineSegment(sketch, "E181.MirrorCS", {"start": v(91.31, 52.03) * mm, "end": v(91.31, 51.8) * mm});
            skArc(sketch, "E182.MirrorCS", {"start": v(77.77, 52.46) * mm, "mid": v(77.54, 52.15) * mm, "end": v(77.17, 52.03) * mm});
            skLineSegment(sketch, "E183.MirrorCS", {"start": v(76.2, 51.81) * mm, "end": v(76.2, 52.1) * mm, "construction": true});
            skLineSegment(sketch, "E184.MirrorCS", {"start": v(32.87, 53.32) * mm, "end": v(33.3, 53.32) * mm});
            skLineSegment(sketch, "E185.MirrorCS", {"start": v(152.48, 51.82) * mm, "end": v(152.48, 52.04) * mm});
            skLineSegment(sketch, "E186.MirrorCS", {"start": v(116.92, 51.8) * mm, "end": v(116.92, 52.01) * mm});
            skLineSegment(sketch, "E187.MirrorCS", {"start": v(137.02, 51.82) * mm, "end": v(137.24, 51.82) * mm});
            skLineSegment(sketch, "E188.MirrorCS", {"start": v(111.84, 51.8) * mm, "end": v(111.84, 52.01) * mm});
            skLineSegment(sketch, "E189.MirrorCS", {"start": v(96.38, 52.02) * mm, "end": v(96.38, 51.8) * mm});
            skLineSegment(sketch, "E190.MirrorCS", {"start": v(114.06, 53.28) * mm, "end": v(114.48, 53.28) * mm});
            skArc(sketch, "E191.MirrorCS", {"start": v(68.8, 53.3) * mm, "mid": v(69.17, 53.2) * mm, "end": v(69.4, 52.89) * mm});
            skLineSegment(sketch, "E192.MirrorCS", {"start": v(40.6, 52.05) * mm, "end": v(40.6, 51.83) * mm});
            skLineSegment(sketch, "E193.MirrorCS", {"start": v(74.47, 52.88) * mm, "end": v(74.63, 52.46) * mm});
            skArc(sketch, "E194.MirrorCS", {"start": v(32.27, 52.9) * mm, "mid": v(32.5, 53.2) * mm, "end": v(32.87, 53.32) * mm});
            skLineSegment(sketch, "E195.MirrorCS", {"start": v(35.73, 51.83) * mm, "end": v(35.73, 52.05) * mm});
            skArc(sketch, "E196.MirrorCS", {"start": v(27.2, 52.9) * mm, "mid": v(27.44, 53.21) * mm, "end": v(27.8, 53.33) * mm});
            skLineSegment(sketch, "E197.MirrorCS", {"start": v(28.83, 52.9) * mm, "end": v(28.99, 52.48) * mm});
            skArc(sketch, "E198.MirrorCS", {"start": v(21.97, 52.48) * mm, "mid": v(21.74, 52.18) * mm, "end": v(21.37, 52.06) * mm});
            skLineSegment(sketch, "E199.MirrorCS", {"start": v(23.75, 52.9) * mm, "end": v(23.9, 52.48) * mm});
            skLineSegment(sketch, "E200.MirrorCS", {"start": v(142.1, 51.82) * mm, "end": v(142.32, 51.82) * mm});
            skLineSegment(sketch, "E201.MirrorCS", {"start": v(65.94, 52.04) * mm, "end": v(65.94, 51.82) * mm});
            skLineSegment(sketch, "E202.MirrorCS", {"start": v(70.16, 52.04) * mm, "end": v(71.02, 52.04) * mm});
            skLineSegment(sketch, "E203.MirrorCS", {"start": v(25.6, 52.06) * mm, "end": v(26.45, 52.06) * mm});
            skLineSegment(sketch, "E204.MirrorCS", {"start": v(116.7, 52.01) * mm, "end": v(116.7, 51.8) * mm});
            skLineSegment(sketch, "E205.MirrorCS", {"start": v(115.83, 52.01) * mm, "end": v(116.7, 52.01) * mm});
            skArc(sketch, "E206.MirrorCS", {"start": v(118.54, 52.86) * mm, "mid": v(118.77, 53.17) * mm, "end": v(119.14, 53.28) * mm});
            skLineSegment(sketch, "E207.MirrorCS", {"start": v(49.12, 52.9) * mm, "end": v(49.27, 52.47) * mm});
            skArc(sketch, "E208.MirrorCS", {"start": v(144.96, 53.3) * mm, "mid": v(145.32, 53.2) * mm, "end": v(145.56, 52.89) * mm});
            skLineSegment(sketch, "E209.MirrorCS", {"start": v(101.46, 52.02) * mm, "end": v(101.46, 51.8) * mm});
            skArc(sketch, "E210.MirrorCS", {"start": v(108.38, 52.87) * mm, "mid": v(108.6, 53.18) * mm, "end": v(108.98, 53.3) * mm});
            skLineSegment(sketch, "E211.MirrorCS", {"start": v(110, 52.87) * mm, "end": v(110.15, 52.45) * mm});
            skLineSegment(sketch, "E212.MirrorCS", {"start": v(121.78, 51.8) * mm, "end": v(122, 51.8) * mm});
            skLineSegment(sketch, "E213.MirrorCS", {"start": v(148.86, 52.46) * mm, "end": v(149.02, 52.89) * mm});
            skLineSegment(sketch, "E214.MirrorCS", {"start": v(61.1, 52.04) * mm, "end": v(61.96, 52.04) * mm});
            skArc(sketch, "E215.MirrorCS", {"start": v(139.88, 53.3) * mm, "mid": v(140.24, 53.2) * mm, "end": v(140.48, 52.89) * mm});
            skArc(sketch, "E216.MirrorCS", {"start": v(105.67, 52.02) * mm, "mid": v(105.3, 52.14) * mm, "end": v(105.07, 52.45) * mm});
            skLineSegment(sketch, "E217.MirrorCS", {"start": v(129.3, 53.3) * mm, "end": v(129.72, 53.3) * mm});
            skLineSegment(sketch, "E218.MirrorCS", {"start": v(68.39, 53.3) * mm, "end": v(68.8, 53.3) * mm});
            skArc(sketch, "E219.MirrorCS", {"start": v(155.12, 53.3) * mm, "mid": v(155.48, 53.2) * mm, "end": v(155.72, 52.89) * mm});
            skLineSegment(sketch, "E220.MirrorCS", {"start": v(64.33, 52.89) * mm, "end": v(64.48, 52.46) * mm});
            skLineSegment(sketch, "E221.MirrorCS", {"start": v(162.42, 52.04) * mm, "end": v(162.42, 51.82) * mm});
            skLineSegment(sketch, "E222.MirrorCS", {"start": v(110.75, 52.02) * mm, "end": v(111.62, 52.02) * mm});
            skLineSegment(sketch, "E223.MirrorCS", {"start": v(131.94, 52.04) * mm, "end": v(131.94, 51.82) * mm});
            skLineSegment(sketch, "E224.MirrorCS", {"start": v(67.63, 52.46) * mm, "end": v(67.78, 52.89) * mm});
            skLineSegment(sketch, "E225.MirrorCS", {"start": v(65.94, 51.82) * mm, "end": v(66.17, 51.82) * mm});
            skLineSegment(sketch, "E226.MirrorCS", {"start": v(126.86, 52.04) * mm, "end": v(126.86, 51.82) * mm});
            skLineSegment(sketch, "E227.MirrorCS", {"start": v(147.4, 51.82) * mm, "end": v(147.4, 52.04) * mm});
            skArc(sketch, "E228.MirrorCS", {"start": v(65.08, 52.04) * mm, "mid": v(64.72, 52.16) * mm, "end": v(64.48, 52.46) * mm});
            skLineSegment(sketch, "E229.MirrorCS", {"start": v(126.86, 51.82) * mm, "end": v(127.08, 51.82) * mm});
            skLineSegment(sketch, "E230.MirrorCS", {"start": v(49.88, 52.05) * mm, "end": v(50.74, 52.05) * mm});
            skLineSegment(sketch, "E231.MirrorCS", {"start": v(144.54, 53.3) * mm, "end": v(144.96, 53.3) * mm});
            skLineSegment(sketch, "E232.MirrorCS", {"start": v(111.62, 51.8) * mm, "end": v(111.84, 51.8) * mm});
            skArc(sketch, "E233.MirrorCS", {"start": v(33.3, 53.32) * mm, "mid": v(33.66, 53.2) * mm, "end": v(33.9, 52.9) * mm});
            skArc(sketch, "E234.MirrorCS", {"start": v(131.07, 52.04) * mm, "mid": v(130.7, 52.16) * mm, "end": v(130.47, 52.46) * mm});
            skLineSegment(sketch, "E235.MirrorCS", {"start": v(138.7, 52.46) * mm, "end": v(138.86, 52.89) * mm});
            skLineSegment(sketch, "E236.MirrorCS", {"start": v(96.6, 51.8) * mm, "end": v(96.6, 52.02) * mm});
            skArc(sketch, "E237.MirrorCS", {"start": v(153.94, 52.46) * mm, "mid": v(153.7, 52.16) * mm, "end": v(153.34, 52.04) * mm});
            skArc(sketch, "E238.MirrorCS", {"start": v(37.35, 52.9) * mm, "mid": v(37.59, 53.2) * mm, "end": v(37.95, 53.32) * mm});
            skArc(sketch, "E239.MirrorCS", {"start": v(146.31, 52.04) * mm, "mid": v(145.95, 52.16) * mm, "end": v(145.71, 52.46) * mm});
            skLineSegment(sketch, "E240.MirrorCS", {"start": v(66.05, 51.82) * mm, "end": v(66.05, 52.1) * mm, "construction": true});
            skLineSegment(sketch, "E241.MirrorCS", {"start": v(91.53, 51.8) * mm, "end": v(91.53, 52.03) * mm});
            skLineSegment(sketch, "E242.MirrorCS", {"start": v(35.62, 51.83) * mm, "end": v(35.62, 52.12) * mm, "construction": true});
            skLineSegment(sketch, "E243.MirrorCS", {"start": v(76.3, 51.92) * mm, "end": v(76.09, 51.92) * mm, "construction": true});
            skLineSegment(sketch, "E244.MirrorCS", {"start": v(35.73, 52.05) * mm, "end": v(36.6, 52.05) * mm});
            skArc(sketch, "E245.MirrorCS", {"start": v(150.04, 53.3) * mm, "mid": v(150.4, 53.2) * mm, "end": v(150.64, 52.89) * mm});
            skLineSegment(sketch, "E246.MirrorCS", {"start": v(69.4, 52.89) * mm, "end": v(69.56, 52.46) * mm});
            skLineSegment(sketch, "E247.MirrorCS", {"start": v(113.3, 52.44) * mm, "end": v(113.46, 52.86) * mm});
            skLineSegment(sketch, "E248.MirrorCS", {"start": v(71.02, 51.82) * mm, "end": v(71.25, 51.82) * mm});
            skArc(sketch, "E249.MirrorCS", {"start": v(141.23, 52.04) * mm, "mid": v(140.87, 52.16) * mm, "end": v(140.63, 52.46) * mm});
            skLineSegment(sketch, "E250.MirrorCS", {"start": v(47.34, 52.47) * mm, "end": v(47.5, 52.9) * mm});
            skLineSegment(sketch, "E251.MirrorCS", {"start": v(136.15, 52.04) * mm, "end": v(137.02, 52.04) * mm});
            skLineSegment(sketch, "E252.MirrorCS", {"start": v(137.24, 51.9) * mm, "end": v(137.02, 51.9) * mm, "construction": true});
            skArc(sketch, "E253.MirrorCS", {"start": v(133.78, 52.89) * mm, "mid": v(134, 53.2) * mm, "end": v(134.38, 53.3) * mm});
            skLineSegment(sketch, "E254.MirrorCS", {"start": v(32.12, 52.48) * mm, "end": v(32.27, 52.9) * mm});
            skLineSegment(sketch, "E255.MirrorCS", {"start": v(45.77, 51.83) * mm, "end": v(45.77, 52.12) * mm, "construction": true});
            skArc(sketch, "E256.MirrorCS", {"start": v(73.87, 53.3) * mm, "mid": v(74.24, 53.19) * mm, "end": v(74.47, 52.88) * mm});
            skLineSegment(sketch, "E257.MirrorCS", {"start": v(40.81, 51.83) * mm, "end": v(40.81, 52.05) * mm});
            skArc(sketch, "E258.MirrorCS", {"start": v(62.55, 52.46) * mm, "mid": v(62.31, 52.16) * mm, "end": v(61.95, 52.04) * mm});
            skLineSegment(sketch, "E259.MirrorCS", {"start": v(142.74, 51.46) * mm, "end": v(142.52, 51.46) * mm, "construction": true});
            skArc(sketch, "E260.MirrorCS", {"start": v(138.86, 52.89) * mm, "mid": v(139.09, 53.2) * mm, "end": v(139.46, 53.3) * mm});
            skLineSegment(sketch, "E261.MirrorCS", {"start": v(38.97, 52.9) * mm, "end": v(39.13, 52.48) * mm});
            skLineSegment(sketch, "E262.MirrorCS", {"start": v(76.3, 52.03) * mm, "end": v(77.17, 52.03) * mm});
            skLineSegment(sketch, "E263.MirrorCS", {"start": v(152.26, 52.04) * mm, "end": v(152.26, 51.82) * mm});
            skArc(sketch, "E264.MirrorCS", {"start": v(108.22, 52.45) * mm, "mid": v(107.99, 52.14) * mm, "end": v(107.62, 52.02) * mm});
            skLineSegment(sketch, "E265.MirrorCS", {"start": v(71.25, 52.04) * mm, "end": v(72.1, 52.04) * mm});
            skLineSegment(sketch, "E266.MirrorCS", {"start": v(106.76, 51.8) * mm, "end": v(106.76, 52.02) * mm});
            skLineSegment(sketch, "E267.MirrorCS", {"start": v(149.62, 53.3) * mm, "end": v(150.04, 53.3) * mm});
            skLineSegment(sketch, "E268.MirrorCS", {"start": v(143.78, 52.46) * mm, "end": v(143.94, 52.89) * mm});
            skArc(sketch, "E269.MirrorCS", {"start": v(138.7, 52.46) * mm, "mid": v(138.47, 52.16) * mm, "end": v(138.1, 52.04) * mm});
            skArc(sketch, "E270.MirrorCS", {"start": v(110.75, 52.02) * mm, "mid": v(110.39, 52.14) * mm, "end": v(110.15, 52.45) * mm});
            skLineSegment(sketch, "E271.MirrorCS", {"start": v(116.8, 51.8) * mm, "end": v(116.8, 52.08) * mm, "construction": true});
            skArc(sketch, "E272.MirrorCS", {"start": v(148.86, 52.46) * mm, "mid": v(148.63, 52.16) * mm, "end": v(148.26, 52.04) * mm});
            skLineSegment(sketch, "E273.MirrorCS", {"start": v(152.48, 52.04) * mm, "end": v(153.34, 52.04) * mm});
            skLineSegment(sketch, "E274.MirrorCS", {"start": v(111.84, 52.01) * mm, "end": v(112.7, 52.01) * mm});
            skLineSegment(sketch, "E275.MirrorCS", {"start": v(119.14, 53.28) * mm, "end": v(119.56, 53.28) * mm});
            skLineSegment(sketch, "E276.MirrorCS", {"start": v(44.8, 52.05) * mm, "end": v(45.66, 52.05) * mm});
            skLineSegment(sketch, "E277.MirrorCS", {"start": v(20.53, 52.06) * mm, "end": v(21.39, 52.06) * mm});
            skArc(sketch, "E278.MirrorCS", {"start": v(118.38, 52.44) * mm, "mid": v(118.15, 52.13) * mm, "end": v(117.78, 52.01) * mm});
            skLineSegment(sketch, "E279.MirrorCS", {"start": v(130.32, 52.89) * mm, "end": v(130.47, 52.46) * mm});
            skLineSegment(sketch, "E280.MirrorCS", {"start": v(132.16, 51.82) * mm, "end": v(132.16, 52.04) * mm});
            skArc(sketch, "E281.MirrorCS", {"start": v(32.12, 52.48) * mm, "mid": v(31.88, 52.17) * mm, "end": v(31.51, 52.05) * mm});
            skArc(sketch, "E282.MirrorCS", {"start": v(47.5, 52.9) * mm, "mid": v(47.73, 53.2) * mm, "end": v(48.1, 53.32) * mm});
            skLineSegment(sketch, "E283.MirrorCS", {"start": v(137.24, 52.04) * mm, "end": v(138.1, 52.04) * mm});
            skLineSegment(sketch, "E284.MirrorCS", {"start": v(37.2, 52.48) * mm, "end": v(37.35, 52.9) * mm});
            skLineSegment(sketch, "E285.MirrorCS", {"start": v(50.74, 51.83) * mm, "end": v(50.96, 51.83) * mm});
            skLineSegment(sketch, "E286.MirrorCS", {"start": v(140.48, 52.89) * mm, "end": v(140.63, 52.46) * mm});
            skArc(sketch, "E287.MirrorCS", {"start": v(114.48, 53.28) * mm, "mid": v(114.84, 53.17) * mm, "end": v(115.08, 52.86) * mm});
            skArc(sketch, "E288.MirrorCS", {"start": v(143.78, 52.46) * mm, "mid": v(143.55, 52.16) * mm, "end": v(143.18, 52.04) * mm});
            skLineSegment(sketch, "E289.MirrorCS", {"start": v(145.56, 52.89) * mm, "end": v(145.71, 52.46) * mm});
            skLineSegment(sketch, "E290.MirrorCS", {"start": v(142.63, 51.35) * mm, "end": v(142.63, 51.63) * mm, "construction": true});
            skLineSegment(sketch, "E291.MirrorCS", {"start": v(33.9, 52.9) * mm, "end": v(34.05, 52.48) * mm});
            skArc(sketch, "E292.MirrorCS", {"start": v(128.7, 52.89) * mm, "mid": v(128.93, 53.2) * mm, "end": v(129.3, 53.3) * mm});
            skLineSegment(sketch, "E293.MirrorCS", {"start": v(39.73, 52.05) * mm, "end": v(40.6, 52.05) * mm});
            skLineSegment(sketch, "E294.MirrorCS", {"start": v(48.1, 53.32) * mm, "end": v(48.52, 53.32) * mm});
            skLineSegment(sketch, "E295.MirrorCS", {"start": v(142.32, 52.04) * mm, "end": v(143.18, 52.04) * mm});
            skLineSegment(sketch, "E296.MirrorCS", {"start": v(96.38, 51.8) * mm, "end": v(96.6, 51.8) * mm});
            skLineSegment(sketch, "E297.MirrorCS", {"start": v(162.64, 51.82) * mm, "end": v(162.64, 52.04) * mm});
            skLineSegment(sketch, "E298.MirrorCS", {"start": v(15.22, 52.06) * mm, "end": v(15.22, 51.84) * mm});
            skLineSegment(sketch, "E299.MirrorCS", {"start": v(167.5, 52.04) * mm, "end": v(167.5, 51.82) * mm});
            skLineSegment(sketch, "E300.MirrorCS", {"start": v(106.54, 51.8) * mm, "end": v(106.76, 51.8) * mm});
            skArc(sketch, "E301.MirrorCS", {"start": v(67.63, 52.46) * mm, "mid": v(67.4, 52.16) * mm, "end": v(67.03, 52.04) * mm});
            skLineSegment(sketch, "E302.MirrorCS", {"start": v(101.68, 51.8) * mm, "end": v(101.68, 52.02) * mm});
            skArc(sketch, "E303.MirrorCS", {"start": v(34.65, 52.05) * mm, "mid": v(34.28, 52.17) * mm, "end": v(34.05, 52.48) * mm});
            skLineSegment(sketch, "E304.MirrorCS", {"start": v(106.76, 52.02) * mm, "end": v(107.62, 52.02) * mm});
            skLineSegment(sketch, "E305.MirrorCS", {"start": v(137.13, 51.8) * mm, "end": v(137.13, 52.08) * mm, "construction": true});
            skLineSegment(sketch, "E306.MirrorCS", {"start": v(30.67, 52.06) * mm, "end": v(31.53, 52.06) * mm});
            skLineSegment(sketch, "E307.MirrorCS", {"start": v(139.46, 53.3) * mm, "end": v(139.88, 53.3) * mm});
            skLineSegment(sketch, "E308.MirrorCS", {"start": v(153.01, 51.34) * mm, "end": v(153.01, 51.63) * mm, "construction": true});
            skLineSegment(sketch, "E309.MirrorCS", {"start": v(90.45, 52.03) * mm, "end": v(91.31, 52.03) * mm});
            skArc(sketch, "E310.MirrorCS", {"start": v(113.3, 52.44) * mm, "mid": v(113.07, 52.13) * mm, "end": v(112.7, 52.01) * mm});
            skLineSegment(sketch, "E311.MirrorCS", {"start": v(134.38, 53.3) * mm, "end": v(134.8, 53.3) * mm});
            skArc(sketch, "E312.MirrorCS", {"start": v(109.4, 53.3) * mm, "mid": v(109.76, 53.18) * mm, "end": v(110, 52.87) * mm});
            skArc(sketch, "E313.MirrorCS", {"start": v(115.83, 52.01) * mm, "mid": v(115.47, 52.13) * mm, "end": v(115.23, 52.44) * mm});
            skArc(sketch, "E314.MirrorCS", {"start": v(67.78, 52.89) * mm, "mid": v(68.02, 53.2) * mm, "end": v(68.39, 53.3) * mm});
            skArc(sketch, "E315.MirrorCS", {"start": v(39.73, 52.05) * mm, "mid": v(39.36, 52.17) * mm, "end": v(39.13, 52.48) * mm});
            skArc(sketch, "E316.MirrorCS", {"start": v(43.44, 53.32) * mm, "mid": v(43.8, 53.2) * mm, "end": v(44.04, 52.9) * mm});
            skLineSegment(sketch, "E317.MirrorCS", {"start": v(66.17, 51.93) * mm, "end": v(65.94, 51.93) * mm, "construction": true});
            skArc(sketch, "E318.MirrorCS", {"start": v(159.02, 52.46) * mm, "mid": v(158.79, 52.16) * mm, "end": v(158.42, 52.04) * mm});
            skArc(sketch, "E319.MirrorCS", {"start": v(47.34, 52.47) * mm, "mid": v(47.1, 52.17) * mm, "end": v(46.74, 52.05) * mm});
            skArc(sketch, "E320.MirrorCS", {"start": v(128.54, 52.46) * mm, "mid": v(128.3, 52.16) * mm, "end": v(127.94, 52.04) * mm});
            skLineSegment(sketch, "E321.MirrorCS", {"start": v(157.34, 52.04) * mm, "end": v(157.34, 51.82) * mm});
            skLineSegment(sketch, "E322.MirrorCS", {"start": v(45.88, 52.05) * mm, "end": v(46.74, 52.05) * mm});
            skLineSegment(sketch, "E323.MirrorCS", {"start": v(167.72, 51.82) * mm, "end": v(167.72, 52.04) * mm});
            skArc(sketch, "E324.MirrorCS", {"start": v(154.1, 52.89) * mm, "mid": v(154.33, 53.2) * mm, "end": v(154.7, 53.3) * mm});
            skLineSegment(sketch, "E325.MirrorCS", {"start": v(127.08, 51.82) * mm, "end": v(127.08, 52.04) * mm});
            skArc(sketch, "E326.MirrorCS", {"start": v(48.52, 53.32) * mm, "mid": v(48.88, 53.2) * mm, "end": v(49.12, 52.9) * mm});
            skLineSegment(sketch, "E327.MirrorCS", {"start": v(152.26, 51.82) * mm, "end": v(152.48, 51.82) * mm});
            skArc(sketch, "E328.MirrorCS", {"start": v(164.26, 52.89) * mm, "mid": v(164.49, 53.2) * mm, "end": v(164.86, 53.3) * mm});
            skLineSegment(sketch, "E329.MirrorCS", {"start": v(155.72, 52.89) * mm, "end": v(155.87, 52.46) * mm});
            skArc(sketch, "E330.MirrorCS", {"start": v(133.62, 52.46) * mm, "mid": v(133.39, 52.16) * mm, "end": v(133.02, 52.04) * mm});
            skLineSegment(sketch, "E331.MirrorCS", {"start": v(104.92, 52.87) * mm, "end": v(105.07, 52.45) * mm});
            skLineSegment(sketch, "E332.MirrorCS", {"start": v(122, 51.8) * mm, "end": v(122, 52.04) * mm});
            skLineSegment(sketch, "E333.MirrorCS", {"start": v(108.22, 52.45) * mm, "end": v(108.38, 52.87) * mm});
            skLineSegment(sketch, "E334.MirrorCS", {"start": v(45.88, 51.94) * mm, "end": v(45.66, 51.94) * mm, "construction": true});
            skLineSegment(sketch, "E335.MirrorCS", {"start": v(35.73, 51.94) * mm, "end": v(35.51, 51.94) * mm, "construction": true});
            skArc(sketch, "E336.MirrorCS", {"start": v(136.15, 52.04) * mm, "mid": v(135.79, 52.16) * mm, "end": v(135.55, 52.46) * mm});
            skLineSegment(sketch, "E337.MirrorCS", {"start": v(34.65, 52.05) * mm, "end": v(35.51, 52.05) * mm});
            skArc(sketch, "E338.MirrorCS", {"start": v(151.4, 52.04) * mm, "mid": v(151.03, 52.16) * mm, "end": v(150.8, 52.46) * mm});
            skLineSegment(sketch, "E339.MirrorCS", {"start": v(66.17, 52.04) * mm, "end": v(67.03, 52.04) * mm});
            skLineSegment(sketch, "E340.MirrorCS", {"start": v(146.31, 52.04) * mm, "end": v(147.18, 52.04) * mm});
            skLineSegment(sketch, "E341.MirrorCS", {"start": v(160.8, 52.89) * mm, "end": v(160.95, 52.46) * mm});
            skArc(sketch, "E342.MirrorCS", {"start": v(120.91, 52.01) * mm, "mid": v(120.55, 52.13) * mm, "end": v(120.31, 52.44) * mm});
            skLineSegment(sketch, "E343.MirrorCS", {"start": v(91.53, 52.03) * mm, "end": v(92.4, 52.03) * mm});
            skLineSegment(sketch, "E344.MirrorCS", {"start": v(65.08, 52.04) * mm, "end": v(65.94, 52.04) * mm});
            skArc(sketch, "E345.MirrorCS", {"start": v(62.7, 52.89) * mm, "mid": v(62.94, 53.2) * mm, "end": v(63.3, 53.3) * mm});
            skArc(sketch, "E346.MirrorCS", {"start": v(119.56, 53.28) * mm, "mid": v(119.92, 53.17) * mm, "end": v(120.16, 52.86) * mm});
            skArc(sketch, "E347.MirrorCS", {"start": v(37.2, 52.48) * mm, "mid": v(36.96, 52.17) * mm, "end": v(36.6, 52.05) * mm});
            skLineSegment(sketch, "E348.MirrorCS", {"start": v(93.74, 53.3) * mm, "end": v(94.16, 53.3) * mm});
            skLineSegment(sketch, "E349.MirrorCS", {"start": v(37.95, 53.32) * mm, "end": v(38.37, 53.32) * mm});
            skLineSegment(sketch, "E350.MirrorCS", {"start": v(123.46, 52.46) * mm, "end": v(123.62, 52.89) * mm});
            skArc(sketch, "E351.MirrorCS", {"start": v(126, 52.04) * mm, "mid": v(125.63, 52.16) * mm, "end": v(125.4, 52.46) * mm});
            skLineSegment(sketch, "E352.MirrorCS", {"start": v(131.07, 52.04) * mm, "end": v(131.94, 52.04) * mm});
            skLineSegment(sketch, "E353.MirrorCS", {"start": v(153.12, 51.45) * mm, "end": v(152.9, 51.45) * mm, "construction": true});
            skArc(sketch, "E354.MirrorCS", {"start": v(123.62, 52.89) * mm, "mid": v(123.85, 53.2) * mm, "end": v(124.22, 53.3) * mm});
            skLineSegment(sketch, "E355.MirrorCS", {"start": v(118.38, 52.44) * mm, "end": v(118.54, 52.86) * mm});
            skLineSegment(sketch, "E356.MirrorCS", {"start": v(154.7, 53.3) * mm, "end": v(155.12, 53.3) * mm});
            skLineSegment(sketch, "E357.MirrorCS", {"start": v(98.82, 53.3) * mm, "end": v(99.24, 53.3) * mm});
            skArc(sketch, "E358.MirrorCS", {"start": v(42.26, 52.47) * mm, "mid": v(42.03, 52.17) * mm, "end": v(41.66, 52.05) * mm});
            skLineSegment(sketch, "E359.MirrorCS", {"start": v(167.72, 52.04) * mm, "end": v(168.58, 52.04) * mm});
            skArc(sketch, "E360.MirrorCS", {"start": v(100.6, 52.02) * mm, "mid": v(100.23, 52.14) * mm, "end": v(100, 52.45) * mm});
            skLineSegment(sketch, "E361.MirrorCS", {"start": v(150.64, 52.89) * mm, "end": v(150.8, 52.46) * mm});
            skArc(sketch, "E362.MirrorCS", {"start": v(124.64, 53.3) * mm, "mid": v(125, 53.2) * mm, "end": v(125.24, 52.89) * mm});
            skArc(sketch, "E363.MirrorCS", {"start": v(134.8, 53.3) * mm, "mid": v(135.16, 53.2) * mm, "end": v(135.4, 52.89) * mm});
            skLineSegment(sketch, "E364.MirrorCS", {"start": v(96.49, 51.8) * mm, "end": v(96.49, 52.1) * mm, "construction": true});
            skArc(sketch, "E365.MirrorCS", {"start": v(156.47, 52.04) * mm, "mid": v(156.1, 52.16) * mm, "end": v(155.87, 52.46) * mm});
            skLineSegment(sketch, "E366.MirrorCS", {"start": v(147.4, 52.04) * mm, "end": v(148.26, 52.04) * mm});
            skLineSegment(sketch, "E367.MirrorCS", {"start": v(128.54, 52.46) * mm, "end": v(128.7, 52.89) * mm});
            skLineSegment(sketch, "E368.MirrorCS", {"start": v(126.97, 51.82) * mm, "end": v(126.97, 52.1) * mm, "construction": true});
            skLineSegment(sketch, "E369.MirrorCS", {"start": v(159.78, 53.3) * mm, "end": v(160.2, 53.3) * mm});
            skArc(sketch, "E370.MirrorCS", {"start": v(166.63, 52.04) * mm, "mid": v(166.27, 52.16) * mm, "end": v(166.03, 52.46) * mm});
            skLineSegment(sketch, "E371.MirrorCS", {"start": v(162.92, 52) * mm, "end": v(162.7, 52) * mm, "construction": true});
            skLineSegment(sketch, "E372.MirrorCS", {"start": v(164.86, 53.3) * mm, "end": v(165.28, 53.3) * mm});
            skArc(sketch, "E373.MirrorCS", {"start": v(129.72, 53.3) * mm, "mid": v(130.08, 53.2) * mm, "end": v(130.32, 52.89) * mm});
            skLineSegment(sketch, "E374.MirrorCS", {"start": v(162.64, 52.04) * mm, "end": v(163.5, 52.04) * mm});
            skArc(sketch, "E375.MirrorCS", {"start": v(98.06, 52.45) * mm, "mid": v(97.83, 52.14) * mm, "end": v(97.46, 52.02) * mm});
            skLineSegment(sketch, "E376.MirrorCS", {"start": v(92.98, 52.45) * mm, "end": v(93.14, 52.87) * mm});
            skLineSegment(sketch, "E377.MirrorCS", {"start": v(198.2, 51.82) * mm, "end": v(198.2, 52.04) * mm});
            skArc(sketch, "E378.MirrorCS", {"start": v(103.3, 52.87) * mm, "mid": v(103.53, 53.18) * mm, "end": v(103.9, 53.3) * mm});
            skLineSegment(sketch, "E379.MirrorCS", {"start": v(131.94, 51.82) * mm, "end": v(132.16, 51.82) * mm});
            skLineSegment(sketch, "E380.MirrorCS", {"start": v(156.47, 52.04) * mm, "end": v(157.34, 52.04) * mm});
            skLineSegment(sketch, "E381.MirrorCS", {"start": v(120.91, 52.01) * mm, "end": v(121.78, 52.01) * mm});
            skLineSegment(sketch, "E382.MirrorCS", {"start": v(120.16, 52.86) * mm, "end": v(120.31, 52.44) * mm});
            skLineSegment(sketch, "E383.MirrorCS", {"start": v(101.46, 51.8) * mm, "end": v(101.68, 51.8) * mm});
            skLineSegment(sketch, "E384.MirrorCS", {"start": v(157.56, 52.04) * mm, "end": v(158.42, 52.04) * mm});
            skArc(sketch, "E385.MirrorCS", {"start": v(149.02, 52.89) * mm, "mid": v(149.25, 53.2) * mm, "end": v(149.62, 53.3) * mm});
            skLineSegment(sketch, "E386.MirrorCS", {"start": v(15.45, 51.84) * mm, "end": v(15.45, 52.06) * mm});
            skArc(sketch, "E387.MirrorCS", {"start": v(94.16, 53.3) * mm, "mid": v(94.52, 53.18) * mm, "end": v(94.76, 52.87) * mm});
            skLineSegment(sketch, "E388.MirrorCS", {"start": v(132.16, 52.04) * mm, "end": v(133.02, 52.04) * mm});
            skLineSegment(sketch, "E389.MirrorCS", {"start": v(116.92, 52.01) * mm, "end": v(117.78, 52.01) * mm});
            skLineSegment(sketch, "E390.MirrorCS", {"start": v(17.67, 53.33) * mm, "end": v(18.08, 53.33) * mm});
            skLineSegment(sketch, "E391.MirrorCS", {"start": v(44.04, 52.9) * mm, "end": v(44.2, 52.47) * mm});
            skLineSegment(sketch, "E392.MirrorCS", {"start": v(133.62, 52.46) * mm, "end": v(133.78, 52.89) * mm});
            skLineSegment(sketch, "E393.MirrorCS", {"start": v(115.08, 52.86) * mm, "end": v(115.23, 52.44) * mm});
            skLineSegment(sketch, "E394.MirrorCS", {"start": v(135.4, 52.89) * mm, "end": v(135.55, 52.46) * mm});
            skLineSegment(sketch, "E395.MirrorCS", {"start": v(151.4, 52.04) * mm, "end": v(152.26, 52.04) * mm});
            skLineSegment(sketch, "E396.MirrorCS", {"start": v(95.51, 52.02) * mm, "end": v(96.38, 52.02) * mm});
            skLineSegment(sketch, "E397.MirrorCS", {"start": v(161.55, 52.04) * mm, "end": v(162.42, 52.04) * mm});
            skLineSegment(sketch, "E398.MirrorCS", {"start": v(166.63, 52.04) * mm, "end": v(167.5, 52.04) * mm});
            skLineSegment(sketch, "E399.MirrorCS", {"start": v(20.3, 52.06) * mm, "end": v(20.3, 51.84) * mm});
            skLineSegment(sketch, "E400.MirrorCS", {"start": v(116.92, 51.9) * mm, "end": v(116.7, 51.9) * mm, "construction": true});
            skLineSegment(sketch, "E401.MirrorCS", {"start": v(147.18, 51.82) * mm, "end": v(147.4, 51.82) * mm});
            skLineSegment(sketch, "E402.MirrorCS", {"start": v(153.94, 52.46) * mm, "end": v(154.1, 52.89) * mm});
            skLineSegment(sketch, "E403.MirrorCS", {"start": v(125.24, 52.89) * mm, "end": v(125.4, 52.46) * mm});
            skArc(sketch, "E404.MirrorCS", {"start": v(92.98, 52.45) * mm, "mid": v(92.75, 52.14) * mm, "end": v(92.38, 52.02) * mm});
            skLineSegment(sketch, "E405.MirrorCS", {"start": v(169.18, 52.46) * mm, "end": v(169.34, 52.89) * mm});
            skLineSegment(sketch, "E406.MirrorCS", {"start": v(96.6, 51.91) * mm, "end": v(96.38, 51.91) * mm, "construction": true});
            skLineSegment(sketch, "E407.MirrorCS", {"start": v(42.26, 52.47) * mm, "end": v(42.42, 52.9) * mm});
            skArc(sketch, "E408.MirrorCS", {"start": v(169.34, 52.89) * mm, "mid": v(169.57, 53.2) * mm, "end": v(169.94, 53.3) * mm});
            skArc(sketch, "E409.MirrorCS", {"start": v(170.36, 53.3) * mm, "mid": v(170.72, 53.2) * mm, "end": v(170.96, 52.89) * mm});
            skArc(sketch, "E410.MirrorCS", {"start": v(98.22, 52.87) * mm, "mid": v(98.45, 53.18) * mm, "end": v(98.82, 53.3) * mm});
            skLineSegment(sketch, "E411.MirrorCS", {"start": v(40.81, 52.05) * mm, "end": v(41.67, 52.05) * mm});
            skArc(sketch, "E412.MirrorCS", {"start": v(159.18, 52.89) * mm, "mid": v(159.4, 53.2) * mm, "end": v(159.78, 53.3) * mm});
            skLineSegment(sketch, "E413.MirrorCS", {"start": v(172.58, 51.82) * mm, "end": v(172.8, 51.82) * mm});
            skLineSegment(sketch, "E414.MirrorCS", {"start": v(127.08, 52.04) * mm, "end": v(127.94, 52.04) * mm});
            skLineSegment(sketch, "E415.MirrorCS", {"start": v(96.6, 52.02) * mm, "end": v(97.46, 52.02) * mm});
            skLineSegment(sketch, "E416.MirrorCS", {"start": v(94.76, 52.87) * mm, "end": v(94.91, 52.45) * mm});
            skLineSegment(sketch, "E417.MirrorCS", {"start": v(126, 52.04) * mm, "end": v(126.86, 52.04) * mm});
            skLineSegment(sketch, "E418.MirrorCS", {"start": v(197.98, 51.82) * mm, "end": v(198.2, 51.82) * mm});
            skArc(sketch, "E419.MirrorCS", {"start": v(161.55, 52.04) * mm, "mid": v(161.19, 52.16) * mm, "end": v(160.95, 52.46) * mm});
            skArc(sketch, "E420.MirrorCS", {"start": v(123.46, 52.46) * mm, "mid": v(123.23, 52.16) * mm, "end": v(122.86, 52.04) * mm});
            skLineSegment(sketch, "E421.MirrorCS", {"start": v(101.95, 51.36) * mm, "end": v(101.95, 51.65) * mm, "construction": true});
            skLineSegment(sketch, "E422.MirrorCS", {"start": v(159.02, 52.46) * mm, "end": v(159.18, 52.89) * mm});
            skLineSegment(sketch, "E423.MirrorCS", {"start": v(103.9, 53.3) * mm, "end": v(104.32, 53.3) * mm});
            skLineSegment(sketch, "E424.MirrorCS", {"start": v(164.1, 52.46) * mm, "end": v(164.26, 52.89) * mm});
            skLineSegment(sketch, "E425.MirrorCS", {"start": v(15.22, 51.84) * mm, "end": v(15.45, 51.84) * mm});
            skLineSegment(sketch, "E426.MirrorCS", {"start": v(167.5, 51.82) * mm, "end": v(167.72, 51.82) * mm});
            skLineSegment(sketch, "E427.MirrorCS", {"start": v(99.84, 52.87) * mm, "end": v(100, 52.45) * mm});
            skLineSegment(sketch, "E428.MirrorCS", {"start": v(127.08, 51.93) * mm, "end": v(126.86, 51.93) * mm, "construction": true});
            skLineSegment(sketch, "E429.MirrorCS", {"start": v(122, 52.04) * mm, "end": v(122.86, 52.04) * mm});
            skArc(sketch, "E430.MirrorCS", {"start": v(165.28, 53.3) * mm, "mid": v(165.64, 53.2) * mm, "end": v(165.88, 52.89) * mm});
            skLineSegment(sketch, "E431.MirrorCS", {"start": v(20.53, 51.84) * mm, "end": v(20.53, 52.06) * mm});
            skLineSegment(sketch, "E432.MirrorCS", {"start": v(124.22, 53.3) * mm, "end": v(124.64, 53.3) * mm});
            skLineSegment(sketch, "E433.MirrorCS", {"start": v(162.42, 51.82) * mm, "end": v(162.64, 51.82) * mm});
            skArc(sketch, "E434.MirrorCS", {"start": v(164.1, 52.46) * mm, "mid": v(163.87, 52.16) * mm, "end": v(163.5, 52.04) * mm});
            skLineSegment(sketch, "E435.MirrorCS", {"start": v(18.69, 52.91) * mm, "end": v(18.84, 52.49) * mm});
            skLineSegment(sketch, "E436.MirrorCS", {"start": v(165.88, 52.89) * mm, "end": v(166.03, 52.46) * mm});
            skLineSegment(sketch, "E437.MirrorCS", {"start": v(121.78, 52.01) * mm, "end": v(121.78, 51.8) * mm});
            skLineSegment(sketch, "E438.MirrorCS", {"start": v(157.56, 51.82) * mm, "end": v(157.56, 52.04) * mm});
            skArc(sketch, "E439.MirrorCS", {"start": v(160.2, 53.3) * mm, "mid": v(160.56, 53.2) * mm, "end": v(160.8, 52.89) * mm});
            skLineSegment(sketch, "E440.MirrorCS", {"start": v(162.81, 51.9) * mm, "end": v(162.81, 52.19) * mm, "construction": true});
            skArc(sketch, "E441.MirrorCS", {"start": v(103.14, 52.45) * mm, "mid": v(102.9, 52.14) * mm, "end": v(102.54, 52.02) * mm});
            skArc(sketch, "E442.MirrorCS", {"start": v(95.51, 52.02) * mm, "mid": v(95.15, 52.14) * mm, "end": v(94.91, 52.45) * mm});
            skArc(sketch, "E443.MirrorCS", {"start": v(93.14, 52.87) * mm, "mid": v(93.37, 53.18) * mm, "end": v(93.74, 53.3) * mm});
            skLineSegment(sketch, "E444.MirrorCS", {"start": v(98.06, 52.45) * mm, "end": v(98.22, 52.87) * mm});
            skArc(sketch, "E445.MirrorCS", {"start": v(42.42, 52.9) * mm, "mid": v(42.65, 53.2) * mm, "end": v(43.02, 53.32) * mm});
            skArc(sketch, "E446.MirrorCS", {"start": v(197.11, 52.04) * mm, "mid": v(196.75, 52.16) * mm, "end": v(196.51, 52.46) * mm});
            skLineSegment(sketch, "E447.MirrorCS", {"start": v(269.1, 52.04) * mm, "end": v(269.1, 51.82) * mm});
            skLineSegment(sketch, "E448.MirrorCS", {"start": v(101.68, 52.02) * mm, "end": v(102.54, 52.02) * mm});
            skLineSegment(sketch, "E449.MirrorCS", {"start": v(15.34, 51.84) * mm, "end": v(15.34, 52.13) * mm, "construction": true});
            skLineSegment(sketch, "E450.MirrorCS", {"start": v(196.36, 52.89) * mm, "end": v(196.51, 52.46) * mm});
            skArc(sketch, "E451.MirrorCS", {"start": v(253, 52.04) * mm, "mid": v(252.63, 52.16) * mm, "end": v(252.4, 52.46) * mm});
            skLineSegment(sketch, "E452.MirrorCS", {"start": v(102.06, 51.47) * mm, "end": v(101.84, 51.47) * mm, "construction": true});
            skLineSegment(sketch, "E453.MirrorCS", {"start": v(192.9, 52.04) * mm, "end": v(192.9, 51.82) * mm});
            skLineSegment(sketch, "E454.MirrorCS", {"start": v(20.3, 51.84) * mm, "end": v(20.53, 51.84) * mm});
            skLineSegment(sketch, "E455.MirrorCS", {"start": v(187.82, 52.04) * mm, "end": v(187.82, 51.82) * mm});
            skArc(sketch, "E456.MirrorCS", {"start": v(19.44, 52.06) * mm, "mid": v(19.08, 52.18) * mm, "end": v(18.84, 52.49) * mm});
            skLineSegment(sketch, "E457.MirrorCS", {"start": v(16.9, 52.49) * mm, "end": v(17.06, 52.91) * mm});
            skLineSegment(sketch, "E458.MirrorCS", {"start": v(43.02, 53.32) * mm, "end": v(43.44, 53.32) * mm});
            skArc(sketch, "E459.MirrorCS", {"start": v(104.32, 53.3) * mm, "mid": v(104.68, 53.18) * mm, "end": v(104.92, 52.87) * mm});
            skArc(sketch, "E460.MirrorCS", {"start": v(99.24, 53.3) * mm, "mid": v(99.6, 53.18) * mm, "end": v(99.84, 52.87) * mm});
            skLineSegment(sketch, "E461.MirrorCS", {"start": v(100.6, 52.02) * mm, "end": v(101.46, 52.02) * mm});
            skLineSegment(sketch, "E462.MirrorCS", {"start": v(19.44, 52.06) * mm, "end": v(20.3, 52.06) * mm});
            skArc(sketch, "E463.MirrorCS", {"start": v(171.71, 52.04) * mm, "mid": v(171.35, 52.16) * mm, "end": v(171.11, 52.46) * mm});
            skLineSegment(sketch, "E464.MirrorCS", {"start": v(248.78, 52.04) * mm, "end": v(248.78, 51.82) * mm});
            skLineSegment(sketch, "E465.MirrorCS", {"start": v(12.59, 53.33) * mm, "end": v(13, 53.33) * mm});
            skArc(sketch, "E466.MirrorCS", {"start": v(18.08, 53.33) * mm, "mid": v(18.45, 53.22) * mm, "end": v(18.69, 52.91) * mm});
            skArc(sketch, "E467.MirrorCS", {"start": v(189.5, 52.46) * mm, "mid": v(189.27, 52.16) * mm, "end": v(188.9, 52.04) * mm});
            skArc(sketch, "E468.MirrorCS", {"start": v(44.8, 52.05) * mm, "mid": v(44.43, 52.17) * mm, "end": v(44.2, 52.47) * mm});
            skArc(sketch, "E469.MirrorCS", {"start": v(16.9, 52.49) * mm, "mid": v(16.67, 52.18) * mm, "end": v(16.3, 52.06) * mm});
            skLineSegment(sketch, "E470.MirrorCS", {"start": v(169.94, 53.3) * mm, "end": v(170.36, 53.3) * mm});
            skLineSegment(sketch, "E471.MirrorCS", {"start": v(103.14, 52.45) * mm, "end": v(103.3, 52.87) * mm});
            skLineSegment(sketch, "E472.MirrorCS", {"start": v(157.34, 51.82) * mm, "end": v(157.56, 51.82) * mm});
            skLineSegment(sketch, "E473.MirrorCS", {"start": v(170.96, 52.89) * mm, "end": v(171.11, 52.46) * mm});
            skArc(sketch, "E474.MirrorCS", {"start": v(169.18, 52.46) * mm, "mid": v(168.95, 52.16) * mm, "end": v(168.58, 52.04) * mm});
            skLineSegment(sketch, "E475.MirrorCS", {"start": v(194.58, 52.46) * mm, "end": v(194.74, 52.89) * mm});
            skLineSegment(sketch, "E476.MirrorCS", {"start": v(203.06, 51.82) * mm, "end": v(203.28, 51.82) * mm});
            skLineSegment(sketch, "E477.MirrorCS", {"start": v(195.22, 52.22) * mm, "end": v(195.22, 52.5) * mm, "construction": true});
            skLineSegment(sketch, "E478.MirrorCS", {"start": v(274.18, 52.04) * mm, "end": v(274.18, 51.82) * mm});
            skLineSegment(sketch, "E479.MirrorCS", {"start": v(188.04, 51.82) * mm, "end": v(188.04, 52.04) * mm});
            skLineSegment(sketch, "E480.MirrorCS", {"start": v(14.36, 52.06) * mm, "end": v(15.22, 52.06) * mm});
            skLineSegment(sketch, "E481.MirrorCS", {"start": v(193.12, 51.82) * mm, "end": v(193.12, 52.04) * mm});
            skLineSegment(sketch, "E482.MirrorCS", {"start": v(11.83, 52.49) * mm, "end": v(11.98, 52.91) * mm});
            skLineSegment(sketch, "E483.MirrorCS", {"start": v(172.58, 52.04) * mm, "end": v(172.58, 51.82) * mm});
            skLineSegment(sketch, "E484.MirrorCS", {"start": v(243.92, 51.82) * mm, "end": v(243.92, 52.04) * mm});
            skLineSegment(sketch, "E485.MirrorCS", {"start": v(171.71, 52.04) * mm, "end": v(172.58, 52.04) * mm});
            skLineSegment(sketch, "E486.MirrorCS", {"start": v(10.38, 52.07) * mm, "end": v(11.24, 52.07) * mm});
            skArc(sketch, "E487.MirrorCS", {"start": v(17.06, 52.91) * mm, "mid": v(17.3, 53.22) * mm, "end": v(17.67, 53.33) * mm});
            skArc(sketch, "E488.MirrorCS", {"start": v(245.54, 52.89) * mm, "mid": v(245.77, 53.2) * mm, "end": v(246.14, 53.3) * mm});
            skArc(sketch, "E489.MirrorCS", {"start": v(194.58, 52.46) * mm, "mid": v(194.35, 52.16) * mm, "end": v(193.98, 52.04) * mm});
            skArc(sketch, "E490.MirrorCS", {"start": v(13, 53.33) * mm, "mid": v(13.37, 53.22) * mm, "end": v(13.6, 52.91) * mm});
            skLineSegment(sketch, "E491.MirrorCS", {"start": v(203.28, 51.82) * mm, "end": v(203.28, 52.04) * mm});
            skLineSegment(sketch, "E492.MirrorCS", {"start": v(15.45, 51.95) * mm, "end": v(15.22, 51.95) * mm, "construction": true});
            skLineSegment(sketch, "E493.MirrorCS", {"start": v(249, 51.82) * mm, "end": v(249, 52.04) * mm});
            skArc(sketch, "E494.MirrorCS", {"start": v(202.2, 52.04) * mm, "mid": v(201.83, 52.16) * mm, "end": v(201.6, 52.46) * mm});
            skLineSegment(sketch, "E495.MirrorCS", {"start": v(269.32, 51.82) * mm, "end": v(269.32, 52.04) * mm});
            skArc(sketch, "E496.MirrorCS", {"start": v(200.84, 53.3) * mm, "mid": v(201.2, 53.2) * mm, "end": v(201.44, 52.89) * mm});
            skLineSegment(sketch, "E497.MirrorCS", {"start": v(191.28, 52.89) * mm, "end": v(191.43, 52.46) * mm});
            skLineSegment(sketch, "E498.MirrorCS", {"start": v(279.76, 51.78) * mm, "end": v(279.76, 52) * mm});
            skLineSegment(sketch, "E499.MirrorCS", {"start": v(15.45, 52.06) * mm, "end": v(16.3, 52.06) * mm});
            skLineSegment(sketch, "E500.MirrorCS", {"start": v(177.66, 51.82) * mm, "end": v(177.88, 51.82) * mm});
            skLineSegment(sketch, "E501.MirrorCS", {"start": v(195.34, 53.3) * mm, "end": v(195.76, 53.3) * mm});
            skLineSegment(sketch, "E502.MirrorCS", {"start": v(252.24, 52.89) * mm, "end": v(252.4, 52.46) * mm});
            skLineSegment(sketch, "E503.MirrorCS", {"start": v(7.52, 53.34) * mm, "end": v(7.94, 53.34) * mm});
            skLineSegment(sketch, "E504.MirrorCS", {"start": v(10.38, 51.85) * mm, "end": v(10.38, 52.07) * mm});
            skArc(sketch, "E505.MirrorCS", {"start": v(247.91, 52.04) * mm, "mid": v(247.55, 52.16) * mm, "end": v(247.31, 52.46) * mm});
            skLineSegment(sketch, "E506.MirrorCS", {"start": v(197.98, 52.04) * mm, "end": v(197.98, 51.82) * mm});
            skLineSegment(sketch, "E507.MirrorCS", {"start": v(188.04, 52.04) * mm, "end": v(188.9, 52.04) * mm});
            skLineSegment(sketch, "E508.MirrorCS", {"start": v(250.46, 52.46) * mm, "end": v(250.62, 52.89) * mm});
            skLineSegment(sketch, "E509.MirrorCS", {"start": v(269.1, 51.82) * mm, "end": v(269.32, 51.82) * mm});
            skArc(sketch, "E510.MirrorCS", {"start": v(194.74, 52.89) * mm, "mid": v(194.97, 53.2) * mm, "end": v(195.34, 53.3) * mm});
            skLineSegment(sketch, "E511.MirrorCS", {"start": v(201.44, 52.89) * mm, "end": v(201.6, 52.46) * mm});
            skLineSegment(sketch, "E512.MirrorCS", {"start": v(279.54, 51.78) * mm, "end": v(279.76, 51.78) * mm});
            skLineSegment(sketch, "E513.MirrorCS", {"start": v(272.56, 52.89) * mm, "end": v(272.71, 52.46) * mm});
            skArc(sketch, "E514.MirrorCS", {"start": v(199.66, 52.46) * mm, "mid": v(199.43, 52.16) * mm, "end": v(199.06, 52.04) * mm});
            skLineSegment(sketch, "E515.MirrorCS", {"start": v(13.6, 52.91) * mm, "end": v(13.76, 52.49) * mm});
            skArc(sketch, "E516.MirrorCS", {"start": v(11.83, 52.49) * mm, "mid": v(11.6, 52.18) * mm, "end": v(11.23, 52.06) * mm});
            skLineSegment(sketch, "E517.MirrorCS", {"start": v(274.68, 51.82) * mm, "end": v(274.68, 52) * mm});
            skLineSegment(sketch, "E518.MirrorCS", {"start": v(264.02, 52.04) * mm, "end": v(264.02, 51.82) * mm});
            skLineSegment(sketch, "E519.MirrorCS", {"start": v(218.3, 52.04) * mm, "end": v(218.3, 51.82) * mm});
            skArc(sketch, "E520.MirrorCS", {"start": v(7.94, 53.34) * mm, "mid": v(8.3, 53.22) * mm, "end": v(8.54, 52.92) * mm});
            skArc(sketch, "E521.MirrorCS", {"start": v(270.78, 52.46) * mm, "mid": v(270.55, 52.16) * mm, "end": v(270.18, 52.04) * mm});
            skLineSegment(sketch, "E522.MirrorCS", {"start": v(208.14, 52.04) * mm, "end": v(208.14, 51.82) * mm});
            skArc(sketch, "E523.MirrorCS", {"start": v(192.03, 52.04) * mm, "mid": v(191.67, 52.16) * mm, "end": v(191.43, 52.46) * mm});
            skLineSegment(sketch, "E524.MirrorCS", {"start": v(198.2, 52.04) * mm, "end": v(199.06, 52.04) * mm});
            skLineSegment(sketch, "E525.MirrorCS", {"start": v(202.2, 52.04) * mm, "end": v(203.06, 52.04) * mm});
            skLineSegment(sketch, "E526.MirrorCS", {"start": v(246.14, 53.3) * mm, "end": v(246.56, 53.3) * mm});
            skLineSegment(sketch, "E527.MirrorCS", {"start": v(203.06, 52.04) * mm, "end": v(203.06, 51.82) * mm});
            skArc(sketch, "E528.MirrorCS", {"start": v(250.62, 52.89) * mm, "mid": v(250.85, 53.2) * mm, "end": v(251.22, 53.3) * mm});
            skLineSegment(sketch, "E529.MirrorCS", {"start": v(175.02, 53.3) * mm, "end": v(175.44, 53.3) * mm});
            skLineSegment(sketch, "E530.MirrorCS", {"start": v(199.66, 52.46) * mm, "end": v(199.82, 52.89) * mm});
            skLineSegment(sketch, "E531.MirrorCS", {"start": v(247.91, 52.04) * mm, "end": v(248.78, 52.04) * mm});
            skLineSegment(sketch, "E532.MirrorCS", {"start": v(253.86, 52.04) * mm, "end": v(253.86, 51.82) * mm});
            skLineSegment(sketch, "E533.MirrorCS", {"start": v(10.16, 52.07) * mm, "end": v(10.16, 51.85) * mm});
            skLineSegment(sketch, "E534.MirrorCS", {"start": v(195.33, 52.33) * mm, "end": v(195.1, 52.33) * mm, "construction": true});
            skLineSegment(sketch, "E535.MirrorCS", {"start": v(190.26, 53.3) * mm, "end": v(190.68, 53.3) * mm});
            skLineSegment(sketch, "E536.MirrorCS", {"start": v(177.88, 51.82) * mm, "end": v(177.88, 52.04) * mm});
            skArc(sketch, "E537.MirrorCS", {"start": v(199.82, 52.89) * mm, "mid": v(200.05, 53.2) * mm, "end": v(200.42, 53.3) * mm});
            skLineSegment(sketch, "E538.MirrorCS", {"start": v(247.16, 52.89) * mm, "end": v(247.31, 52.46) * mm});
            skLineSegment(sketch, "E539.MirrorCS", {"start": v(187.82, 51.82) * mm, "end": v(188.04, 51.82) * mm});
            skLineSegment(sketch, "E540.MirrorCS", {"start": v(192.9, 51.82) * mm, "end": v(193.12, 51.82) * mm});
            skLineSegment(sketch, "E541.MirrorCS", {"start": v(200.42, 53.3) * mm, "end": v(200.84, 53.3) * mm});
            skLineSegment(sketch, "E542.MirrorCS", {"start": v(185.18, 53.3) * mm, "end": v(185.6, 53.3) * mm});
            skLineSegment(sketch, "E543.MirrorCS", {"start": v(248.78, 51.82) * mm, "end": v(249, 51.82) * mm});
            skLineSegment(sketch, "E544.MirrorCS", {"start": v(9.3, 52.07) * mm, "end": v(10.16, 52.07) * mm});
            skLineSegment(sketch, "E545.MirrorCS", {"start": v(223.38, 52.04) * mm, "end": v(223.38, 51.82) * mm});
            skLineSegment(sketch, "E546.MirrorCS", {"start": v(188.55, 53.85) * mm, "end": v(188.55, 54.14) * mm, "construction": true});
            skLineSegment(sketch, "E547.MirrorCS", {"start": v(172.8, 51.82) * mm, "end": v(172.8, 52.04) * mm});
            skLineSegment(sketch, "E548.MirrorCS", {"start": v(197.11, 52.04) * mm, "end": v(197.98, 52.04) * mm});
            skArc(sketch, "E549.MirrorCS", {"start": v(184.42, 52.46) * mm, "mid": v(184.19, 52.16) * mm, "end": v(183.82, 52.04) * mm});
            skArc(sketch, "E550.MirrorCS", {"start": v(195.76, 53.3) * mm, "mid": v(196.12, 53.2) * mm, "end": v(196.36, 52.89) * mm});
            skLineSegment(sketch, "E551.MirrorCS", {"start": v(189.5, 52.46) * mm, "end": v(189.66, 52.89) * mm});
            skLineSegment(sketch, "E552.MirrorCS", {"start": v(245.38, 52.46) * mm, "end": v(245.54, 52.89) * mm});
            skLineSegment(sketch, "E553.MirrorCS", {"start": v(178.47, 55.4) * mm, "end": v(178.47, 55.7) * mm, "construction": true});
            skLineSegment(sketch, "E554.MirrorCS", {"start": v(253, 52.04) * mm, "end": v(253.86, 52.04) * mm});
            skLineSegment(sketch, "E555.MirrorCS", {"start": v(269.63, 51.63) * mm, "end": v(269.63, 51.92) * mm, "construction": true});
            skLineSegment(sketch, "E556.MirrorCS", {"start": v(177.66, 52.04) * mm, "end": v(177.66, 51.82) * mm});
            skArc(sketch, "E557.MirrorCS", {"start": v(251.64, 53.3) * mm, "mid": v(252, 53.2) * mm, "end": v(252.24, 52.89) * mm});
            skLineSegment(sketch, "E558.MirrorCS", {"start": v(279.54, 52) * mm, "end": v(279.54, 51.78) * mm});
            skArc(sketch, "E559.MirrorCS", {"start": v(245.38, 52.46) * mm, "mid": v(245.15, 52.16) * mm, "end": v(244.78, 52.04) * mm});
            skLineSegment(sketch, "E560.MirrorCS", {"start": v(8.54, 52.92) * mm, "end": v(8.7, 52.5) * mm});
            skLineSegment(sketch, "E561.MirrorCS", {"start": v(182.96, 52.04) * mm, "end": v(183.82, 52.04) * mm});
            skArc(sketch, "E562.MirrorCS", {"start": v(175.44, 53.3) * mm, "mid": v(175.8, 53.2) * mm, "end": v(176.04, 52.89) * mm});
            skLineSegment(sketch, "E563.MirrorCS", {"start": v(204.74, 52.46) * mm, "end": v(204.9, 52.89) * mm});
            skLineSegment(sketch, "E564.MirrorCS", {"start": v(218.52, 52.04) * mm, "end": v(219.38, 52.04) * mm});
            skLineSegment(sketch, "E565.MirrorCS", {"start": v(193.12, 52.04) * mm, "end": v(193.98, 52.04) * mm});
            skLineSegment(sketch, "E566.MirrorCS", {"start": v(208.14, 51.82) * mm, "end": v(208.36, 51.82) * mm});
            skLineSegment(sketch, "E567.MirrorCS", {"start": v(10.16, 51.85) * mm, "end": v(10.38, 51.85) * mm});
            skLineSegment(sketch, "E568.MirrorCS", {"start": v(188.66, 53.96) * mm, "end": v(188.43, 53.96) * mm, "construction": true});
            skLineSegment(sketch, "E569.MirrorCS", {"start": v(192.03, 52.04) * mm, "end": v(192.9, 52.04) * mm});
            skArc(sketch, "E570.MirrorCS", {"start": v(11.98, 52.91) * mm, "mid": v(12.22, 53.22) * mm, "end": v(12.59, 53.33) * mm});
            skLineSegment(sketch, "E571.MirrorCS", {"start": v(11.24, 52.07) * mm, "end": v(11.24, 50.8) * mm, "construction": true});
            skLineSegment(sketch, "E572.MirrorCS", {"start": v(270.78, 52.46) * mm, "end": v(270.94, 52.89) * mm});
            skLineSegment(sketch, "E573.MirrorCS", {"start": v(264.24, 51.82) * mm, "end": v(264.24, 52.04) * mm});
            skLineSegment(sketch, "E574.MirrorCS", {"start": v(174.26, 52.46) * mm, "end": v(174.42, 52.89) * mm});
            skArc(sketch, "E575.MirrorCS", {"start": v(14.36, 52.06) * mm, "mid": v(14, 52.18) * mm, "end": v(13.76, 52.49) * mm});
            skLineSegment(sketch, "E576.MirrorCS", {"start": v(218.52, 51.82) * mm, "end": v(218.52, 52.04) * mm});
            skLineSegment(sketch, "E577.MirrorCS", {"start": v(249, 52.04) * mm, "end": v(249.86, 52.04) * mm});
            skArc(sketch, "E578.MirrorCS", {"start": v(209.82, 52.46) * mm, "mid": v(209.59, 52.16) * mm, "end": v(209.22, 52.04) * mm});
            skLineSegment(sketch, "E579.MirrorCS", {"start": v(243.92, 52.04) * mm, "end": v(244.78, 52.04) * mm});
            skLineSegment(sketch, "E580.MirrorCS", {"start": v(268.23, 52.04) * mm, "end": v(269.1, 52.04) * mm});
            skArc(sketch, "E581.MirrorCS", {"start": v(276.3, 52.85) * mm, "mid": v(276.53, 53.16) * mm, "end": v(276.9, 53.27) * mm});
            skArc(sketch, "E582.MirrorCS", {"start": v(190.68, 53.3) * mm, "mid": v(191.04, 53.2) * mm, "end": v(191.28, 52.89) * mm});
            skArc(sketch, "E583.MirrorCS", {"start": v(189.66, 52.89) * mm, "mid": v(189.89, 53.2) * mm, "end": v(190.26, 53.3) * mm});
            skArc(sketch, "E584.MirrorCS", {"start": v(9.3, 52.07) * mm, "mid": v(8.93, 52.19) * mm, "end": v(8.7, 52.5) * mm});
            skArc(sketch, "E585.MirrorCS", {"start": v(179.34, 52.46) * mm, "mid": v(179.1, 52.16) * mm, "end": v(178.74, 52.04) * mm});
            skLineSegment(sketch, "E586.MirrorCS", {"start": v(278.68, 52) * mm, "end": v(279.54, 52) * mm});
            skLineSegment(sketch, "E587.MirrorCS", {"start": v(273.31, 52.04) * mm, "end": v(274.18, 52.04) * mm});
            skLineSegment(sketch, "E588.MirrorCS", {"start": v(248.22, 51.93) * mm, "end": v(248, 51.93) * mm, "construction": true});
            skArc(sketch, "E589.MirrorCS", {"start": v(273.31, 52.04) * mm, "mid": v(272.95, 52.16) * mm, "end": v(272.71, 52.46) * mm});
            skLineSegment(sketch, "E590.MirrorCS", {"start": v(186.2, 52.89) * mm, "end": v(186.35, 52.46) * mm});
            skArc(sketch, "E591.MirrorCS", {"start": v(186.95, 52.04) * mm, "mid": v(186.59, 52.16) * mm, "end": v(186.35, 52.46) * mm});
            skArc(sketch, "E592.MirrorCS", {"start": v(185.6, 53.3) * mm, "mid": v(185.96, 53.2) * mm, "end": v(186.2, 52.89) * mm});
            skArc(sketch, "E593.MirrorCS", {"start": v(246.56, 53.3) * mm, "mid": v(246.92, 53.2) * mm, "end": v(247.16, 52.89) * mm});
            skLineSegment(sketch, "E594.MirrorCS", {"start": v(266.46, 53.3) * mm, "end": v(266.88, 53.3) * mm});
            skLineSegment(sketch, "E595.MirrorCS", {"start": v(251.22, 53.3) * mm, "end": v(251.64, 53.3) * mm});
            skLineSegment(sketch, "E596.MirrorCS", {"start": v(223.6, 51.82) * mm, "end": v(223.6, 52.04) * mm});
            skArc(sketch, "E597.MirrorCS", {"start": v(265.7, 52.46) * mm, "mid": v(265.47, 52.16) * mm, "end": v(265.1, 52.04) * mm});
            skArc(sketch, "E598.MirrorCS", {"start": v(214.9, 52.46) * mm, "mid": v(214.67, 52.16) * mm, "end": v(214.3, 52.04) * mm});
            skArc(sketch, "E599.MirrorCS", {"start": v(174.26, 52.46) * mm, "mid": v(174.03, 52.16) * mm, "end": v(173.66, 52.04) * mm});
            skLineSegment(sketch, "E600.MirrorCS", {"start": v(248.11, 51.82) * mm, "end": v(248.11, 52.1) * mm, "construction": true});
            skLineSegment(sketch, "E601.MirrorCS", {"start": v(186.95, 52.04) * mm, "end": v(187.82, 52.04) * mm});
            skArc(sketch, "E602.MirrorCS", {"start": v(250.46, 52.46) * mm, "mid": v(250.23, 52.16) * mm, "end": v(249.86, 52.04) * mm});
            skLineSegment(sketch, "E603.MirrorCS", {"start": v(271.54, 53.3) * mm, "end": v(271.96, 53.3) * mm});
            skArc(sketch, "E604.MirrorCS", {"start": v(278.68, 52) * mm, "mid": v(278.3, 52.12) * mm, "end": v(278.07, 52.43) * mm});
            skArc(sketch, "E605.MirrorCS", {"start": v(266.88, 53.3) * mm, "mid": v(267.24, 53.2) * mm, "end": v(267.48, 52.89) * mm});
            skLineSegment(sketch, "E606.MirrorCS", {"start": v(267.48, 52.89) * mm, "end": v(267.63, 52.46) * mm});
            skArc(sketch, "E607.MirrorCS", {"start": v(265.86, 52.89) * mm, "mid": v(266.09, 53.2) * mm, "end": v(266.46, 53.3) * mm});
            skLineSegment(sketch, "E608.MirrorCS", {"start": v(264.02, 51.82) * mm, "end": v(264.24, 51.82) * mm});
            skLineSegment(sketch, "E609.MirrorCS", {"start": v(238.62, 52.04) * mm, "end": v(238.62, 51.82) * mm});
            skLineSegment(sketch, "E610.MirrorCS", {"start": v(215.66, 53.3) * mm, "end": v(216.08, 53.3) * mm});
            skLineSegment(sketch, "E611.MirrorCS", {"start": v(269.74, 51.74) * mm, "end": v(269.52, 51.74) * mm, "construction": true});
            skArc(sketch, "E612.MirrorCS", {"start": v(212.35, 52.04) * mm, "mid": v(211.99, 52.16) * mm, "end": v(211.75, 52.46) * mm});
            skLineSegment(sketch, "E613.MirrorCS", {"start": v(276.9, 53.27) * mm, "end": v(277.32, 53.27) * mm});
            skLineSegment(sketch, "E614.MirrorCS", {"start": v(179.34, 52.46) * mm, "end": v(179.5, 52.89) * mm});
            skLineSegment(sketch, "E615.MirrorCS", {"start": v(269.32, 52.04) * mm, "end": v(270.18, 52.04) * mm});
            skLineSegment(sketch, "E616.MirrorCS", {"start": v(177.88, 52.04) * mm, "end": v(178.74, 52.04) * mm});
            skLineSegment(sketch, "E617.MirrorCS", {"start": v(208.36, 51.82) * mm, "end": v(208.36, 52.04) * mm});
            skArc(sketch, "E618.MirrorCS", {"start": v(268.23, 52.04) * mm, "mid": v(267.87, 52.16) * mm, "end": v(267.63, 52.46) * mm});
            skLineSegment(sketch, "E619.MirrorCS", {"start": v(218.3, 51.82) * mm, "end": v(218.52, 51.82) * mm});
            skArc(sketch, "E620.MirrorCS", {"start": v(184.58, 52.89) * mm, "mid": v(184.8, 53.2) * mm, "end": v(185.18, 53.3) * mm});
            skArc(sketch, "E621.MirrorCS", {"start": v(176.8, 52.04) * mm, "mid": v(176.43, 52.16) * mm, "end": v(176.2, 52.46) * mm});
            skLineSegment(sketch, "E622.MirrorCS", {"start": v(264.24, 52.04) * mm, "end": v(265.1, 52.04) * mm});
            skLineSegment(sketch, "E623.MirrorCS", {"start": v(279.65, 51.78) * mm, "end": v(279.65, 52.07) * mm, "construction": true});
            skArc(sketch, "E624.MirrorCS", {"start": v(282.4, 53.27) * mm, "mid": v(282.76, 53.16) * mm, "end": v(283, 52.85) * mm});
            skLineSegment(sketch, "E625.MirrorCS", {"start": v(208.36, 52.04) * mm, "end": v(209.22, 52.04) * mm});
            skLineSegment(sketch, "E626.MirrorCS", {"start": v(219.98, 52.46) * mm, "end": v(220.14, 52.89) * mm});
            skLineSegment(sketch, "E627.MirrorCS", {"start": v(172.8, 52.04) * mm, "end": v(173.66, 52.04) * mm});
            skArc(sketch, "E628.MirrorCS", {"start": v(240.3, 52.46) * mm, "mid": v(240.07, 52.16) * mm, "end": v(239.7, 52.04) * mm});
            skLineSegment(sketch, "E629.MirrorCS", {"start": v(206.52, 52.89) * mm, "end": v(206.67, 52.46) * mm});
            skLineSegment(sketch, "E630.MirrorCS", {"start": v(213.44, 52.04) * mm, "end": v(214.3, 52.04) * mm});
            skArc(sketch, "E631.MirrorCS", {"start": v(283.76, 52) * mm, "mid": v(283.39, 52.12) * mm, "end": v(283.15, 52.43) * mm});
            skLineSegment(sketch, "E632.MirrorCS", {"start": v(182.74, 52.04) * mm, "end": v(182.74, 51.82) * mm});
            skLineSegment(sketch, "E633.MirrorCS", {"start": v(210.58, 53.3) * mm, "end": v(211, 53.3) * mm});
            skLineSegment(sketch, "E634.MirrorCS", {"start": v(176.8, 52.04) * mm, "end": v(177.66, 52.04) * mm});
            skArc(sketch, "E635.MirrorCS", {"start": v(180.52, 53.3) * mm, "mid": v(180.88, 53.2) * mm, "end": v(181.12, 52.89) * mm});
            skLineSegment(sketch, "E636.MirrorCS", {"start": v(204.83, 53.13) * mm, "end": v(204.83, 53.41) * mm, "construction": true});
            skArc(sketch, "E637.MirrorCS", {"start": v(221.16, 53.3) * mm, "mid": v(221.52, 53.2) * mm, "end": v(221.76, 52.89) * mm});
            skLineSegment(sketch, "E638.MirrorCS", {"start": v(258.94, 51.82) * mm, "end": v(259.16, 51.82) * mm});
            skLineSegment(sketch, "E639.MirrorCS", {"start": v(203.28, 52.04) * mm, "end": v(204.14, 52.04) * mm});
            skLineSegment(sketch, "E640.MirrorCS", {"start": v(223.38, 51.82) * mm, "end": v(223.6, 51.82) * mm});
            skLineSegment(sketch, "E641.MirrorCS", {"start": v(213.22, 52.04) * mm, "end": v(213.22, 51.82) * mm});
            skLineSegment(sketch, "E642.MirrorCS", {"start": v(274.18, 51.82) * mm, "end": v(274.68, 51.82) * mm});
            skArc(sketch, "E643.MirrorCS", {"start": v(271.96, 53.3) * mm, "mid": v(272.32, 53.2) * mm, "end": v(272.56, 52.89) * mm});
            skArc(sketch, "E644.MirrorCS", {"start": v(281.22, 52.43) * mm, "mid": v(280.99, 52.12) * mm, "end": v(280.62, 52) * mm});
            skLineSegment(sketch, "E645.MirrorCS", {"start": v(265.7, 52.46) * mm, "end": v(265.86, 52.89) * mm});
            skArc(sketch, "E646.MirrorCS", {"start": v(270.94, 52.89) * mm, "mid": v(271.17, 53.2) * mm, "end": v(271.54, 53.3) * mm});
            skArc(sketch, "E647.MirrorCS", {"start": v(281.38, 52.85) * mm, "mid": v(281.61, 53.16) * mm, "end": v(281.98, 53.27) * mm});
            skLineSegment(sketch, "E648.MirrorCS", {"start": v(216.95, 51.3) * mm, "end": v(216.73, 51.3) * mm, "construction": true});
            skLineSegment(sketch, "E649.MirrorCS", {"start": v(178.58, 55.51) * mm, "end": v(178.36, 55.51) * mm, "construction": true});
            skLineSegment(sketch, "E650.MirrorCS", {"start": v(276.14, 52.43) * mm, "end": v(276.3, 52.85) * mm});
            skArc(sketch, "E651.MirrorCS", {"start": v(174.42, 52.89) * mm, "mid": v(174.65, 53.2) * mm, "end": v(175.02, 53.3) * mm});
            skLineSegment(sketch, "E652.MirrorCS", {"start": v(184.42, 52.46) * mm, "end": v(184.58, 52.89) * mm});
            skLineSegment(sketch, "E653.MirrorCS", {"start": v(176.04, 52.89) * mm, "end": v(176.2, 52.46) * mm});
            skLineSegment(sketch, "E654.MirrorCS", {"start": v(216.68, 52.89) * mm, "end": v(216.83, 52.46) * mm});
            skLineSegment(sketch, "E655.MirrorCS", {"start": v(209.82, 52.46) * mm, "end": v(209.98, 52.89) * mm});
            skLineSegment(sketch, "E656.MirrorCS", {"start": v(180.1, 53.3) * mm, "end": v(180.52, 53.3) * mm});
            skLineSegment(sketch, "E657.MirrorCS", {"start": v(228.46, 52.04) * mm, "end": v(228.46, 51.82) * mm});
            skArc(sketch, "E658.MirrorCS", {"start": v(181.87, 52.04) * mm, "mid": v(181.5, 52.16) * mm, "end": v(181.27, 52.46) * mm});
            skLineSegment(sketch, "E659.MirrorCS", {"start": v(279.76, 51.9) * mm, "end": v(279.54, 51.9) * mm, "construction": true});
            skLineSegment(sketch, "E660.MirrorCS", {"start": v(204.94, 53.24) * mm, "end": v(204.71, 53.24) * mm, "construction": true});
            skLineSegment(sketch, "E661.MirrorCS", {"start": v(213.44, 51.82) * mm, "end": v(213.44, 52.04) * mm});
            skArc(sketch, "E662.MirrorCS", {"start": v(235.22, 52.46) * mm, "mid": v(234.99, 52.16) * mm, "end": v(234.62, 52.04) * mm});
            skArc(sketch, "E663.MirrorCS", {"start": v(207.27, 52.04) * mm, "mid": v(206.9, 52.16) * mm, "end": v(206.67, 52.46) * mm});
            skArc(sketch, "E664.MirrorCS", {"start": v(263.15, 52.04) * mm, "mid": v(262.79, 52.16) * mm, "end": v(262.55, 52.46) * mm});
            skLineSegment(sketch, "E665.MirrorCS", {"start": v(281.98, 53.27) * mm, "end": v(282.4, 53.27) * mm});
            skLineSegment(sketch, "E666.MirrorCS", {"start": v(182.96, 51.82) * mm, "end": v(182.96, 52.04) * mm});
            skArc(sketch, "E667.MirrorCS", {"start": v(236.4, 53.3) * mm, "mid": v(236.76, 53.2) * mm, "end": v(237, 52.89) * mm});
            skLineSegment(sketch, "E668.MirrorCS", {"start": v(281.22, 52.43) * mm, "end": v(281.38, 52.85) * mm});
            skArc(sketch, "E669.MirrorCS", {"start": v(237.75, 52.04) * mm, "mid": v(237.39, 52.16) * mm, "end": v(237.15, 52.46) * mm});
            skLineSegment(sketch, "E670.MirrorCS", {"start": v(216.84, 51.18) * mm, "end": v(216.84, 51.47) * mm, "construction": true});
            skLineSegment(sketch, "E671.MirrorCS", {"start": v(283, 52.85) * mm, "end": v(283.15, 52.43) * mm});
            skLineSegment(sketch, "E672.MirrorCS", {"start": v(240.3, 52.46) * mm, "end": v(240.46, 52.89) * mm});
            skLineSegment(sketch, "E673.MirrorCS", {"start": v(279.76, 52) * mm, "end": v(280.62, 52) * mm});
            skLineSegment(sketch, "E674.MirrorCS", {"start": v(220.74, 53.3) * mm, "end": v(221.16, 53.3) * mm});
            skLineSegment(sketch, "E675.MirrorCS", {"start": v(225.06, 52.46) * mm, "end": v(225.22, 52.89) * mm});
            skLineSegment(sketch, "E676.MirrorCS", {"start": v(253.86, 51.82) * mm, "end": v(254.08, 51.82) * mm});
            skArc(sketch, "E677.MirrorCS", {"start": v(216.08, 53.3) * mm, "mid": v(216.44, 53.2) * mm, "end": v(216.68, 52.89) * mm});
            skLineSegment(sketch, "E678.MirrorCS", {"start": v(238.84, 51.82) * mm, "end": v(238.84, 52.04) * mm});
            skArc(sketch, "E679.MirrorCS", {"start": v(204.9, 52.89) * mm, "mid": v(205.13, 53.2) * mm, "end": v(205.5, 53.3) * mm});
            skArc(sketch, "E680.MirrorCS", {"start": v(277.32, 53.27) * mm, "mid": v(277.68, 53.16) * mm, "end": v(277.92, 52.85) * mm});
            skArc(sketch, "E681.MirrorCS", {"start": v(219.98, 52.46) * mm, "mid": v(219.75, 52.16) * mm, "end": v(219.38, 52.04) * mm});
            skArc(sketch, "E682.MirrorCS", {"start": v(215.06, 52.89) * mm, "mid": v(215.29, 53.2) * mm, "end": v(215.66, 53.3) * mm});
            skLineSegment(sketch, "E683.MirrorCS", {"start": v(217.43, 52.04) * mm, "end": v(218.3, 52.04) * mm});
            skArc(sketch, "E684.MirrorCS", {"start": v(261.8, 53.3) * mm, "mid": v(262.16, 53.2) * mm, "end": v(262.4, 52.89) * mm});
            skLineSegment(sketch, "E685.MirrorCS", {"start": v(221.76, 52.89) * mm, "end": v(221.91, 52.46) * mm});
            skLineSegment(sketch, "E686.MirrorCS", {"start": v(259.16, 51.82) * mm, "end": v(259.16, 52.04) * mm});
            skArc(sketch, "E687.MirrorCS", {"start": v(220.14, 52.89) * mm, "mid": v(220.37, 53.2) * mm, "end": v(220.74, 53.3) * mm});
            skArc(sketch, "E688.MirrorCS", {"start": v(276.14, 52.43) * mm, "mid": v(275.9, 52.12) * mm, "end": v(275.54, 52) * mm});
            skArc(sketch, "E689.MirrorCS", {"start": v(204.74, 52.46) * mm, "mid": v(204.5, 52.16) * mm, "end": v(204.14, 52.04) * mm});
            skLineSegment(sketch, "E690.MirrorCS", {"start": v(207.27, 52.04) * mm, "end": v(208.14, 52.04) * mm});
            skArc(sketch, "E691.MirrorCS", {"start": v(209.98, 52.89) * mm, "mid": v(210.2, 53.2) * mm, "end": v(210.58, 53.3) * mm});
            skLineSegment(sketch, "E692.MirrorCS", {"start": v(243.7, 52.04) * mm, "end": v(243.7, 51.82) * mm});
            skLineSegment(sketch, "E693.MirrorCS", {"start": v(211.6, 52.89) * mm, "end": v(211.75, 52.46) * mm});
            skLineSegment(sketch, "E694.MirrorCS", {"start": v(214.9, 52.46) * mm, "end": v(215.06, 52.89) * mm});
            skLineSegment(sketch, "E695.MirrorCS", {"start": v(223.6, 52.04) * mm, "end": v(224.46, 52.04) * mm});
            skArc(sketch, "E696.MirrorCS", {"start": v(205.92, 53.3) * mm, "mid": v(206.28, 53.2) * mm, "end": v(206.52, 52.89) * mm});
            skLineSegment(sketch, "E697.MirrorCS", {"start": v(277.92, 52.85) * mm, "end": v(278.07, 52.43) * mm});
            skArc(sketch, "E698.MirrorCS", {"start": v(217.43, 52.04) * mm, "mid": v(217.07, 52.16) * mm, "end": v(216.83, 52.46) * mm});
            skLineSegment(sketch, "E699.MirrorCS", {"start": v(274.68, 52) * mm, "end": v(275.54, 52) * mm});
            skLineSegment(sketch, "E700.MirrorCS", {"start": v(222.51, 52.04) * mm, "end": v(223.38, 52.04) * mm});
            skLineSegment(sketch, "E701.MirrorCS", {"start": v(205.5, 53.3) * mm, "end": v(205.92, 53.3) * mm});
            skArc(sketch, "E702.MirrorCS", {"start": v(222.51, 52.04) * mm, "mid": v(222.15, 52.16) * mm, "end": v(221.91, 52.46) * mm});
            skLineSegment(sketch, "E703.MirrorCS", {"start": v(257.32, 52.89) * mm, "end": v(257.47, 52.46) * mm});
            skLineSegment(sketch, "E704.MirrorCS", {"start": v(242.08, 52.89) * mm, "end": v(242.23, 52.46) * mm});
            skArc(sketch, "E705.MirrorCS", {"start": v(179.5, 52.89) * mm, "mid": v(179.73, 53.2) * mm, "end": v(180.1, 53.3) * mm});
            skLineSegment(sketch, "E706.MirrorCS", {"start": v(233.76, 51.82) * mm, "end": v(233.76, 52.04) * mm});
            skLineSegment(sketch, "E707.MirrorCS", {"start": v(237.75, 52.04) * mm, "end": v(238.62, 52.04) * mm});
            skArc(sketch, "E708.MirrorCS", {"start": v(260.62, 52.46) * mm, "mid": v(260.39, 52.16) * mm, "end": v(260.02, 52.04) * mm});
            skLineSegment(sketch, "E709.MirrorCS", {"start": v(213.22, 51.82) * mm, "end": v(213.44, 51.82) * mm});
            skLineSegment(sketch, "E710.MirrorCS", {"start": v(261.38, 53.3) * mm, "end": v(261.8, 53.3) * mm});
            skLineSegment(sketch, "E711.MirrorCS", {"start": v(228.68, 51.82) * mm, "end": v(228.68, 52.04) * mm});
            skLineSegment(sketch, "E712.MirrorCS", {"start": v(230.14, 52.46) * mm, "end": v(230.3, 52.89) * mm});
            skLineSegment(sketch, "E713.MirrorCS", {"start": v(225.13, 51.77) * mm, "end": v(224.9, 51.77) * mm, "construction": true});
            skArc(sketch, "E714.MirrorCS", {"start": v(227.6, 52.04) * mm, "mid": v(227.23, 52.16) * mm, "end": v(227, 52.46) * mm});
            skLineSegment(sketch, "E715.MirrorCS", {"start": v(233.54, 51.82) * mm, "end": v(233.76, 51.82) * mm});
            skLineSegment(sketch, "E716.MirrorCS", {"start": v(181.87, 52.04) * mm, "end": v(182.74, 52.04) * mm});
            skLineSegment(sketch, "E717.MirrorCS", {"start": v(262.4, 52.89) * mm, "end": v(262.55, 52.46) * mm});
            skLineSegment(sketch, "E718.MirrorCS", {"start": v(258.94, 52.04) * mm, "end": v(258.94, 51.82) * mm});
            skLineSegment(sketch, "E719.MirrorCS", {"start": v(255.54, 52.46) * mm, "end": v(255.7, 52.89) * mm});
            skLineSegment(sketch, "E720.MirrorCS", {"start": v(182.74, 51.82) * mm, "end": v(182.96, 51.82) * mm});
            skLineSegment(sketch, "E721.MirrorCS", {"start": v(243.7, 51.82) * mm, "end": v(243.92, 51.82) * mm});
            skLineSegment(sketch, "E722.MirrorCS", {"start": v(256.3, 53.3) * mm, "end": v(256.72, 53.3) * mm});
            skLineSegment(sketch, "E723.MirrorCS", {"start": v(238.62, 51.82) * mm, "end": v(238.84, 51.82) * mm});
            skArc(sketch, "E724.MirrorCS", {"start": v(211, 53.3) * mm, "mid": v(211.36, 53.2) * mm, "end": v(211.6, 52.89) * mm});
            skArc(sketch, "E725.MirrorCS", {"start": v(255.54, 52.46) * mm, "mid": v(255.3, 52.16) * mm, "end": v(254.94, 52.04) * mm});
            skLineSegment(sketch, "E726.MirrorCS", {"start": v(241.06, 53.3) * mm, "end": v(241.48, 53.3) * mm});
            skLineSegment(sketch, "E727.MirrorCS", {"start": v(181.12, 52.89) * mm, "end": v(181.27, 52.46) * mm});
            skLineSegment(sketch, "E728.MirrorCS", {"start": v(237, 52.89) * mm, "end": v(237.15, 52.46) * mm});
            skLineSegment(sketch, "E729.MirrorCS", {"start": v(212.35, 52.04) * mm, "end": v(213.22, 52.04) * mm});
            skLineSegment(sketch, "E730.MirrorCS", {"start": v(225.82, 53.3) * mm, "end": v(226.24, 53.3) * mm});
            skLineSegment(sketch, "E731.MirrorCS", {"start": v(235.98, 53.3) * mm, "end": v(236.4, 53.3) * mm});
            skArc(sketch, "E732.MirrorCS", {"start": v(230.14, 52.46) * mm, "mid": v(229.9, 52.16) * mm, "end": v(229.54, 52.04) * mm});
            skLineSegment(sketch, "E733.MirrorCS", {"start": v(254.08, 52.04) * mm, "end": v(254.94, 52.04) * mm});
            skLineSegment(sketch, "E734.MirrorCS", {"start": v(259.2, 51.48) * mm, "end": v(259.2, 51.77) * mm, "construction": true});
            skLineSegment(sketch, "E735.MirrorCS", {"start": v(233.76, 52.04) * mm, "end": v(234.62, 52.04) * mm});
            skArc(sketch, "E736.MirrorCS", {"start": v(225.06, 52.46) * mm, "mid": v(224.83, 52.16) * mm, "end": v(224.46, 52.04) * mm});
            skLineSegment(sketch, "E737.MirrorCS", {"start": v(260.62, 52.46) * mm, "end": v(260.78, 52.89) * mm});
            skLineSegment(sketch, "E738.MirrorCS", {"start": v(228.68, 52.04) * mm, "end": v(229.54, 52.04) * mm});
            skArc(sketch, "E739.MirrorCS", {"start": v(231.32, 53.3) * mm, "mid": v(231.68, 53.2) * mm, "end": v(231.92, 52.89) * mm});
            skArc(sketch, "E740.MirrorCS", {"start": v(256.72, 53.3) * mm, "mid": v(257.08, 53.2) * mm, "end": v(257.32, 52.89) * mm});
            skArc(sketch, "E741.MirrorCS", {"start": v(240.46, 52.89) * mm, "mid": v(240.69, 53.2) * mm, "end": v(241.06, 53.3) * mm});
            skLineSegment(sketch, "E742.MirrorCS", {"start": v(238.43, 51.3) * mm, "end": v(238.2, 51.3) * mm, "construction": true});
            skLineSegment(sketch, "E743.MirrorCS", {"start": v(232.67, 52.04) * mm, "end": v(233.54, 52.04) * mm});
            skLineSegment(sketch, "E744.MirrorCS", {"start": v(254.08, 51.82) * mm, "end": v(254.08, 52.04) * mm});
            skLineSegment(sketch, "E745.MirrorCS", {"start": v(284.62, 51.78) * mm, "end": v(284.84, 51.78) * mm});
            skLineSegment(sketch, "E746.MirrorCS", {"start": v(242.83, 52.04) * mm, "end": v(243.7, 52.04) * mm});
            skLineSegment(sketch, "E747.MirrorCS", {"start": v(230.9, 53.3) * mm, "end": v(231.32, 53.3) * mm});
            skArc(sketch, "E748.MirrorCS", {"start": v(226.24, 53.3) * mm, "mid": v(226.6, 53.2) * mm, "end": v(226.84, 52.89) * mm});
            skLineSegment(sketch, "E749.MirrorCS", {"start": v(238.31, 51.18) * mm, "end": v(238.31, 51.47) * mm, "construction": true});
            skLineSegment(sketch, "E750.MirrorCS", {"start": v(226.84, 52.89) * mm, "end": v(227, 52.46) * mm});
            skLineSegment(sketch, "E751.MirrorCS", {"start": v(228.46, 51.82) * mm, "end": v(228.68, 51.82) * mm});
            skLineSegment(sketch, "E752.MirrorCS", {"start": v(238.84, 52.04) * mm, "end": v(239.7, 52.04) * mm});
            skLineSegment(sketch, "E753.MirrorCS", {"start": v(225.02, 51.66) * mm, "end": v(225.02, 51.95) * mm, "construction": true});
            skArc(sketch, "E754.MirrorCS", {"start": v(241.48, 53.3) * mm, "mid": v(241.84, 53.2) * mm, "end": v(242.08, 52.89) * mm});
            skLineSegment(sketch, "E755.MirrorCS", {"start": v(263.15, 52.04) * mm, "end": v(264.02, 52.04) * mm});
            skArc(sketch, "E756.MirrorCS", {"start": v(235.38, 52.89) * mm, "mid": v(235.6, 53.2) * mm, "end": v(235.98, 53.3) * mm});
            skArc(sketch, "E757.MirrorCS", {"start": v(242.83, 52.04) * mm, "mid": v(242.47, 52.16) * mm, "end": v(242.23, 52.46) * mm});
            skLineSegment(sketch, "E758.MirrorCS", {"start": v(289.7, 52) * mm, "end": v(289.7, 51.78) * mm});
            skLineSegment(sketch, "E759.MirrorCS", {"start": v(235.22, 52.46) * mm, "end": v(235.38, 52.89) * mm});
            skArc(sketch, "E760.MirrorCS", {"start": v(225.22, 52.89) * mm, "mid": v(225.45, 53.2) * mm, "end": v(225.82, 53.3) * mm});
            skArc(sketch, "E761.MirrorCS", {"start": v(260.78, 52.89) * mm, "mid": v(261, 53.2) * mm, "end": v(261.38, 53.3) * mm});
            skLineSegment(sketch, "E762.MirrorCS", {"start": v(233.54, 52.04) * mm, "end": v(233.54, 51.82) * mm});
            skLineSegment(sketch, "E763.MirrorCS", {"start": v(258.07, 52.04) * mm, "end": v(258.94, 52.04) * mm});
            skLineSegment(sketch, "E764.MirrorCS", {"start": v(227.6, 52.04) * mm, "end": v(228.46, 52.04) * mm});
            skArc(sketch, "E765.MirrorCS", {"start": v(232.67, 52.04) * mm, "mid": v(232.3, 52.16) * mm, "end": v(232.07, 52.46) * mm});
            skArc(sketch, "E766.MirrorCS", {"start": v(258.07, 52.04) * mm, "mid": v(257.7, 52.16) * mm, "end": v(257.47, 52.46) * mm});
            skArc(sketch, "E767.MirrorCS", {"start": v(230.3, 52.89) * mm, "mid": v(230.53, 53.2) * mm, "end": v(230.9, 53.3) * mm});
            skArc(sketch, "E768.MirrorCS", {"start": v(255.7, 52.89) * mm, "mid": v(255.93, 53.2) * mm, "end": v(256.3, 53.3) * mm});
            skLineSegment(sketch, "E769.MirrorCS", {"start": v(259.16, 52.04) * mm, "end": v(260.02, 52.04) * mm});
            skLineSegment(sketch, "E770.MirrorCS", {"start": v(283.76, 52) * mm, "end": v(284.62, 52) * mm});
            skLineSegment(sketch, "E771.MirrorCS", {"start": v(5.08, 52.07) * mm, "end": v(5.08, 51.85) * mm});
            skArc(sketch, "E772.MirrorCS", {"start": v(6.92, 52.92) * mm, "mid": v(7.15, 53.22) * mm, "end": v(7.52, 53.34) * mm});
            skLineSegment(sketch, "E773.MirrorCS", {"start": v(288.08, 52.85) * mm, "end": v(288.23, 52.43) * mm});
            skLineSegment(sketch, "E774.MirrorCS", {"start": v(289.7, 51.78) * mm, "end": v(289.92, 51.78) * mm});
            skLineSegment(sketch, "E775.MirrorCS", {"start": v(259.32, 51.6) * mm, "end": v(259.1, 51.6) * mm, "construction": true});
            skLineSegment(sketch, "E776.MirrorCS", {"start": v(5.3, 52.07) * mm, "end": v(6.16, 52.07) * mm});
            skLineSegment(sketch, "E777.MirrorCS", {"start": v(286.3, 52.43) * mm, "end": v(286.46, 52.85) * mm});
            skLineSegment(sketch, "E778.MirrorCS", {"start": v(231.92, 52.89) * mm, "end": v(232.07, 52.46) * mm});
            skLineSegment(sketch, "E779.MirrorCS", {"start": v(5.08, 51.85) * mm, "end": v(5.3, 51.85) * mm});
            skArc(sketch, "E780.MirrorCS", {"start": v(286.3, 52.43) * mm, "mid": v(286.07, 52.12) * mm, "end": v(285.7, 52) * mm});
            skArc(sketch, "E781.MirrorCS", {"start": v(291.38, 52.43) * mm, "mid": v(291.15, 52.12) * mm, "end": v(290.78, 52) * mm});
            skLineSegment(sketch, "E782.MirrorCS", {"start": v(289.92, 51.78) * mm, "end": v(289.92, 52) * mm});
            skArc(sketch, "E783.MirrorCS", {"start": v(6.76, 52.5) * mm, "mid": v(6.53, 52.19) * mm, "end": v(6.16, 52.07) * mm});
            skLineSegment(sketch, "E784.MirrorCS", {"start": v(6.76, 52.5) * mm, "end": v(6.92, 52.92) * mm});
            skLineSegment(sketch, "E785.MirrorCS", {"start": v(284.84, 51.78) * mm, "end": v(284.84, 52) * mm});
            skArc(sketch, "E786.MirrorCS", {"start": v(288.84, 52) * mm, "mid": v(288.47, 52.12) * mm, "end": v(288.23, 52.43) * mm});
            skArc(sketch, "E787.MirrorCS", {"start": v(287.48, 53.27) * mm, "mid": v(287.84, 53.16) * mm, "end": v(288.08, 52.85) * mm});
            skLineSegment(sketch, "E788.MirrorCS", {"start": v(291.38, 52.43) * mm, "end": v(291.54, 52.85) * mm});
            skLineSegment(sketch, "E789.MirrorCS", {"start": v(2.44, 53.34) * mm, "end": v(2.86, 53.34) * mm});
            skLineSegment(sketch, "E790.MirrorCS", {"start": v(284.62, 52) * mm, "end": v(284.62, 51.78) * mm});
            skLineSegment(sketch, "E791.MirrorCS", {"start": v(5.3, 51.85) * mm, "end": v(5.3, 52.07) * mm});
            skLineSegment(sketch, "E792.MirrorCS", {"start": v(288.84, 52) * mm, "end": v(289.7, 52) * mm});
            skArc(sketch, "E793.MirrorCS", {"start": v(286.46, 52.85) * mm, "mid": v(286.7, 53.16) * mm, "end": v(287.06, 53.27) * mm});
            skLineSegment(sketch, "E794.MirrorCS", {"start": v(299.86, 52) * mm, "end": v(299.86, 51.78) * mm});
            skLineSegment(sketch, "E795.MirrorCS", {"start": v(289.92, 52) * mm, "end": v(290.78, 52) * mm});
            skLineSegment(sketch, "E796.MirrorCS", {"start": v(287.06, 53.27) * mm, "end": v(287.48, 53.27) * mm});
            skLineSegment(sketch, "E797.MirrorCS", {"start": v(284.84, 52) * mm, "end": v(285.7, 52) * mm});
            skLineSegment(sketch, "E798.MirrorCS", {"start": v(291.94, 51.7) * mm, "end": v(291.94, 51.99) * mm, "construction": true});
            skArc(sketch, "E799.MirrorCS", {"start": v(1.84, 52.92) * mm, "mid": v(2.07, 53.22) * mm, "end": v(2.44, 53.34) * mm});
            skLineSegment(sketch, "E800.MirrorCS", {"start": v(300.08, 51.78) * mm, "end": v(300.08, 52) * mm});
            skLineSegment(sketch, "E801.MirrorCS", {"start": v(4.22, 52.07) * mm, "end": v(5.08, 52.07) * mm});
            skLineSegment(sketch, "E802.MirrorCS", {"start": v(294.78, 52) * mm, "end": v(294.78, 51.78) * mm});
            skLineSegment(sketch, "E803.MirrorCS", {"start": v(5.2, 51.85) * mm, "end": v(5.2, 52.14) * mm, "construction": true});
            skLineSegment(sketch, "E804.MirrorCS", {"start": v(300.08, 52) * mm, "end": v(300.94, 52) * mm});
            skArc(sketch, "E805.MirrorCS", {"start": v(2.86, 53.34) * mm, "mid": v(3.23, 53.22) * mm, "end": v(3.46, 52.92) * mm});
            skArc(sketch, "E806.MirrorCS", {"start": v(4.22, 52.07) * mm, "mid": v(3.85, 52.19) * mm, "end": v(3.62, 52.5) * mm});
            skLineSegment(sketch, "E807.MirrorCS", {"start": v(295, 51.78) * mm, "end": v(295, 52) * mm});
            skLineSegment(sketch, "E808.MirrorCS", {"start": v(1.68, 52.5) * mm, "end": v(1.84, 52.92) * mm});
            skLineSegment(sketch, "E809.MirrorCS", {"start": v(5.3, 51.96) * mm, "end": v(5.08, 51.96) * mm, "construction": true});
            skLineSegment(sketch, "E810.MirrorCS", {"start": v(292.05, 51.81) * mm, "end": v(291.83, 51.81) * mm, "construction": true});
            skArc(sketch, "E811.MirrorCS", {"start": v(299, 52) * mm, "mid": v(298.63, 52.12) * mm, "end": v(298.4, 52.43) * mm});
            skLineSegment(sketch, "E812.MirrorCS", {"start": v(293.16, 52.85) * mm, "end": v(293.31, 52.43) * mm});
            skLineSegment(sketch, "E813.MirrorCS", {"start": v(3.46, 52.92) * mm, "end": v(3.62, 52.5) * mm});
            skLineSegment(sketch, "E814.MirrorCS", {"start": v(299, 52) * mm, "end": v(299.86, 52) * mm});
            skLineSegment(sketch, "E815.MirrorCS", {"start": v(295, 52) * mm, "end": v(295.86, 52) * mm});
            skArc(sketch, "E816.MirrorCS", {"start": v(291.54, 52.85) * mm, "mid": v(291.77, 53.16) * mm, "end": v(292.14, 53.27) * mm});
            skArc(sketch, "E817.MirrorCS", {"start": v(296.62, 52.85) * mm, "mid": v(296.85, 53.16) * mm, "end": v(297.22, 53.27) * mm});
            skLineSegment(sketch, "E818.MirrorCS", {"start": v(0.22, 52.07) * mm, "end": v(1.08, 52.07) * mm});
            skLineSegment(sketch, "E819.MirrorCS", {"start": v(1.08, 52.71) * mm, "end": v(11.23, 52.7) * mm, "construction": true});
            skArc(sketch, "E820.MirrorCS", {"start": v(1.68, 52.5) * mm, "mid": v(1.45, 52.19) * mm, "end": v(1.08, 52.07) * mm});
            skLineSegment(sketch, "E821.MirrorCS", {"start": v(293.92, 52) * mm, "end": v(294.78, 52) * mm});
            skLineSegment(sketch, "E822.MirrorCS", {"start": v(11.24, 50.8) * mm, "end": v(0, 50.8) * mm});
            skLineSegment(sketch, "E823.MirrorCS", {"start": v(301.54, 52.43) * mm, "end": v(301.7, 52.85) * mm});
            skLineSegment(sketch, "E824.MirrorCS", {"start": v(300.53, 51.6) * mm, "end": v(300.3, 51.6) * mm, "construction": true});
            skLineSegment(sketch, "E825.MirrorCS", {"start": v(299.86, 51.78) * mm, "end": v(300.08, 51.78) * mm});
            skLineSegment(sketch, "E826.MirrorCS", {"start": v(298.24, 52.85) * mm, "end": v(298.4, 52.43) * mm});
            skLineSegment(sketch, "E827.MirrorCS", {"start": v(292.14, 53.27) * mm, "end": v(292.56, 53.27) * mm});
            skArc(sketch, "E828.MirrorCS", {"start": v(301.7, 52.85) * mm, "mid": v(301.93, 53.16) * mm, "end": v(302.3, 53.27) * mm});
            skArc(sketch, "E829.MirrorCS", {"start": v(302.72, 53.27) * mm, "mid": v(303.08, 53.16) * mm, "end": v(303.32, 52.85) * mm});
            skArc(sketch, "E830.MirrorCS", {"start": v(293.92, 52) * mm, "mid": v(293.55, 52.12) * mm, "end": v(293.31, 52.43) * mm});
            skArc(sketch, "E831.MirrorCS", {"start": v(292.56, 53.27) * mm, "mid": v(292.92, 53.16) * mm, "end": v(293.16, 52.85) * mm});
            skLineSegment(sketch, "E832.MirrorCS", {"start": v(0, 50.8) * mm, "end": v(0, 51.85) * mm, "construction": true});
            skLineSegment(sketch, "E833.MirrorCS", {"start": v(300.42, 51.5) * mm, "end": v(300.42, 51.79) * mm, "construction": true});
            skLineSegment(sketch, "E834.MirrorCS", {"start": v(0, 51.85) * mm, "end": v(0.22, 51.85) * mm});
            skLineSegment(sketch, "E835.MirrorCS", {"start": v(297.22, 53.27) * mm, "end": v(297.64, 53.27) * mm});
            skArc(sketch, "E836.MirrorCS", {"start": v(304.08, 52) * mm, "mid": v(303.7, 52.12) * mm, "end": v(303.47, 52.43) * mm});
            skLineSegment(sketch, "E837.MirrorCS", {"start": v(296.46, 52.43) * mm, "end": v(296.62, 52.85) * mm});
            skLineSegment(sketch, "E838.MirrorCS", {"start": v(304.94, 52) * mm, "end": v(304.94, 51.78) * mm});
            skLineSegment(sketch, "E839.MirrorCS", {"start": v(294.78, 51.78) * mm, "end": v(295, 51.78) * mm});
            skArc(sketch, "E840.MirrorCS", {"start": v(296.46, 52.43) * mm, "mid": v(296.23, 52.12) * mm, "end": v(295.86, 52) * mm});
            skArc(sketch, "E841.MirrorCS", {"start": v(297.64, 53.27) * mm, "mid": v(298, 53.16) * mm, "end": v(298.24, 52.85) * mm});
            skLineSegment(sketch, "E842.MirrorCS", {"start": v(0.22, 51.85) * mm, "end": v(0.22, 52.07) * mm});
            skLineSegment(sketch, "E843.MirrorCS", {"start": v(302.3, 53.27) * mm, "end": v(302.72, 53.27) * mm});
            skArc(sketch, "E844.MirrorCS", {"start": v(301.54, 52.43) * mm, "mid": v(301.3, 52.12) * mm, "end": v(300.94, 52) * mm});
            skLineSegment(sketch, "E845.MirrorCS", {"start": v(305.16, 51.78) * mm, "end": v(305.16, 52) * mm});
            skLineSegment(sketch, "E846.MirrorCS", {"start": v(303.32, 52.85) * mm, "end": v(303.47, 52.43) * mm});
            skLineSegment(sketch, "E847.MirrorCS", {"start": v(304.08, 52) * mm, "end": v(304.94, 52) * mm});
            skLineSegment(sketch, "E848.MirrorCS", {"start": v(304.94, 51.78) * mm, "end": v(305.16, 51.78) * mm});
            skLineSegment(sketch, "E849.MirrorCS", {"start": v(305.16, 52) * mm, "end": v(306.02, 52) * mm});
            skPoint(sketch, "E850.MirrorP", {"position": v(38.82, 53.32) * mm});
            skPoint(sketch, "E851.MirrorP", {"position": v(140.98, 52.2) * mm});
            skPoint(sketch, "E852.MirrorP", {"position": v(261.75, 52.97) * mm});
            skPoint(sketch, "E853.MirrorP", {"position": v(42.1, 52.05) * mm});
            skPoint(sketch, "E854.MirrorP", {"position": v(22.94, 53.33) * mm});
            skPoint(sketch, "E855.MirrorP", {"position": v(58.45, 53.31) * mm});
            skPoint(sketch, "E856.MirrorP", {"position": v(266.43, 53.12) * mm});
            skPoint(sketch, "E857.MirrorP", {"position": v(64.17, 53.3) * mm});
            skPoint(sketch, "E858.MirrorP", {"position": v(11.67, 52.06) * mm});
            skPoint(sketch, "E859.MirrorP", {"position": v(139.01, 53.28) * mm});
            skPoint(sketch, "E860.MirrorP", {"position": v(96.49, 51.8) * mm});
            skPoint(sketch, "E861.MirrorP", {"position": v(94.84, 52.66) * mm});
            skPoint(sketch, "E862.MirrorP", {"position": v(193.8, 52.44) * mm});
            skPoint(sketch, "E863.MirrorP", {"position": v(49.43, 52.05) * mm});
            skPoint(sketch, "E864.MirrorP", {"position": v(88.88, 53.3) * mm});
            skPoint(sketch, "E865.MirrorP", {"position": v(276.22, 52.64) * mm});
            skPoint(sketch, "E866.MirrorP", {"position": v(79.86, 52.03) * mm});
            skPoint(sketch, "E867.MirrorP", {"position": v(67.47, 52.04) * mm});
            skPoint(sketch, "E868.MirrorP", {"position": v(257.32, 52.97) * mm});
            skPoint(sketch, "E869.MirrorP", {"position": v(37.04, 52.05) * mm});
            skPoint(sketch, "E870.MirrorP", {"position": v(214.95, 52.67) * mm});
            skPoint(sketch, "E871.MirrorP", {"position": v(151.13, 52.83) * mm});
            skPoint(sketch, "E872.MirrorP", {"position": v(214.3, 52.67) * mm});
            skPoint(sketch, "E873.MirrorP", {"position": v(100.53, 51.58) * mm});
            skPoint(sketch, "E874.MirrorP", {"position": v(42.57, 53.32) * mm});
            skPoint(sketch, "E875.MirrorP", {"position": v(271.51, 53.12) * mm});
            skPoint(sketch, "E876.MirrorP", {"position": v(100.07, 52.85) * mm});
            skPoint(sketch, "E877.MirrorP", {"position": v(135.25, 53.28) * mm});
            skPoint(sketch, "E878.MirrorP", {"position": v(198.88, 52.44) * mm});
            skPoint(sketch, "E879.MirrorP", {"position": v(177.05, 55.62) * mm});
            skPoint(sketch, "E880.MirrorP", {"position": v(33.74, 53.32) * mm});
            skPoint(sketch, "E881.MirrorP", {"position": v(82.91, 52.66) * mm});
            skPoint(sketch, "E882.MirrorP", {"position": v(248.11, 51.82) * mm});
            skPoint(sketch, "E883.MirrorP", {"position": v(73, 53.3) * mm});
            skPoint(sketch, "E884.MirrorP", {"position": v(139.43, 52.84) * mm});
            skPoint(sketch, "E885.MirrorP", {"position": v(28.02, 53.33) * mm});
            skPoint(sketch, "E886.MirrorP", {"position": v(22.05, 52.7) * mm});
            skPoint(sketch, "E887.MirrorP", {"position": v(133.47, 52.01) * mm});
            skPoint(sketch, "E888.MirrorP", {"position": v(19, 52.06) * mm});
            skPoint(sketch, "E889.MirrorP", {"position": v(273.3, 51.85) * mm});
            skPoint(sketch, "E890.MirrorP", {"position": v(213.18, 51.4) * mm});
            skPoint(sketch, "E891.MirrorP", {"position": v(57.8, 53.31) * mm});
            skPoint(sketch, "E892.MirrorP", {"position": v(52.48, 52.68) * mm});
            skPoint(sketch, "E893.MirrorP", {"position": v(12.14, 53.33) * mm});
            skPoint(sketch, "E894.MirrorP", {"position": v(236.43, 52.68) * mm});
            skPoint(sketch, "E895.MirrorP", {"position": v(151.6, 51.56) * mm});
            skPoint(sketch, "E896.MirrorP", {"position": v(260.63, 51.7) * mm});
            skPoint(sketch, "E897.MirrorP", {"position": v(140.8, 52.01) * mm});
            skPoint(sketch, "E898.MirrorP", {"position": v(88.22, 53.3) * mm});
            skPoint(sketch, "E899.MirrorP", {"position": v(291.94, 51.7) * mm});
            skPoint(sketch, "E900.MirrorP", {"position": v(192.68, 53.71) * mm});
            skPoint(sketch, "E901.MirrorP", {"position": v(282.19, 53.27) * mm});
            skPoint(sketch, "E902.MirrorP", {"position": v(215.19, 52.04) * mm});
            skPoint(sketch, "E903.MirrorP", {"position": v(66.05, 51.82) * mm});
            skPoint(sketch, "E904.MirrorP", {"position": v(244.92, 53.31) * mm});
            skPoint(sketch, "E905.MirrorP", {"position": v(191.74, 55.34) * mm});
            skPoint(sketch, "E906.MirrorP", {"position": v(269.63, 51.63) * mm});
            skPoint(sketch, "E907.MirrorP", {"position": v(208.02, 54.62) * mm});
            skPoint(sketch, "E908.MirrorP", {"position": v(142.63, 51.35) * mm});
            skPoint(sketch, "E909.MirrorP", {"position": v(48.96, 53.32) * mm});
            skPoint(sketch, "E910.MirrorP", {"position": v(221.82, 53.15) * mm});
            skPoint(sketch, "E911.MirrorP", {"position": v(133.7, 52.65) * mm});
            skPoint(sketch, "E912.MirrorP", {"position": v(6.61, 52.07) * mm});
            skPoint(sketch, "E913.MirrorP", {"position": v(290.06, 53.2) * mm});
            skPoint(sketch, "E914.MirrorP", {"position": v(276.45, 53.27) * mm});
            skPoint(sketch, "E915.MirrorP", {"position": v(114.27, 53.28) * mm});
            skPoint(sketch, "E916.MirrorP", {"position": v(3.3, 53.34) * mm});
            skPoint(sketch, "E917.MirrorP", {"position": v(267.75, 53.12) * mm});
            skPoint(sketch, "E918.MirrorP", {"position": v(175.04, 56.26) * mm});
            skPoint(sketch, "E919.MirrorP", {"position": v(201.4, 53.98) * mm});
            skPoint(sketch, "E920.MirrorP", {"position": v(79.4, 53.3) * mm});
            skPoint(sketch, "E921.MirrorP", {"position": v(206.7, 54.62) * mm});
            skPoint(sketch, "E922.MirrorP", {"position": v(130.63, 52.04) * mm});
            skPoint(sketch, "E923.MirrorP", {"position": v(130.16, 53.3) * mm});
            skPoint(sketch, "E924.MirrorP", {"position": v(234.89, 52.04) * mm});
            skPoint(sketch, "E925.MirrorP", {"position": v(278, 52.64) * mm});
            skPoint(sketch, "E926.MirrorP", {"position": v(245.57, 53.31) * mm});
            skPoint(sketch, "E927.MirrorP", {"position": v(74.78, 52.03) * mm});
            skPoint(sketch, "E928.MirrorP", {"position": v(293.82, 53.2) * mm});
            skPoint(sketch, "E929.MirrorP", {"position": v(139.67, 53.28) * mm});
            skPoint(sketch, "E930.MirrorP", {"position": v(52.25, 52.04) * mm});
            skPoint(sketch, "E931.MirrorP", {"position": v(218.26, 51.4) * mm});
            skPoint(sketch, "E932.MirrorP", {"position": v(33.97, 52.69) * mm});
            skPoint(sketch, "E933.MirrorP", {"position": v(99.03, 53.3) * mm});
            skPoint(sketch, "E934.MirrorP", {"position": v(21.82, 52.06) * mm});
            skPoint(sketch, "E935.MirrorP", {"position": v(155.55, 52.83) * mm});
            skPoint(sketch, "E936.MirrorP", {"position": v(190.43, 55.34) * mm});
            skPoint(sketch, "E937.MirrorP", {"position": v(188.55, 53.85) * mm});
            skPoint(sketch, "E938.MirrorP", {"position": v(191.56, 52.44) * mm});
            skPoint(sketch, "E939.MirrorP", {"position": v(35.62, 51.83) * mm});
            skPoint(sketch, "E940.MirrorP", {"position": v(93.95, 53.3) * mm});
            skPoint(sketch, "E941.MirrorP", {"position": v(105.15, 52.85) * mm});
            skPoint(sketch, "E942.MirrorP", {"position": v(159.61, 53.4) * mm});
            skPoint(sketch, "E943.MirrorP", {"position": v(13.92, 52.06) * mm});
            skPoint(sketch, "E944.MirrorP", {"position": v(255.78, 52.34) * mm});
            skPoint(sketch, "E945.MirrorP", {"position": v(64.4, 52.67) * mm});
            skPoint(sketch, "E946.MirrorP", {"position": v(82.68, 52.03) * mm});
            skPoint(sketch, "E947.MirrorP", {"position": v(161.16, 52.76) * mm});
            skPoint(sketch, "E948.MirrorP", {"position": v(27.36, 53.33) * mm});
            skPoint(sketch, "E949.MirrorP", {"position": v(120.47, 52.01) * mm});
            skPoint(sketch, "E950.MirrorP", {"position": v(193.57, 53.08) * mm});
            skPoint(sketch, "E951.MirrorP", {"position": v(222.48, 53.15) * mm});
            skPoint(sketch, "E952.MirrorP", {"position": v(154.43, 51.56) * mm});
            skPoint(sketch, "E953.MirrorP", {"position": v(294.48, 53.2) * mm});
            skPoint(sketch, "E954.MirrorP", {"position": v(98.37, 53.3) * mm});
            skPoint(sketch, "E955.MirrorP", {"position": v(123.77, 53.3) * mm});
            skPoint(sketch, "E956.MirrorP", {"position": v(228.22, 53.15) * mm});
            skPoint(sketch, "E957.MirrorP", {"position": v(140.33, 53.28) * mm});
            skPoint(sketch, "E958.MirrorP", {"position": v(262.4, 52.97) * mm});
            skPoint(sketch, "E959.MirrorP", {"position": v(266.2, 52.49) * mm});
            skPoint(sketch, "E960.MirrorP", {"position": v(59.57, 52.04) * mm});
            skPoint(sketch, "E961.MirrorP", {"position": v(74.32, 53.3) * mm});
            skPoint(sketch, "E962.MirrorP", {"position": v(251.77, 52.04) * mm});
            skPoint(sketch, "E963.MirrorP", {"position": v(138.55, 52.01) * mm});
            skPoint(sketch, "E964.MirrorP", {"position": v(246.23, 53.31) * mm});
            skPoint(sketch, "E965.MirrorP", {"position": v(140.75, 52.84) * mm});
            skPoint(sketch, "E966.MirrorP", {"position": v(192.02, 53.71) * mm});
            skPoint(sketch, "E967.MirrorP", {"position": v(203.4, 53.35) * mm});
            skPoint(sketch, "E968.MirrorP", {"position": v(244.45, 52.04) * mm});
            skPoint(sketch, "E969.MirrorP", {"position": v(297.88, 53) * mm});
            skPoint(sketch, "E970.MirrorP", {"position": v(146.3, 51.57) * mm});
            skPoint(sketch, "E971.MirrorP", {"position": v(33.08, 53.32) * mm});
            skPoint(sketch, "E972.MirrorP", {"position": v(166.47, 52.12) * mm});
            skPoint(sketch, "E973.MirrorP", {"position": v(186.66, 55.34) * mm});
            skPoint(sketch, "E974.MirrorP", {"position": v(290.52, 51.92) * mm});
            skPoint(sketch, "E975.MirrorP", {"position": v(63.51, 53.3) * mm});
            skPoint(sketch, "E976.MirrorP", {"position": v(44.35, 52.05) * mm});
            skPoint(sketch, "E977.MirrorP", {"position": v(149.58, 52.2) * mm});
            skPoint(sketch, "E978.MirrorP", {"position": v(220.03, 52.67) * mm});
            skPoint(sketch, "E979.MirrorP", {"position": v(7.07, 53.34) * mm});
            skPoint(sketch, "E980.MirrorP", {"position": v(90, 52.03) * mm});
            skPoint(sketch, "E981.MirrorP", {"position": v(181, 56.9) * mm});
            skPoint(sketch, "E982.MirrorP", {"position": v(100.3, 52.22) * mm});
            skPoint(sketch, "E983.MirrorP", {"position": v(114.92, 53.28) * mm});
            skPoint(sketch, "E984.MirrorP", {"position": v(18.53, 53.33) * mm});
            skPoint(sketch, "E985.MirrorP", {"position": v(240.85, 52.68) * mm});
            skPoint(sketch, "E986.MirrorP", {"position": v(279.65, 51.78) * mm});
            skPoint(sketch, "E987.MirrorP", {"position": v(3.77, 52.07) * mm});
            skPoint(sketch, "E988.MirrorP", {"position": v(216.84, 51.18) * mm});
            skPoint(sketch, "E989.MirrorP", {"position": v(195.22, 52.22) * mm});
            skPoint(sketch, "E990.MirrorP", {"position": v(77.62, 52.03) * mm});
            skPoint(sketch, "E991.MirrorP", {"position": v(47.19, 52.05) * mm});
            skPoint(sketch, "E992.MirrorP", {"position": v(124.43, 53.3) * mm});
            skPoint(sketch, "E993.MirrorP", {"position": v(103.37, 51.58) * mm});
            skPoint(sketch, "E994.MirrorP", {"position": v(29.14, 52.06) * mm});
            skPoint(sketch, "E995.MirrorP", {"position": v(175.93, 56.9) * mm});
            skPoint(sketch, "E996.MirrorP", {"position": v(202.29, 54.62) * mm});
            skPoint(sketch, "E997.MirrorP", {"position": v(101.95, 51.36) * mm});
            skPoint(sketch, "E998.MirrorP", {"position": v(3.54, 52.7) * mm});
            skPoint(sketch, "E999.MirrorP", {"position": v(164.7, 53.4) * mm});
            skPoint(sketch, "E1000.MirrorP", {"position": v(62.63, 52.67) * mm});
            skPoint(sketch, "E1001.MirrorP", {"position": v(288.5, 52.56) * mm});
            skPoint(sketch, "E1002.MirrorP", {"position": v(197.1, 53.71) * mm});
            skPoint(sketch, "E1003.MirrorP", {"position": v(16.75, 52.06) * mm});
            skPoint(sketch, "E1004.MirrorP", {"position": v(176.82, 56.26) * mm});
            skPoint(sketch, "E1005.MirrorP", {"position": v(118.23, 52.01) * mm});
            skPoint(sketch, "E1006.MirrorP", {"position": v(203.18, 53.98) * mm});
            skPoint(sketch, "E1007.MirrorP", {"position": v(221.36, 51.88) * mm});
            skPoint(sketch, "E1008.MirrorP", {"position": v(113.15, 52.01) * mm});
            skPoint(sketch, "E1009.MirrorP", {"position": v(120, 53.28) * mm});
            skPoint(sketch, "E1010.MirrorP", {"position": v(83.14, 53.3) * mm});
            skPoint(sketch, "E1011.MirrorP", {"position": v(239.73, 51.4) * mm});
            skPoint(sketch, "E1012.MirrorP", {"position": v(241.51, 52.68) * mm});
            skPoint(sketch, "E1013.MirrorP", {"position": v(52.71, 53.31) * mm});
            skPoint(sketch, "E1014.MirrorP", {"position": v(8.39, 53.34) * mm});
            skPoint(sketch, "E1015.MirrorP", {"position": v(265.97, 51.85) * mm});
            skPoint(sketch, "E1016.MirrorP", {"position": v(42.34, 52.68) * mm});
            skPoint(sketch, "E1017.MirrorP", {"position": v(99.4, 52.85) * mm});
            skPoint(sketch, "E1018.MirrorP", {"position": v(256, 52.97) * mm});
            skPoint(sketch, "E1019.MirrorP", {"position": v(149.81, 52.83) * mm});
            skPoint(sketch, "E1020.MirrorP", {"position": v(234.65, 51.4) * mm});
            skPoint(sketch, "E1021.MirrorP", {"position": v(246.46, 52.68) * mm});
            skPoint(sketch, "E1022.MirrorP", {"position": v(297.22, 53) * mm});
            skPoint(sketch, "E1023.MirrorP", {"position": v(138.97, 51.57) * mm});
            skPoint(sketch, "E1024.MirrorP", {"position": v(93.06, 52.66) * mm});
            skPoint(sketch, "E1025.MirrorP", {"position": v(272.17, 53.12) * mm});
            skPoint(sketch, "E1026.MirrorP", {"position": v(95.07, 52.02) * mm});
            skPoint(sketch, "E1027.MirrorP", {"position": v(187.13, 54.07) * mm});
            skPoint(sketch, "E1028.MirrorP", {"position": v(23.6, 53.33) * mm});
            skPoint(sketch, "E1029.MirrorP", {"position": v(32.43, 53.32) * mm});
            skPoint(sketch, "E1030.MirrorP", {"position": v(76.2, 51.81) * mm});
            skPoint(sketch, "E1031.MirrorP", {"position": v(277.1, 53.27) * mm});
            skPoint(sketch, "E1032.MirrorP", {"position": v(207.37, 54.62) * mm});
            skPoint(sketch, "E1033.MirrorP", {"position": v(125.32, 52.67) * mm});
            skPoint(sketch, "E1034.MirrorP", {"position": v(162.81, 51.9) * mm});
            skPoint(sketch, "E1035.MirrorP", {"position": v(43.88, 53.32) * mm});
            skPoint(sketch, "E1036.MirrorP", {"position": v(193.33, 53.71) * mm});
            skPoint(sketch, "E1037.MirrorP", {"position": v(1.76, 52.7) * mm});
            skPoint(sketch, "E1038.MirrorP", {"position": v(68.6, 53.3) * mm});
            skPoint(sketch, "E1039.MirrorP", {"position": v(191.09, 55.34) * mm});
            skPoint(sketch, "E1040.MirrorP", {"position": v(218.72, 52.67) * mm});
            skPoint(sketch, "E1041.MirrorP", {"position": v(223.6, 51.88) * mm});
            skPoint(sketch, "E1042.MirrorP", {"position": v(123.3, 52.04) * mm});
            skPoint(sketch, "E1043.MirrorP", {"position": v(298.77, 52.36) * mm});
            skPoint(sketch, "E1044.MirrorP", {"position": v(293.36, 51.92) * mm});
            skPoint(sketch, "E1045.MirrorP", {"position": v(144.05, 51.57) * mm});
            skPoint(sketch, "E1046.MirrorP", {"position": v(175.27, 56.9) * mm});
            skPoint(sketch, "E1047.MirrorP", {"position": v(118.69, 53.28) * mm});
            skPoint(sketch, "E1048.MirrorP", {"position": v(2.65, 53.34) * mm});
            skPoint(sketch, "E1049.MirrorP", {"position": v(257.79, 51.7) * mm});
            skPoint(sketch, "E1050.MirrorP", {"position": v(104.49, 52.85) * mm});
            skPoint(sketch, "E1051.MirrorP", {"position": v(240.2, 52.68) * mm});
            skPoint(sketch, "E1052.MirrorP", {"position": v(93.29, 53.3) * mm});
            skPoint(sketch, "E1053.MirrorP", {"position": v(296.76, 51.72) * mm});
            skPoint(sketch, "E1054.MirrorP", {"position": v(134.6, 53.28) * mm});
            skPoint(sketch, "E1055.MirrorP", {"position": v(48.3, 53.32) * mm});
            skPoint(sketch, "E1056.MirrorP", {"position": v(150.47, 52.83) * mm});
            skPoint(sketch, "E1057.MirrorP", {"position": v(191.79, 53.08) * mm});
            skPoint(sketch, "E1058.MirrorP", {"position": v(12.8, 53.33) * mm});
            skPoint(sketch, "E1059.MirrorP", {"position": v(55.91, 51.82) * mm});
            skPoint(sketch, "E1060.MirrorP", {"position": v(215.42, 51.4) * mm});
            skPoint(sketch, "E1061.MirrorP", {"position": v(74.55, 52.67) * mm});
            skPoint(sketch, "E1062.MirrorP", {"position": v(160.93, 53.4) * mm});
            skPoint(sketch, "E1063.MirrorP", {"position": v(201.63, 54.62) * mm});
            skPoint(sketch, "E1064.MirrorP", {"position": v(300.42, 51.5) * mm});
            skPoint(sketch, "E1065.MirrorP", {"position": v(126.97, 51.82) * mm});
            skPoint(sketch, "E1066.MirrorP", {"position": v(67.94, 53.3) * mm});
            skPoint(sketch, "E1067.MirrorP", {"position": v(22.28, 53.33) * mm});
            skPoint(sketch, "E1068.MirrorP", {"position": v(275.99, 52) * mm});
            skPoint(sketch, "E1069.MirrorP", {"position": v(13.45, 53.33) * mm});
            skPoint(sketch, "E1070.MirrorP", {"position": v(283.3, 52) * mm});
            skPoint(sketch, "E1071.MirrorP", {"position": v(249.53, 52.04) * mm});
            skPoint(sketch, "E1072.MirrorP", {"position": v(295.14, 53.2) * mm});
            skPoint(sketch, "E1073.MirrorP", {"position": v(5.2, 51.85) * mm});
            skPoint(sketch, "E1074.MirrorP", {"position": v(98.52, 52.22) * mm});
            skPoint(sketch, "E1075.MirrorP", {"position": v(185.12, 54.7) * mm});
            skPoint(sketch, "E1076.MirrorP", {"position": v(271.05, 51.85) * mm});
            skPoint(sketch, "E1077.MirrorP", {"position": v(228.68, 51.88) * mm});
            skPoint(sketch, "E1078.MirrorP", {"position": v(135.71, 52.01) * mm});
            skPoint(sketch, "E1079.MirrorP", {"position": v(223.37, 52.51) * mm});
            skPoint(sketch, "E1080.MirrorP", {"position": v(38.16, 53.32) * mm});
            skPoint(sketch, "E1081.MirrorP", {"position": v(277.77, 53.27) * mm});
            skPoint(sketch, "E1082.MirrorP", {"position": v(32.2, 52.69) * mm});
            skPoint(sketch, "E1083.MirrorP", {"position": v(84.92, 52.03) * mm});
            skPoint(sketch, "E1084.MirrorP", {"position": v(78.08, 53.3) * mm});
            skPoint(sketch, "E1085.MirrorP", {"position": v(225.02, 51.66) * mm});
            skPoint(sketch, "E1086.MirrorP", {"position": v(1.53, 52.07) * mm});
            skPoint(sketch, "E1087.MirrorP", {"position": v(165.35, 53.4) * mm});
            skPoint(sketch, "E1088.MirrorP", {"position": v(103.83, 52.85) * mm});
            skPoint(sketch, "E1089.MirrorP", {"position": v(128.85, 53.3) * mm});
            skPoint(sketch, "E1090.MirrorP", {"position": v(7.73, 53.34) * mm});
            skPoint(sketch, "E1091.MirrorP", {"position": v(57.33, 52.04) * mm});
            skPoint(sketch, "E1092.MirrorP", {"position": v(182.13, 55.62) * mm});
            skPoint(sketch, "E1093.MirrorP", {"position": v(15.34, 51.84) * mm});
            skPoint(sketch, "E1094.MirrorP", {"position": v(256.67, 52.97) * mm});
            skPoint(sketch, "E1095.MirrorP", {"position": v(251.31, 53.31) * mm});
            skPoint(sketch, "E1096.MirrorP", {"position": v(135.48, 52.65) * mm});
            skPoint(sketch, "E1097.MirrorP", {"position": v(145.83, 52.84) * mm});
            skPoint(sketch, "E1098.MirrorP", {"position": v(197.76, 53.71) * mm});
            skPoint(sketch, "E1099.MirrorP", {"position": v(156.67, 51.56) * mm});
            skPoint(sketch, "E1100.MirrorP", {"position": v(84.7, 52.66) * mm});
            skPoint(sketch, "E1101.MirrorP", {"position": v(204.83, 53.13) * mm});
            skPoint(sketch, "E1102.MirrorP", {"position": v(178.47, 55.4) * mm});
            skPoint(sketch, "E1103.MirrorP", {"position": v(262.87, 51.7) * mm});
            skPoint(sketch, "E1104.MirrorP", {"position": v(272.83, 53.12) * mm});
            skPoint(sketch, "E1105.MirrorP", {"position": v(69.71, 52.04) * mm});
            skPoint(sketch, "E1106.MirrorP", {"position": v(297, 52.36) * mm});
            skPoint(sketch, "E1107.MirrorP", {"position": v(31.96, 52.05) * mm});
            skPoint(sketch, "E1108.MirrorP", {"position": v(159.38, 52.76) * mm});
            skPoint(sketch, "E1109.MirrorP", {"position": v(149.35, 51.56) * mm});
            skPoint(sketch, "E1110.MirrorP", {"position": v(28.68, 53.33) * mm});
            skPoint(sketch, "E1111.MirrorP", {"position": v(235.77, 52.68) * mm});
            skPoint(sketch, "E1112.MirrorP", {"position": v(192.2, 54.07) * mm});
            skPoint(sketch, "E1113.MirrorP", {"position": v(302.3, 53) * mm});
            skPoint(sketch, "E1114.MirrorP", {"position": v(298.54, 53) * mm});
            skPoint(sketch, "E1115.MirrorP", {"position": v(115.39, 52.01) * mm});
            skPoint(sketch, "E1116.MirrorP", {"position": v(219.38, 52.67) * mm});
            skPoint(sketch, "E1117.MirrorP", {"position": v(281.07, 52) * mm});
            skPoint(sketch, "E1118.MirrorP", {"position": v(236.9, 51.4) * mm});
            skPoint(sketch, "E1119.MirrorP", {"position": v(8.85, 52.07) * mm});
            skPoint(sketch, "E1120.MirrorP", {"position": v(119.35, 53.28) * mm});
            skPoint(sketch, "E1121.MirrorP", {"position": v(288.74, 53.2) * mm});
            skPoint(sketch, "E1122.MirrorP", {"position": v(45.77, 51.83) * mm});
            skPoint(sketch, "E1123.MirrorP", {"position": v(92.83, 52.02) * mm});
            skPoint(sketch, "E1124.MirrorP", {"position": v(226.9, 53.15) * mm});
            skPoint(sketch, "E1125.MirrorP", {"position": v(302.96, 53) * mm});
            skPoint(sketch, "E1126.MirrorP", {"position": v(223.14, 53.15) * mm});
            skPoint(sketch, "E1127.MirrorP", {"position": v(73.66, 53.3) * mm});
            skPoint(sketch, "E1128.MirrorP", {"position": v(151.36, 52.2) * mm});
            skPoint(sketch, "E1129.MirrorP", {"position": v(236.66, 52.04) * mm});
            skPoint(sketch, "E1130.MirrorP", {"position": v(196.64, 52.44) * mm});
            skPoint(sketch, "E1131.MirrorP", {"position": v(250, 53.31) * mm});
            skPoint(sketch, "E1132.MirrorP", {"position": v(13.68, 52.7) * mm});
            skPoint(sketch, "E1133.MirrorP", {"position": v(185.35, 55.34) * mm});
            skPoint(sketch, "E1134.MirrorP", {"position": v(268.21, 51.85) * mm});
            skPoint(sketch, "E1135.MirrorP", {"position": v(84.46, 53.3) * mm});
            skPoint(sketch, "E1136.MirrorP", {"position": v(115.16, 52.65) * mm});
            skPoint(sketch, "E1137.MirrorP", {"position": v(141.21, 51.57) * mm});
            skPoint(sketch, "E1138.MirrorP", {"position": v(176.59, 56.9) * mm});
            skPoint(sketch, "E1139.MirrorP", {"position": v(113.38, 52.65) * mm});
            skPoint(sketch, "E1140.MirrorP", {"position": v(186, 55.34) * mm});
            skPoint(sketch, "E1141.MirrorP", {"position": v(139.2, 52.2) * mm});
            skPoint(sketch, "E1142.MirrorP", {"position": v(100.15, 52.02) * mm});
            skPoint(sketch, "E1143.MirrorP", {"position": v(144.51, 52.84) * mm});
            skPoint(sketch, "E1144.MirrorP", {"position": v(129.5, 53.3) * mm});
            skPoint(sketch, "E1145.MirrorP", {"position": v(2, 53.34) * mm});
            skPoint(sketch, "E1146.MirrorP", {"position": v(125.08, 53.3) * mm});
            skPoint(sketch, "E1147.MirrorP", {"position": v(89.54, 53.3) * mm});
            skPoint(sketch, "E1148.MirrorP", {"position": v(44.12, 52.68) * mm});
            skPoint(sketch, "E1149.MirrorP", {"position": v(11.9, 52.7) * mm});
            skPoint(sketch, "E1150.MirrorP", {"position": v(282.85, 53.27) * mm});
            skPoint(sketch, "E1151.MirrorP", {"position": v(54.5, 52.04) * mm});
            skPoint(sketch, "E1152.MirrorP", {"position": v(289.4, 53.2) * mm});
            skPoint(sketch, "E1153.MirrorP", {"position": v(62.86, 53.3) * mm});
            skPoint(sketch, "E1154.MirrorP", {"position": v(164.23, 52.12) * mm});
            skPoint(sketch, "E1155.MirrorP", {"position": v(24.06, 52.06) * mm});
            skPoint(sketch, "E1156.MirrorP", {"position": v(98.29, 51.58) * mm});
            skPoint(sketch, "E1157.MirrorP", {"position": v(208.49, 53.35) * mm});
            skPoint(sketch, "E1158.MirrorP", {"position": v(255.55, 51.7) * mm});
            skPoint(sketch, "E1159.MirrorP", {"position": v(37.5, 53.32) * mm});
            skPoint(sketch, "E1160.MirrorP", {"position": v(213.4, 52.04) * mm});
            skPoint(sketch, "E1161.MirrorP", {"position": v(301.84, 51.72) * mm});
            skPoint(sketch, "E1162.MirrorP", {"position": v(72.77, 52.67) * mm});
            skPoint(sketch, "E1163.MirrorP", {"position": v(202.94, 54.62) * mm});
            skPoint(sketch, "E1164.MirrorP", {"position": v(281.53, 53.27) * mm});
            skPoint(sketch, "E1165.MirrorP", {"position": v(156.2, 52.83) * mm});
            skPoint(sketch, "E1166.MirrorP", {"position": v(43.23, 53.32) * mm});
            skPoint(sketch, "E1167.MirrorP", {"position": v(186.9, 54.7) * mm});
            skPoint(sketch, "E1168.MirrorP", {"position": v(288.28, 51.92) * mm});
            skPoint(sketch, "E1169.MirrorP", {"position": v(128.39, 52.04) * mm});
            skPoint(sketch, "E1170.MirrorP", {"position": v(54.03, 53.31) * mm});
            skPoint(sketch, "E1171.MirrorP", {"position": v(235.12, 52.68) * mm});
            skPoint(sketch, "E1172.MirrorP", {"position": v(62.4, 52.04) * mm});
            skPoint(sketch, "E1173.MirrorP", {"position": v(250.65, 53.31) * mm});
            skPoint(sketch, "E1174.MirrorP", {"position": v(246.7, 52.04) * mm});
            skPoint(sketch, "E1175.MirrorP", {"position": v(125.55, 52.04) * mm});
            skPoint(sketch, "E1176.MirrorP", {"position": v(133.93, 53.28) * mm});
            skPoint(sketch, "E1177.MirrorP", {"position": v(113.6, 53.28) * mm});
            skPoint(sketch, "E1178.MirrorP", {"position": v(39.28, 52.05) * mm});
            skPoint(sketch, "E1179.MirrorP", {"position": v(179.89, 55.62) * mm});
            skPoint(sketch, "E1180.MirrorP", {"position": v(295.6, 51.92) * mm});
            skPoint(sketch, "E1181.MirrorP", {"position": v(140.1, 52.84) * mm});
            skPoint(sketch, "E1182.MirrorP", {"position": v(99.68, 53.3) * mm});
            skPoint(sketch, "E1183.MirrorP", {"position": v(267.1, 53.12) * mm});
            skPoint(sketch, "E1184.MirrorP", {"position": v(198.41, 53.71) * mm});
            skPoint(sketch, "E1185.MirrorP", {"position": v(153.01, 51.34) * mm});
            skPoint(sketch, "E1186.MirrorP", {"position": v(181.67, 56.9) * mm});
            skPoint(sketch, "E1187.MirrorP", {"position": v(160.27, 53.4) * mm});
            skPoint(sketch, "E1188.MirrorP", {"position": v(25.48, 51.84) * mm});
            skPoint(sketch, "E1189.MirrorP", {"position": v(184.89, 54.07) * mm});
            skPoint(sketch, "E1190.MirrorP", {"position": v(221.6, 52.51) * mm});
            skPoint(sketch, "E1191.MirrorP", {"position": v(97.9, 52.02) * mm});
            skPoint(sketch, "E1192.MirrorP", {"position": v(166, 53.4) * mm});
            skPoint(sketch, "E1193.MirrorP", {"position": v(26.9, 52.06) * mm});
            skPoint(sketch, "E1194.MirrorP", {"position": v(257.55, 52.34) * mm});
            skPoint(sketch, "E1195.MirrorP", {"position": v(59.1, 53.31) * mm});
            skPoint(sketch, "E1196.MirrorP", {"position": v(304.08, 51.72) * mm});
            skPoint(sketch, "E1197.MirrorP", {"position": v(87.76, 52.03) * mm});
            skPoint(sketch, "E1198.MirrorP", {"position": v(86.34, 51.8) * mm});
            skPoint(sketch, "E1199.MirrorP", {"position": v(17.88, 53.33) * mm});
            skPoint(sketch, "E1200.MirrorP", {"position": v(78.74, 53.3) * mm});
            skPoint(sketch, "E1201.MirrorP", {"position": v(213.64, 52.67) * mm});
            skPoint(sketch, "E1202.MirrorP", {"position": v(227.56, 53.15) * mm});
            skPoint(sketch, "E1203.MirrorP", {"position": v(290.29, 52.56) * mm});
            skPoint(sketch, "E1204.MirrorP", {"position": v(154.9, 52.83) * mm});
            skPoint(sketch, "E1205.MirrorP", {"position": v(278.23, 52) * mm});
            skPoint(sketch, "E1206.MirrorP", {"position": v(69.25, 53.3) * mm});
            skPoint(sketch, "E1207.MirrorP", {"position": v(161.4, 52.12) * mm});
            skPoint(sketch, "E1208.MirrorP", {"position": v(267.98, 52.49) * mm});
            skPoint(sketch, "E1209.MirrorP", {"position": v(244.68, 52.68) * mm});
            skPoint(sketch, "E1210.MirrorP", {"position": v(226.44, 51.88) * mm});
            skPoint(sketch, "E1211.MirrorP", {"position": v(259.2, 51.48) * mm});
            skPoint(sketch, "E1212.MirrorP", {"position": v(64.63, 52.04) * mm});
            skPoint(sketch, "E1213.MirrorP", {"position": v(189.97, 54.07) * mm});
            skPoint(sketch, "E1214.MirrorP", {"position": v(201.17, 53.35) * mm});
            skPoint(sketch, "E1215.MirrorP", {"position": v(174.8, 55.62) * mm});
            skPoint(sketch, "E1216.MirrorP", {"position": v(98.75, 52.85) * mm});
            skPoint(sketch, "E1217.MirrorP", {"position": v(303.62, 53) * mm});
            skPoint(sketch, "E1218.MirrorP", {"position": v(47.65, 53.32) * mm});
            skPoint(sketch, "E1219.MirrorP", {"position": v(17.22, 53.33) * mm});
            skPoint(sketch, "E1220.MirrorP", {"position": v(137.13, 51.8) * mm});
            skPoint(sketch, "E1221.MirrorP", {"position": v(159.15, 52.12) * mm});
            skPoint(sketch, "E1222.MirrorP", {"position": v(94.6, 53.3) * mm});
            skPoint(sketch, "E1223.MirrorP", {"position": v(238.31, 51.18) * mm});
            skPoint(sketch, "E1224.MirrorP", {"position": v(53.37, 53.31) * mm});
            skPoint(sketch, "E1225.MirrorP", {"position": v(54.26, 52.68) * mm});
            skPoint(sketch, "E1226.MirrorP", {"position": v(123.54, 52.67) * mm});
            skPoint(sketch, "E1227.MirrorP", {"position": v(116.8, 51.8) * mm});
            skPoint(sketch, "E1228.MirrorP", {"position": v(34.2, 52.05) * mm});
            skPoint(sketch, "E1229.MirrorP", {"position": v(299, 51.72) * mm});
            skPoint(sketch, "E1230.MirrorP", {"position": v(72.54, 52.03) * mm});
            skPoint(sketch, "E1231.MirrorP", {"position": v(241.97, 51.4) * mm});
            skPoint(sketch, "E1232.MirrorP", {"position": v(105.6, 51.58) * mm});
            skPoint(sketch, "E1233.MirrorP", {"position": v(180.35, 56.9) * mm});
            skPoint(sketch, "E1234.MirrorP", {"position": v(220.5, 51.4) * mm});
            skPoint(sketch, "E1235.MirrorP", {"position": v(83.8, 53.3) * mm});
            skPoint(sketch, "E1236.MirrorP", {"position": v(206.25, 53.35) * mm});
            skPoint(sketch, "E1237.MirrorP", {"position": v(261.09, 52.97) * mm});
            skPoint(sketch, "E1238.MirrorP", {"position": v(145.17, 52.84) * mm});
            skPoint(sketch, "E1239.MirrorP", {"position": v(23.83, 52.7) * mm});
            skLineSegment(sketch, "E1240", {"start": v(204.3, 36.98) * mm, "end": v(317.19, 36.98) * mm});
            skLineSegment(sketch, "E1241", {"start": v(204.3, 10.47) * mm, "end": v(317.19, 10.47) * mm});
            skSolve(sketch);
        }
        {
            var Q0;
            Q0=qCreatedBy(makeId("Front.planeOp"),FACE);
            var sketch = newSketch(context, id + "F1", { "sketchPlane" : qUnion([Q0])});
            skLineSegment(sketch, "E1242", {"start": v(0, 0) * mm, "end": v(304.8, 0) * mm});
            skLineSegment(sketch, "E1243.0", {"start": v(0, 50.8) * mm, "end": v(304.8, 50.8) * mm});
            skArc(sketch, "E1244", {"start": v(0, 50.8) * mm, "mid": v(-25.4, 25.4) * mm, "end": v(0, 0) * mm});
            skArc(sketch, "E1245", {"start": v(304.8, 50.8) * mm, "mid": v(330.2, 25.4) * mm, "end": v(304.8, 0) * mm});
            skLineSegment(sketch, "E1246.0", {"start": v(0, 25.4) * mm, "end": v(304.8, 25.4) * mm, "construction": true});
            skSolve(sketch);
        }
        {
            var Q0;
            Q0 = qSketchRegion(id + "F1", true);
            var Q1;
            Q1 = qConstructionFilter(qBodyType(qCreatedBy(id + "F0" ,EDGE), BodyType.WIRE), ConstructionObject.NO);
            extrude(context, id + "F2", {"entities" : qUnion([Q0]), "bodyType" : ToolBodyType.SURFACE, "surfaceEntities" : qUnion([Q1]), "depth" : 25.4 * mm, "offsetDistance" : 25.4 * mm});
        }
    });
